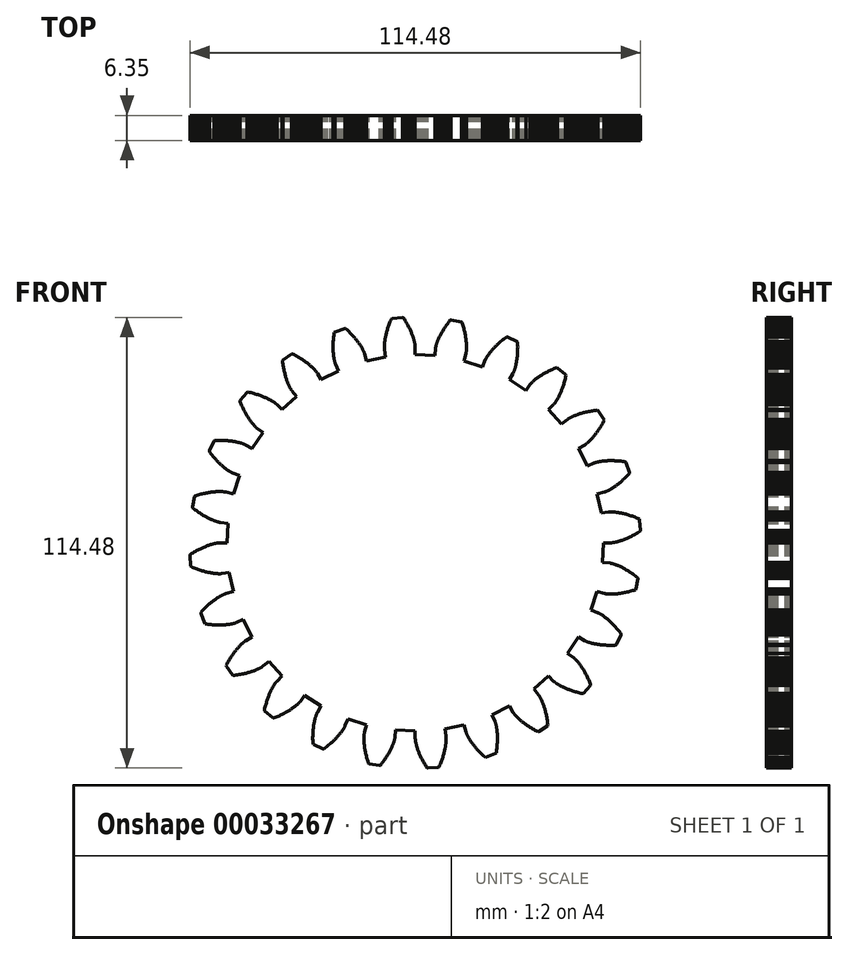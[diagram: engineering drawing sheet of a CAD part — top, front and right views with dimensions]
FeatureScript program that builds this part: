
annotation { "Feature Type Name" : "Feature", "Feature Type Description" : "" }
export const myFeature = defineFeature(function(context is Context, id is Id, definition is map)
    precondition{}
    {
        {
            var Q0;
            Q0=qCreatedBy(makeId("Front.planeOp"),FACE);
            var sketch = newSketch(context, id + "F0", { "sketchPlane" : qUnion([Q0])});
            skLineSegment(sketch, "E0", {"start": v(47.85, 0) * mm, "end": v(49.75, 0) * mm});
            skLineSegment(sketch, "E1", {"start": v(49.75, 0) * mm, "end": v(49.78, 0) * mm});
            skLineSegment(sketch, "E2", {"start": v(49.78, 0) * mm, "end": v(49.82, 0) * mm});
            skLineSegment(sketch, "E3", {"start": v(49.82, 0) * mm, "end": v(49.87, 0) * mm});
            skLineSegment(sketch, "E4", {"start": v(49.87, 0) * mm, "end": v(49.93, 0.01) * mm});
            skLineSegment(sketch, "E5", {"start": v(49.93, 0.01) * mm, "end": v(50, 0.02) * mm});
            skLineSegment(sketch, "E6", {"start": v(50, 0.02) * mm, "end": v(50.08, 0.03) * mm});
            skLineSegment(sketch, "E7", {"start": v(50.08, 0.03) * mm, "end": v(50.17, 0.04) * mm});
            skLineSegment(sketch, "E8", {"start": v(50.17, 0.04) * mm, "end": v(50.27, 0.05) * mm});
            skLineSegment(sketch, "E9", {"start": v(50.27, 0.05) * mm, "end": v(50.38, 0.07) * mm});
            skLineSegment(sketch, "E10", {"start": v(50.38, 0.07) * mm, "end": v(50.5, 0.1) * mm});
            skLineSegment(sketch, "E11", {"start": v(50.5, 0.1) * mm, "end": v(50.63, 0.12) * mm});
            skLineSegment(sketch, "E12", {"start": v(50.63, 0.12) * mm, "end": v(50.78, 0.15) * mm});
            skLineSegment(sketch, "E13", {"start": v(50.78, 0.15) * mm, "end": v(50.93, 0.18) * mm});
            skLineSegment(sketch, "E14", {"start": v(50.93, 0.18) * mm, "end": v(51.09, 0.21) * mm});
            skLineSegment(sketch, "E15", {"start": v(51.09, 0.21) * mm, "end": v(51.26, 0.26) * mm});
            skLineSegment(sketch, "E16", {"start": v(51.26, 0.26) * mm, "end": v(51.44, 0.3) * mm});
            skLineSegment(sketch, "E17", {"start": v(51.44, 0.3) * mm, "end": v(51.63, 0.36) * mm});
            skLineSegment(sketch, "E18", {"start": v(51.63, 0.36) * mm, "end": v(51.83, 0.42) * mm});
            skLineSegment(sketch, "E19", {"start": v(51.83, 0.42) * mm, "end": v(52.03, 0.48) * mm});
            skLineSegment(sketch, "E20", {"start": v(52.03, 0.48) * mm, "end": v(52.25, 0.55) * mm});
            skLineSegment(sketch, "E21", {"start": v(52.25, 0.55) * mm, "end": v(52.48, 0.63) * mm});
            skLineSegment(sketch, "E22", {"start": v(52.48, 0.63) * mm, "end": v(52.71, 0.71) * mm});
            skLineSegment(sketch, "E23", {"start": v(52.71, 0.71) * mm, "end": v(52.95, 0.8) * mm});
            skLineSegment(sketch, "E24", {"start": v(52.95, 0.8) * mm, "end": v(53.2, 0.9) * mm});
            skLineSegment(sketch, "E25", {"start": v(53.2, 0.9) * mm, "end": v(53.47, 1) * mm});
            skLineSegment(sketch, "E26", {"start": v(53.47, 1) * mm, "end": v(53.73, 1.12) * mm});
            skLineSegment(sketch, "E27", {"start": v(53.73, 1.12) * mm, "end": v(54, 1.25) * mm});
            skLineSegment(sketch, "E28", {"start": v(54, 1.25) * mm, "end": v(54.3, 1.38) * mm});
            skLineSegment(sketch, "E29", {"start": v(54.3, 1.38) * mm, "end": v(54.58, 1.52) * mm});
            skLineSegment(sketch, "E30", {"start": v(54.58, 1.52) * mm, "end": v(54.88, 1.67) * mm});
            skLineSegment(sketch, "E31", {"start": v(54.88, 1.67) * mm, "end": v(55.19, 1.82) * mm});
            skLineSegment(sketch, "E32", {"start": v(55.19, 1.82) * mm, "end": v(55.5, 1.99) * mm});
            skLineSegment(sketch, "E33", {"start": v(55.5, 1.99) * mm, "end": v(55.82, 2.17) * mm});
            skLineSegment(sketch, "E34", {"start": v(55.82, 2.17) * mm, "end": v(56.15, 2.35) * mm});
            skLineSegment(sketch, "E35", {"start": v(56.15, 2.35) * mm, "end": v(56.48, 2.55) * mm});
            skLineSegment(sketch, "E36", {"start": v(56.48, 2.55) * mm, "end": v(56.82, 2.76) * mm});
            skLineSegment(sketch, "E37", {"start": v(56.82, 2.76) * mm, "end": v(57.16, 2.97) * mm});
            skLineSegment(sketch, "E38", {"start": v(57.16, 2.97) * mm, "end": v(57.24, 3.19) * mm});
            skLineSegment(sketch, "E39", {"start": v(57.24, 3.19) * mm, "end": v(57.03, 5.86) * mm});
            skLineSegment(sketch, "E40", {"start": v(57.03, 5.86) * mm, "end": v(56.92, 6.06) * mm});
            skLineSegment(sketch, "E41", {"start": v(56.92, 6.06) * mm, "end": v(56.54, 6.22) * mm});
            skLineSegment(sketch, "E42", {"start": v(56.54, 6.22) * mm, "end": v(56.18, 6.37) * mm});
            skLineSegment(sketch, "E43", {"start": v(56.18, 6.37) * mm, "end": v(55.82, 6.5) * mm});
            skLineSegment(sketch, "E44", {"start": v(55.82, 6.5) * mm, "end": v(55.47, 6.64) * mm});
            skLineSegment(sketch, "E45", {"start": v(55.47, 6.64) * mm, "end": v(55.12, 6.77) * mm});
            skLineSegment(sketch, "E46", {"start": v(55.12, 6.77) * mm, "end": v(54.79, 6.88) * mm});
            skLineSegment(sketch, "E47", {"start": v(54.79, 6.88) * mm, "end": v(54.46, 6.99) * mm});
            skLineSegment(sketch, "E48", {"start": v(54.46, 6.99) * mm, "end": v(54.14, 7.1) * mm});
            skLineSegment(sketch, "E49", {"start": v(54.14, 7.1) * mm, "end": v(53.83, 7.18) * mm});
            skLineSegment(sketch, "E50", {"start": v(53.83, 7.18) * mm, "end": v(53.53, 7.27) * mm});
            skLineSegment(sketch, "E51", {"start": v(53.53, 7.27) * mm, "end": v(53.24, 7.34) * mm});
            skLineSegment(sketch, "E52", {"start": v(53.24, 7.34) * mm, "end": v(52.96, 7.41) * mm});
            skLineSegment(sketch, "E53", {"start": v(52.96, 7.41) * mm, "end": v(52.69, 7.48) * mm});
            skLineSegment(sketch, "E54", {"start": v(52.69, 7.48) * mm, "end": v(52.42, 7.54) * mm});
            skLineSegment(sketch, "E55", {"start": v(52.42, 7.54) * mm, "end": v(52.17, 7.59) * mm});
            skLineSegment(sketch, "E56", {"start": v(52.17, 7.59) * mm, "end": v(51.92, 7.63) * mm});
            skLineSegment(sketch, "E57", {"start": v(51.92, 7.63) * mm, "end": v(51.69, 7.68) * mm});
            skLineSegment(sketch, "E58", {"start": v(51.69, 7.68) * mm, "end": v(51.46, 7.71) * mm});
            skLineSegment(sketch, "E59", {"start": v(51.46, 7.71) * mm, "end": v(51.25, 7.74) * mm});
            skLineSegment(sketch, "E60", {"start": v(51.25, 7.74) * mm, "end": v(51.04, 7.77) * mm});
            skLineSegment(sketch, "E61", {"start": v(51.04, 7.77) * mm, "end": v(50.84, 7.8) * mm});
            skLineSegment(sketch, "E62", {"start": v(50.84, 7.8) * mm, "end": v(50.66, 7.8) * mm});
            skLineSegment(sketch, "E63", {"start": v(50.66, 7.8) * mm, "end": v(50.48, 7.82) * mm});
            skLineSegment(sketch, "E64", {"start": v(50.48, 7.82) * mm, "end": v(50.32, 7.84) * mm});
            skLineSegment(sketch, "E65", {"start": v(50.32, 7.84) * mm, "end": v(50.16, 7.85) * mm});
            skLineSegment(sketch, "E66", {"start": v(50.16, 7.85) * mm, "end": v(50.02, 7.85) * mm});
            skLineSegment(sketch, "E67", {"start": v(50.02, 7.85) * mm, "end": v(49.89, 7.86) * mm});
            skLineSegment(sketch, "E68", {"start": v(49.89, 7.86) * mm, "end": v(49.77, 7.86) * mm});
            skLineSegment(sketch, "E69", {"start": v(49.77, 7.86) * mm, "end": v(49.65, 7.86) * mm});
            skLineSegment(sketch, "E70", {"start": v(49.65, 7.86) * mm, "end": v(49.55, 7.85) * mm});
            skLineSegment(sketch, "E71", {"start": v(49.55, 7.85) * mm, "end": v(49.46, 7.85) * mm});
            skLineSegment(sketch, "E72", {"start": v(49.46, 7.85) * mm, "end": v(49.38, 7.85) * mm});
            skLineSegment(sketch, "E73", {"start": v(49.38, 7.85) * mm, "end": v(49.3, 7.84) * mm});
            skLineSegment(sketch, "E74", {"start": v(49.3, 7.84) * mm, "end": v(49.25, 7.84) * mm});
            skLineSegment(sketch, "E75", {"start": v(49.25, 7.84) * mm, "end": v(49.2, 7.83) * mm});
            skLineSegment(sketch, "E76", {"start": v(49.2, 7.83) * mm, "end": v(49.16, 7.83) * mm});
            skLineSegment(sketch, "E77", {"start": v(49.16, 7.83) * mm, "end": v(49.13, 7.83) * mm});
            skLineSegment(sketch, "E78", {"start": v(49.13, 7.83) * mm, "end": v(49.11, 7.82) * mm});
            skLineSegment(sketch, "E79", {"start": v(49.11, 7.82) * mm, "end": v(47.25, 7.53) * mm});
            skLineSegment(sketch, "E80", {"start": v(47.25, 7.53) * mm, "end": v(46.22, 12.38) * mm});
            skLineSegment(sketch, "E81", {"start": v(46.22, 12.38) * mm, "end": v(48.04, 12.87) * mm});
            skLineSegment(sketch, "E82", {"start": v(48.04, 12.87) * mm, "end": v(48.06, 12.88) * mm});
            skLineSegment(sketch, "E83", {"start": v(48.06, 12.88) * mm, "end": v(48.08, 12.89) * mm});
            skLineSegment(sketch, "E84", {"start": v(48.08, 12.89) * mm, "end": v(48.12, 12.9) * mm});
            skLineSegment(sketch, "E85", {"start": v(48.12, 12.9) * mm, "end": v(48.17, 12.91) * mm});
            skLineSegment(sketch, "E86", {"start": v(48.17, 12.91) * mm, "end": v(48.22, 12.93) * mm});
            skLineSegment(sketch, "E87", {"start": v(48.22, 12.93) * mm, "end": v(48.29, 12.96) * mm});
            skLineSegment(sketch, "E88", {"start": v(48.29, 12.96) * mm, "end": v(48.36, 12.99) * mm});
            skLineSegment(sketch, "E89", {"start": v(48.36, 12.99) * mm, "end": v(48.45, 13.02) * mm});
            skLineSegment(sketch, "E90", {"start": v(48.45, 13.02) * mm, "end": v(48.54, 13.06) * mm});
            skLineSegment(sketch, "E91", {"start": v(48.54, 13.06) * mm, "end": v(48.65, 13.1) * mm});
            skLineSegment(sketch, "E92", {"start": v(48.65, 13.1) * mm, "end": v(48.76, 13.16) * mm});
            skLineSegment(sketch, "E93", {"start": v(48.76, 13.16) * mm, "end": v(48.88, 13.22) * mm});
            skLineSegment(sketch, "E94", {"start": v(48.88, 13.22) * mm, "end": v(49, 13.28) * mm});
            skLineSegment(sketch, "E95", {"start": v(49, 13.28) * mm, "end": v(49.15, 13.35) * mm});
            skLineSegment(sketch, "E96", {"start": v(49.15, 13.35) * mm, "end": v(49.29, 13.43) * mm});
            skLineSegment(sketch, "E97", {"start": v(49.29, 13.43) * mm, "end": v(49.44, 13.52) * mm});
            skLineSegment(sketch, "E98", {"start": v(49.44, 13.52) * mm, "end": v(49.6, 13.6) * mm});
            skLineSegment(sketch, "E99", {"start": v(49.6, 13.6) * mm, "end": v(49.77, 13.7) * mm});
            skLineSegment(sketch, "E100", {"start": v(49.77, 13.7) * mm, "end": v(49.95, 13.82) * mm});
            skLineSegment(sketch, "E101", {"start": v(49.95, 13.82) * mm, "end": v(50.14, 13.93) * mm});
            skLineSegment(sketch, "E102", {"start": v(50.14, 13.93) * mm, "end": v(50.33, 14.06) * mm});
            skLineSegment(sketch, "E103", {"start": v(50.33, 14.06) * mm, "end": v(50.53, 14.19) * mm});
            skLineSegment(sketch, "E104", {"start": v(50.53, 14.19) * mm, "end": v(50.73, 14.33) * mm});
            skLineSegment(sketch, "E105", {"start": v(50.73, 14.33) * mm, "end": v(50.94, 14.48) * mm});
            skLineSegment(sketch, "E106", {"start": v(50.94, 14.48) * mm, "end": v(51.16, 14.64) * mm});
            skLineSegment(sketch, "E107", {"start": v(51.16, 14.64) * mm, "end": v(51.38, 14.81) * mm});
            skLineSegment(sketch, "E108", {"start": v(51.38, 14.81) * mm, "end": v(51.61, 15) * mm});
            skLineSegment(sketch, "E109", {"start": v(51.61, 15) * mm, "end": v(51.85, 15.18) * mm});
            skLineSegment(sketch, "E110", {"start": v(51.85, 15.18) * mm, "end": v(52.09, 15.38) * mm});
            skLineSegment(sketch, "E111", {"start": v(52.09, 15.38) * mm, "end": v(52.33, 15.6) * mm});
            skLineSegment(sketch, "E112", {"start": v(52.33, 15.6) * mm, "end": v(52.58, 15.81) * mm});
            skLineSegment(sketch, "E113", {"start": v(52.58, 15.81) * mm, "end": v(52.84, 16.04) * mm});
            skLineSegment(sketch, "E114", {"start": v(52.84, 16.04) * mm, "end": v(53.1, 16.29) * mm});
            skLineSegment(sketch, "E115", {"start": v(53.1, 16.29) * mm, "end": v(53.36, 16.54) * mm});
            skLineSegment(sketch, "E116", {"start": v(53.36, 16.54) * mm, "end": v(53.63, 16.8) * mm});
            skLineSegment(sketch, "E117", {"start": v(53.63, 16.8) * mm, "end": v(53.9, 17.08) * mm});
            skLineSegment(sketch, "E118", {"start": v(53.9, 17.08) * mm, "end": v(54.17, 17.37) * mm});
            skLineSegment(sketch, "E119", {"start": v(54.17, 17.37) * mm, "end": v(54.44, 17.67) * mm});
            skLineSegment(sketch, "E120", {"start": v(54.44, 17.67) * mm, "end": v(54.46, 17.9) * mm});
            skLineSegment(sketch, "E121", {"start": v(54.46, 17.9) * mm, "end": v(53.57, 20.42) * mm});
            skLineSegment(sketch, "E122", {"start": v(53.57, 20.42) * mm, "end": v(53.41, 20.58) * mm});
            skLineSegment(sketch, "E123", {"start": v(53.41, 20.58) * mm, "end": v(53, 20.64) * mm});
            skLineSegment(sketch, "E124", {"start": v(53, 20.64) * mm, "end": v(52.61, 20.7) * mm});
            skLineSegment(sketch, "E125", {"start": v(52.61, 20.7) * mm, "end": v(52.23, 20.74) * mm});
            skLineSegment(sketch, "E126", {"start": v(52.23, 20.74) * mm, "end": v(51.86, 20.77) * mm});
            skLineSegment(sketch, "E127", {"start": v(51.86, 20.77) * mm, "end": v(51.5, 20.8) * mm});
            skLineSegment(sketch, "E128", {"start": v(51.5, 20.8) * mm, "end": v(51.14, 20.83) * mm});
            skLineSegment(sketch, "E129", {"start": v(51.14, 20.83) * mm, "end": v(50.8, 20.85) * mm});
            skLineSegment(sketch, "E130", {"start": v(50.8, 20.85) * mm, "end": v(50.46, 20.86) * mm});
            skLineSegment(sketch, "E131", {"start": v(50.46, 20.86) * mm, "end": v(50.14, 20.87) * mm});
            skLineSegment(sketch, "E132", {"start": v(50.14, 20.87) * mm, "end": v(49.83, 20.87) * mm});
            skLineSegment(sketch, "E133", {"start": v(49.83, 20.87) * mm, "end": v(49.53, 20.87) * mm});
            skLineSegment(sketch, "E134", {"start": v(49.53, 20.87) * mm, "end": v(49.24, 20.87) * mm});
            skLineSegment(sketch, "E135", {"start": v(49.24, 20.87) * mm, "end": v(48.96, 20.86) * mm});
            skLineSegment(sketch, "E136", {"start": v(48.96, 20.86) * mm, "end": v(48.68, 20.85) * mm});
            skLineSegment(sketch, "E137", {"start": v(48.68, 20.85) * mm, "end": v(48.43, 20.83) * mm});
            skLineSegment(sketch, "E138", {"start": v(48.43, 20.83) * mm, "end": v(48.18, 20.81) * mm});
            skLineSegment(sketch, "E139", {"start": v(48.18, 20.81) * mm, "end": v(47.94, 20.8) * mm});
            skLineSegment(sketch, "E140", {"start": v(47.94, 20.8) * mm, "end": v(47.71, 20.77) * mm});
            skLineSegment(sketch, "E141", {"start": v(47.71, 20.77) * mm, "end": v(47.5, 20.74) * mm});
            skLineSegment(sketch, "E142", {"start": v(47.5, 20.74) * mm, "end": v(47.3, 20.71) * mm});
            skLineSegment(sketch, "E143", {"start": v(47.3, 20.71) * mm, "end": v(47.1, 20.69) * mm});
            skLineSegment(sketch, "E144", {"start": v(47.1, 20.69) * mm, "end": v(46.91, 20.66) * mm});
            skLineSegment(sketch, "E145", {"start": v(46.91, 20.66) * mm, "end": v(46.74, 20.62) * mm});
            skLineSegment(sketch, "E146", {"start": v(46.74, 20.62) * mm, "end": v(46.58, 20.6) * mm});
            skLineSegment(sketch, "E147", {"start": v(46.58, 20.6) * mm, "end": v(46.43, 20.56) * mm});
            skLineSegment(sketch, "E148", {"start": v(46.43, 20.56) * mm, "end": v(46.29, 20.53) * mm});
            skLineSegment(sketch, "E149", {"start": v(46.29, 20.53) * mm, "end": v(46.15, 20.5) * mm});
            skLineSegment(sketch, "E150", {"start": v(46.15, 20.5) * mm, "end": v(46.04, 20.47) * mm});
            skLineSegment(sketch, "E151", {"start": v(46.04, 20.47) * mm, "end": v(45.93, 20.44) * mm});
            skLineSegment(sketch, "E152", {"start": v(45.93, 20.44) * mm, "end": v(45.83, 20.4) * mm});
            skLineSegment(sketch, "E153", {"start": v(45.83, 20.4) * mm, "end": v(45.74, 20.38) * mm});
            skLineSegment(sketch, "E154", {"start": v(45.74, 20.38) * mm, "end": v(45.66, 20.36) * mm});
            skLineSegment(sketch, "E155", {"start": v(45.66, 20.36) * mm, "end": v(45.6, 20.34) * mm});
            skLineSegment(sketch, "E156", {"start": v(45.6, 20.34) * mm, "end": v(45.54, 20.32) * mm});
            skLineSegment(sketch, "E157", {"start": v(45.54, 20.32) * mm, "end": v(45.5, 20.3) * mm});
            skLineSegment(sketch, "E158", {"start": v(45.5, 20.3) * mm, "end": v(45.46, 20.29) * mm});
            skLineSegment(sketch, "E159", {"start": v(45.46, 20.29) * mm, "end": v(45.43, 20.28) * mm});
            skLineSegment(sketch, "E160", {"start": v(45.43, 20.28) * mm, "end": v(45.41, 20.27) * mm});
            skLineSegment(sketch, "E161", {"start": v(45.41, 20.27) * mm, "end": v(43.7, 19.5) * mm});
            skLineSegment(sketch, "E162", {"start": v(43.7, 19.5) * mm, "end": v(41.43, 23.92) * mm});
            skLineSegment(sketch, "E163", {"start": v(41.43, 23.92) * mm, "end": v(43.07, 24.87) * mm});
            skLineSegment(sketch, "E164", {"start": v(43.07, 24.87) * mm, "end": v(43.09, 24.88) * mm});
            skLineSegment(sketch, "E165", {"start": v(43.09, 24.88) * mm, "end": v(43.1, 24.9) * mm});
            skLineSegment(sketch, "E166", {"start": v(43.1, 24.9) * mm, "end": v(43.14, 24.91) * mm});
            skLineSegment(sketch, "E167", {"start": v(43.14, 24.91) * mm, "end": v(43.18, 24.94) * mm});
            skLineSegment(sketch, "E168", {"start": v(43.18, 24.94) * mm, "end": v(43.23, 24.97) * mm});
            skLineSegment(sketch, "E169", {"start": v(43.23, 24.97) * mm, "end": v(43.29, 25.02) * mm});
            skLineSegment(sketch, "E170", {"start": v(43.29, 25.02) * mm, "end": v(43.35, 25.06) * mm});
            skLineSegment(sketch, "E171", {"start": v(43.35, 25.06) * mm, "end": v(43.43, 25.12) * mm});
            skLineSegment(sketch, "E172", {"start": v(43.43, 25.12) * mm, "end": v(43.5, 25.18) * mm});
            skLineSegment(sketch, "E173", {"start": v(43.5, 25.18) * mm, "end": v(43.6, 25.25) * mm});
            skLineSegment(sketch, "E174", {"start": v(43.6, 25.25) * mm, "end": v(43.69, 25.33) * mm});
            skLineSegment(sketch, "E175", {"start": v(43.69, 25.33) * mm, "end": v(43.8, 25.42) * mm});
            skLineSegment(sketch, "E176", {"start": v(43.8, 25.42) * mm, "end": v(43.9, 25.51) * mm});
            skLineSegment(sketch, "E177", {"start": v(43.9, 25.51) * mm, "end": v(44.01, 25.62) * mm});
            skLineSegment(sketch, "E178", {"start": v(44.01, 25.62) * mm, "end": v(44.13, 25.73) * mm});
            skLineSegment(sketch, "E179", {"start": v(44.13, 25.73) * mm, "end": v(44.26, 25.85) * mm});
            skLineSegment(sketch, "E180", {"start": v(44.26, 25.85) * mm, "end": v(44.4, 25.98) * mm});
            skLineSegment(sketch, "E181", {"start": v(44.4, 25.98) * mm, "end": v(44.53, 26.12) * mm});
            skLineSegment(sketch, "E182", {"start": v(44.53, 26.12) * mm, "end": v(44.67, 26.27) * mm});
            skLineSegment(sketch, "E183", {"start": v(44.67, 26.27) * mm, "end": v(44.82, 26.43) * mm});
            skLineSegment(sketch, "E184", {"start": v(44.82, 26.43) * mm, "end": v(44.97, 26.6) * mm});
            skLineSegment(sketch, "E185", {"start": v(44.97, 26.6) * mm, "end": v(45.13, 26.78) * mm});
            skLineSegment(sketch, "E186", {"start": v(45.13, 26.78) * mm, "end": v(45.3, 26.97) * mm});
            skLineSegment(sketch, "E187", {"start": v(45.3, 26.97) * mm, "end": v(45.46, 27.17) * mm});
            skLineSegment(sketch, "E188", {"start": v(45.46, 27.17) * mm, "end": v(45.63, 27.39) * mm});
            skLineSegment(sketch, "E189", {"start": v(45.63, 27.39) * mm, "end": v(45.8, 27.6) * mm});
            skLineSegment(sketch, "E190", {"start": v(45.8, 27.6) * mm, "end": v(45.97, 27.84) * mm});
            skLineSegment(sketch, "E191", {"start": v(45.97, 27.84) * mm, "end": v(46.15, 28.08) * mm});
            skLineSegment(sketch, "E192", {"start": v(46.15, 28.08) * mm, "end": v(46.33, 28.34) * mm});
            skLineSegment(sketch, "E193", {"start": v(46.33, 28.34) * mm, "end": v(46.51, 28.6) * mm});
            skLineSegment(sketch, "E194", {"start": v(46.51, 28.6) * mm, "end": v(46.7, 28.88) * mm});
            skLineSegment(sketch, "E195", {"start": v(46.7, 28.88) * mm, "end": v(46.88, 29.17) * mm});
            skLineSegment(sketch, "E196", {"start": v(46.88, 29.17) * mm, "end": v(47.07, 29.47) * mm});
            skLineSegment(sketch, "E197", {"start": v(47.07, 29.47) * mm, "end": v(47.26, 29.79) * mm});
            skLineSegment(sketch, "E198", {"start": v(47.26, 29.79) * mm, "end": v(47.45, 30.11) * mm});
            skLineSegment(sketch, "E199", {"start": v(47.45, 30.11) * mm, "end": v(47.64, 30.45) * mm});
            skLineSegment(sketch, "E200", {"start": v(47.64, 30.45) * mm, "end": v(47.83, 30.8) * mm});
            skLineSegment(sketch, "E201", {"start": v(47.83, 30.8) * mm, "end": v(48.02, 31.16) * mm});
            skLineSegment(sketch, "E202", {"start": v(48.02, 31.16) * mm, "end": v(47.98, 31.38) * mm});
            skLineSegment(sketch, "E203", {"start": v(47.98, 31.38) * mm, "end": v(46.46, 33.59) * mm});
            skLineSegment(sketch, "E204", {"start": v(46.46, 33.59) * mm, "end": v(46.26, 33.7) * mm});
            skLineSegment(sketch, "E205", {"start": v(46.26, 33.7) * mm, "end": v(45.86, 33.66) * mm});
            skLineSegment(sketch, "E206", {"start": v(45.86, 33.66) * mm, "end": v(45.47, 33.6) * mm});
            skLineSegment(sketch, "E207", {"start": v(45.47, 33.6) * mm, "end": v(45.09, 33.55) * mm});
            skLineSegment(sketch, "E208", {"start": v(45.09, 33.55) * mm, "end": v(44.71, 33.49) * mm});
            skLineSegment(sketch, "E209", {"start": v(44.71, 33.49) * mm, "end": v(44.35, 33.42) * mm});
            skLineSegment(sketch, "E210", {"start": v(44.35, 33.42) * mm, "end": v(44, 33.35) * mm});
            skLineSegment(sketch, "E211", {"start": v(44, 33.35) * mm, "end": v(43.67, 33.28) * mm});
            skLineSegment(sketch, "E212", {"start": v(43.67, 33.28) * mm, "end": v(43.34, 33.21) * mm});
            skLineSegment(sketch, "E213", {"start": v(43.34, 33.21) * mm, "end": v(43.03, 33.14) * mm});
            skLineSegment(sketch, "E214", {"start": v(43.03, 33.14) * mm, "end": v(42.73, 33.06) * mm});
            skLineSegment(sketch, "E215", {"start": v(42.73, 33.06) * mm, "end": v(42.44, 32.98) * mm});
            skLineSegment(sketch, "E216", {"start": v(42.44, 32.98) * mm, "end": v(42.16, 32.9) * mm});
            skLineSegment(sketch, "E217", {"start": v(42.16, 32.9) * mm, "end": v(41.89, 32.82) * mm});
            skLineSegment(sketch, "E218", {"start": v(41.89, 32.82) * mm, "end": v(41.63, 32.74) * mm});
            skLineSegment(sketch, "E219", {"start": v(41.63, 32.74) * mm, "end": v(41.38, 32.65) * mm});
            skLineSegment(sketch, "E220", {"start": v(41.38, 32.65) * mm, "end": v(41.15, 32.57) * mm});
            skLineSegment(sketch, "E221", {"start": v(41.15, 32.57) * mm, "end": v(40.92, 32.5) * mm});
            skLineSegment(sketch, "E222", {"start": v(40.92, 32.5) * mm, "end": v(40.71, 32.4) * mm});
            skLineSegment(sketch, "E223", {"start": v(40.71, 32.4) * mm, "end": v(40.5, 32.33) * mm});
            skLineSegment(sketch, "E224", {"start": v(40.5, 32.33) * mm, "end": v(40.32, 32.25) * mm});
            skLineSegment(sketch, "E225", {"start": v(40.32, 32.25) * mm, "end": v(40.14, 32.17) * mm});
            skLineSegment(sketch, "E226", {"start": v(40.14, 32.17) * mm, "end": v(39.97, 32.1) * mm});
            skLineSegment(sketch, "E227", {"start": v(39.97, 32.1) * mm, "end": v(39.8, 32.02) * mm});
            skLineSegment(sketch, "E228", {"start": v(39.8, 32.02) * mm, "end": v(39.66, 31.95) * mm});
            skLineSegment(sketch, "E229", {"start": v(39.66, 31.95) * mm, "end": v(39.52, 31.88) * mm});
            skLineSegment(sketch, "E230", {"start": v(39.52, 31.88) * mm, "end": v(39.4, 31.8) * mm});
            skLineSegment(sketch, "E231", {"start": v(39.4, 31.8) * mm, "end": v(39.28, 31.75) * mm});
            skLineSegment(sketch, "E232", {"start": v(39.28, 31.75) * mm, "end": v(39.17, 31.69) * mm});
            skLineSegment(sketch, "E233", {"start": v(39.17, 31.69) * mm, "end": v(39.07, 31.63) * mm});
            skLineSegment(sketch, "E234", {"start": v(39.07, 31.63) * mm, "end": v(38.98, 31.58) * mm});
            skLineSegment(sketch, "E235", {"start": v(38.98, 31.58) * mm, "end": v(38.9, 31.53) * mm});
            skLineSegment(sketch, "E236", {"start": v(38.9, 31.53) * mm, "end": v(38.84, 31.48) * mm});
            skLineSegment(sketch, "E237", {"start": v(38.84, 31.48) * mm, "end": v(38.78, 31.45) * mm});
            skLineSegment(sketch, "E238", {"start": v(38.78, 31.45) * mm, "end": v(38.73, 31.41) * mm});
            skLineSegment(sketch, "E239", {"start": v(38.73, 31.41) * mm, "end": v(38.69, 31.38) * mm});
            skLineSegment(sketch, "E240", {"start": v(38.69, 31.38) * mm, "end": v(38.66, 31.36) * mm});
            skLineSegment(sketch, "E241", {"start": v(38.66, 31.36) * mm, "end": v(38.64, 31.34) * mm});
            skLineSegment(sketch, "E242", {"start": v(38.64, 31.34) * mm, "end": v(38.62, 31.33) * mm});
            skLineSegment(sketch, "E243", {"start": v(38.62, 31.33) * mm, "end": v(37.16, 30.14) * mm});
            skLineSegment(sketch, "E244", {"start": v(37.16, 30.14) * mm, "end": v(33.83, 33.83) * mm});
            skLineSegment(sketch, "E245", {"start": v(33.83, 33.83) * mm, "end": v(35.17, 35.17) * mm});
            skLineSegment(sketch, "E246", {"start": v(35.17, 35.17) * mm, "end": v(35.18, 35.18) * mm});
            skLineSegment(sketch, "E247", {"start": v(35.18, 35.18) * mm, "end": v(35.2, 35.2) * mm});
            skLineSegment(sketch, "E248", {"start": v(35.2, 35.2) * mm, "end": v(35.22, 35.23) * mm});
            skLineSegment(sketch, "E249", {"start": v(35.22, 35.23) * mm, "end": v(35.26, 35.27) * mm});
            skLineSegment(sketch, "E250", {"start": v(35.26, 35.27) * mm, "end": v(35.3, 35.31) * mm});
            skLineSegment(sketch, "E251", {"start": v(35.3, 35.31) * mm, "end": v(35.34, 35.37) * mm});
            skLineSegment(sketch, "E252", {"start": v(35.34, 35.37) * mm, "end": v(35.4, 35.43) * mm});
            skLineSegment(sketch, "E253", {"start": v(35.4, 35.43) * mm, "end": v(35.45, 35.5) * mm});
            skLineSegment(sketch, "E254", {"start": v(35.45, 35.5) * mm, "end": v(35.5, 35.58) * mm});
            skLineSegment(sketch, "E255", {"start": v(35.5, 35.58) * mm, "end": v(35.57, 35.67) * mm});
            skLineSegment(sketch, "E256", {"start": v(35.57, 35.67) * mm, "end": v(35.65, 35.78) * mm});
            skLineSegment(sketch, "E257", {"start": v(35.65, 35.78) * mm, "end": v(35.72, 35.89) * mm});
            skLineSegment(sketch, "E258", {"start": v(35.72, 35.89) * mm, "end": v(35.8, 36) * mm});
            skLineSegment(sketch, "E259", {"start": v(35.8, 36) * mm, "end": v(35.88, 36.14) * mm});
            skLineSegment(sketch, "E260", {"start": v(35.88, 36.14) * mm, "end": v(35.97, 36.28) * mm});
            skLineSegment(sketch, "E261", {"start": v(35.97, 36.28) * mm, "end": v(36.06, 36.43) * mm});
            skLineSegment(sketch, "E262", {"start": v(36.06, 36.43) * mm, "end": v(36.16, 36.59) * mm});
            skLineSegment(sketch, "E263", {"start": v(36.16, 36.59) * mm, "end": v(36.25, 36.76) * mm});
            skLineSegment(sketch, "E264", {"start": v(36.25, 36.76) * mm, "end": v(36.35, 36.94) * mm});
            skLineSegment(sketch, "E265", {"start": v(36.35, 36.94) * mm, "end": v(36.45, 37.13) * mm});
            skLineSegment(sketch, "E266", {"start": v(36.45, 37.13) * mm, "end": v(36.56, 37.34) * mm});
            skLineSegment(sketch, "E267", {"start": v(36.56, 37.34) * mm, "end": v(36.66, 37.55) * mm});
            skLineSegment(sketch, "E268", {"start": v(36.66, 37.55) * mm, "end": v(36.77, 37.78) * mm});
            skLineSegment(sketch, "E269", {"start": v(36.77, 37.78) * mm, "end": v(36.87, 38.01) * mm});
            skLineSegment(sketch, "E270", {"start": v(36.87, 38.01) * mm, "end": v(36.98, 38.26) * mm});
            skLineSegment(sketch, "E271", {"start": v(36.98, 38.26) * mm, "end": v(37.1, 38.52) * mm});
            skLineSegment(sketch, "E272", {"start": v(37.1, 38.52) * mm, "end": v(37.2, 38.8) * mm});
            skLineSegment(sketch, "E273", {"start": v(37.2, 38.8) * mm, "end": v(37.3, 39.07) * mm});
            skLineSegment(sketch, "E274", {"start": v(37.3, 39.07) * mm, "end": v(37.42, 39.36) * mm});
            skLineSegment(sketch, "E275", {"start": v(37.42, 39.36) * mm, "end": v(37.52, 39.67) * mm});
            skLineSegment(sketch, "E276", {"start": v(37.52, 39.67) * mm, "end": v(37.63, 39.99) * mm});
            skLineSegment(sketch, "E277", {"start": v(37.63, 39.99) * mm, "end": v(37.73, 40.31) * mm});
            skLineSegment(sketch, "E278", {"start": v(37.73, 40.31) * mm, "end": v(37.84, 40.65) * mm});
            skLineSegment(sketch, "E279", {"start": v(37.84, 40.65) * mm, "end": v(37.94, 41) * mm});
            skLineSegment(sketch, "E280", {"start": v(37.94, 41) * mm, "end": v(38.04, 41.37) * mm});
            skLineSegment(sketch, "E281", {"start": v(38.04, 41.37) * mm, "end": v(38.13, 41.74) * mm});
            skLineSegment(sketch, "E282", {"start": v(38.13, 41.74) * mm, "end": v(38.23, 42.13) * mm});
            skLineSegment(sketch, "E283", {"start": v(38.23, 42.13) * mm, "end": v(38.32, 42.52) * mm});
            skLineSegment(sketch, "E284", {"start": v(38.32, 42.52) * mm, "end": v(38.22, 42.73) * mm});
            skLineSegment(sketch, "E285", {"start": v(38.22, 42.73) * mm, "end": v(36.18, 44.47) * mm});
            skLineSegment(sketch, "E286", {"start": v(36.18, 44.47) * mm, "end": v(35.96, 44.53) * mm});
            skLineSegment(sketch, "E287", {"start": v(35.96, 44.53) * mm, "end": v(35.59, 44.38) * mm});
            skLineSegment(sketch, "E288", {"start": v(35.59, 44.38) * mm, "end": v(35.22, 44.23) * mm});
            skLineSegment(sketch, "E289", {"start": v(35.22, 44.23) * mm, "end": v(34.87, 44.07) * mm});
            skLineSegment(sketch, "E290", {"start": v(34.87, 44.07) * mm, "end": v(34.52, 43.92) * mm});
            skLineSegment(sketch, "E291", {"start": v(34.52, 43.92) * mm, "end": v(34.2, 43.76) * mm});
            skLineSegment(sketch, "E292", {"start": v(34.2, 43.76) * mm, "end": v(33.87, 43.6) * mm});
            skLineSegment(sketch, "E293", {"start": v(33.87, 43.6) * mm, "end": v(33.57, 43.45) * mm});
            skLineSegment(sketch, "E294", {"start": v(33.57, 43.45) * mm, "end": v(33.27, 43.3) * mm});
            skLineSegment(sketch, "E295", {"start": v(33.27, 43.3) * mm, "end": v(32.99, 43.14) * mm});
            skLineSegment(sketch, "E296", {"start": v(32.99, 43.14) * mm, "end": v(32.72, 43) * mm});
            skLineSegment(sketch, "E297", {"start": v(32.72, 43) * mm, "end": v(32.46, 42.84) * mm});
            skLineSegment(sketch, "E298", {"start": v(32.46, 42.84) * mm, "end": v(32.2, 42.7) * mm});
            skLineSegment(sketch, "E299", {"start": v(32.2, 42.7) * mm, "end": v(31.97, 42.54) * mm});
            skLineSegment(sketch, "E300", {"start": v(31.97, 42.54) * mm, "end": v(31.74, 42.4) * mm});
            skLineSegment(sketch, "E301", {"start": v(31.74, 42.4) * mm, "end": v(31.52, 42.25) * mm});
            skLineSegment(sketch, "E302", {"start": v(31.52, 42.25) * mm, "end": v(31.32, 42.11) * mm});
            skLineSegment(sketch, "E303", {"start": v(31.32, 42.11) * mm, "end": v(31.12, 41.97) * mm});
            skLineSegment(sketch, "E304", {"start": v(31.12, 41.97) * mm, "end": v(30.94, 41.84) * mm});
            skLineSegment(sketch, "E305", {"start": v(30.94, 41.84) * mm, "end": v(30.76, 41.71) * mm});
            skLineSegment(sketch, "E306", {"start": v(30.76, 41.71) * mm, "end": v(30.6, 41.58) * mm});
            skLineSegment(sketch, "E307", {"start": v(30.6, 41.58) * mm, "end": v(30.44, 41.46) * mm});
            skLineSegment(sketch, "E308", {"start": v(30.44, 41.46) * mm, "end": v(30.3, 41.34) * mm});
            skLineSegment(sketch, "E309", {"start": v(30.3, 41.34) * mm, "end": v(30.17, 41.23) * mm});
            skLineSegment(sketch, "E310", {"start": v(30.17, 41.23) * mm, "end": v(30.04, 41.12) * mm});
            skLineSegment(sketch, "E311", {"start": v(30.04, 41.12) * mm, "end": v(29.93, 41.02) * mm});
            skLineSegment(sketch, "E312", {"start": v(29.93, 41.02) * mm, "end": v(29.82, 40.92) * mm});
            skLineSegment(sketch, "E313", {"start": v(29.82, 40.92) * mm, "end": v(29.72, 40.83) * mm});
            skLineSegment(sketch, "E314", {"start": v(29.72, 40.83) * mm, "end": v(29.63, 40.74) * mm});
            skLineSegment(sketch, "E315", {"start": v(29.63, 40.74) * mm, "end": v(29.55, 40.66) * mm});
            skLineSegment(sketch, "E316", {"start": v(29.55, 40.66) * mm, "end": v(29.48, 40.6) * mm});
            skLineSegment(sketch, "E317", {"start": v(29.48, 40.6) * mm, "end": v(29.42, 40.52) * mm});
            skLineSegment(sketch, "E318", {"start": v(29.42, 40.52) * mm, "end": v(29.37, 40.46) * mm});
            skLineSegment(sketch, "E319", {"start": v(29.37, 40.46) * mm, "end": v(29.32, 40.41) * mm});
            skLineSegment(sketch, "E320", {"start": v(29.32, 40.41) * mm, "end": v(29.28, 40.37) * mm});
            skLineSegment(sketch, "E321", {"start": v(29.28, 40.37) * mm, "end": v(29.25, 40.33) * mm});
            skLineSegment(sketch, "E322", {"start": v(29.25, 40.33) * mm, "end": v(29.22, 40.3) * mm});
            skLineSegment(sketch, "E323", {"start": v(29.22, 40.3) * mm, "end": v(29.2, 40.28) * mm});
            skLineSegment(sketch, "E324", {"start": v(29.2, 40.28) * mm, "end": v(29.2, 40.26) * mm});
            skLineSegment(sketch, "E325", {"start": v(29.2, 40.26) * mm, "end": v(28.09, 38.73) * mm});
            skLineSegment(sketch, "E326", {"start": v(28.09, 38.73) * mm, "end": v(23.92, 41.43) * mm});
            skLineSegment(sketch, "E327", {"start": v(23.92, 41.43) * mm, "end": v(24.87, 43.07) * mm});
            skLineSegment(sketch, "E328", {"start": v(24.87, 43.07) * mm, "end": v(24.88, 43.09) * mm});
            skLineSegment(sketch, "E329", {"start": v(24.88, 43.09) * mm, "end": v(24.89, 43.11) * mm});
            skLineSegment(sketch, "E330", {"start": v(24.89, 43.11) * mm, "end": v(24.9, 43.15) * mm});
            skLineSegment(sketch, "E331", {"start": v(24.9, 43.15) * mm, "end": v(24.93, 43.2) * mm});
            skLineSegment(sketch, "E332", {"start": v(24.93, 43.2) * mm, "end": v(24.95, 43.24) * mm});
            skLineSegment(sketch, "E333", {"start": v(24.95, 43.24) * mm, "end": v(24.98, 43.3) * mm});
            skLineSegment(sketch, "E334", {"start": v(24.98, 43.3) * mm, "end": v(25.01, 43.38) * mm});
            skLineSegment(sketch, "E335", {"start": v(25.01, 43.38) * mm, "end": v(25.05, 43.47) * mm});
            skLineSegment(sketch, "E336", {"start": v(25.05, 43.47) * mm, "end": v(25.09, 43.56) * mm});
            skLineSegment(sketch, "E337", {"start": v(25.09, 43.56) * mm, "end": v(25.13, 43.67) * mm});
            skLineSegment(sketch, "E338", {"start": v(25.13, 43.67) * mm, "end": v(25.17, 43.78) * mm});
            skLineSegment(sketch, "E339", {"start": v(25.17, 43.78) * mm, "end": v(25.22, 43.9) * mm});
            skLineSegment(sketch, "E340", {"start": v(25.22, 43.9) * mm, "end": v(25.26, 44.04) * mm});
            skLineSegment(sketch, "E341", {"start": v(25.26, 44.04) * mm, "end": v(25.3, 44.2) * mm});
            skLineSegment(sketch, "E342", {"start": v(25.3, 44.2) * mm, "end": v(25.36, 44.35) * mm});
            skLineSegment(sketch, "E343", {"start": v(25.36, 44.35) * mm, "end": v(25.4, 44.52) * mm});
            skLineSegment(sketch, "E344", {"start": v(25.4, 44.52) * mm, "end": v(25.45, 44.7) * mm});
            skLineSegment(sketch, "E345", {"start": v(25.45, 44.7) * mm, "end": v(25.5, 44.89) * mm});
            skLineSegment(sketch, "E346", {"start": v(25.5, 44.89) * mm, "end": v(25.55, 45.1) * mm});
            skLineSegment(sketch, "E347", {"start": v(25.55, 45.1) * mm, "end": v(25.6, 45.3) * mm});
            skLineSegment(sketch, "E348", {"start": v(25.6, 45.3) * mm, "end": v(25.65, 45.53) * mm});
            skLineSegment(sketch, "E349", {"start": v(25.65, 45.53) * mm, "end": v(25.7, 45.76) * mm});
            skLineSegment(sketch, "E350", {"start": v(25.7, 45.76) * mm, "end": v(25.74, 46) * mm});
            skLineSegment(sketch, "E351", {"start": v(25.74, 46) * mm, "end": v(25.78, 46.26) * mm});
            skLineSegment(sketch, "E352", {"start": v(25.78, 46.26) * mm, "end": v(25.82, 46.53) * mm});
            skLineSegment(sketch, "E353", {"start": v(25.82, 46.53) * mm, "end": v(25.86, 46.8) * mm});
            skLineSegment(sketch, "E354", {"start": v(25.86, 46.8) * mm, "end": v(25.9, 47.1) * mm});
            skLineSegment(sketch, "E355", {"start": v(25.9, 47.1) * mm, "end": v(25.92, 47.4) * mm});
            skLineSegment(sketch, "E356", {"start": v(25.92, 47.4) * mm, "end": v(25.95, 47.7) * mm});
            skLineSegment(sketch, "E357", {"start": v(25.95, 47.7) * mm, "end": v(25.98, 48.03) * mm});
            skLineSegment(sketch, "E358", {"start": v(25.98, 48.03) * mm, "end": v(26, 48.36) * mm});
            skLineSegment(sketch, "E359", {"start": v(26, 48.36) * mm, "end": v(26.02, 48.7) * mm});
            skLineSegment(sketch, "E360", {"start": v(26.02, 48.7) * mm, "end": v(26.03, 49.06) * mm});
            skLineSegment(sketch, "E361", {"start": v(26.03, 49.06) * mm, "end": v(26.03, 49.43) * mm});
            skLineSegment(sketch, "E362", {"start": v(26.03, 49.43) * mm, "end": v(26.04, 49.8) * mm});
            skLineSegment(sketch, "E363", {"start": v(26.04, 49.8) * mm, "end": v(26.03, 50.19) * mm});
            skLineSegment(sketch, "E364", {"start": v(26.03, 50.19) * mm, "end": v(26.02, 50.58) * mm});
            skLineSegment(sketch, "E365", {"start": v(26.02, 50.58) * mm, "end": v(26, 51) * mm});
            skLineSegment(sketch, "E366", {"start": v(26, 51) * mm, "end": v(25.86, 51.16) * mm});
            skLineSegment(sketch, "E367", {"start": v(25.86, 51.16) * mm, "end": v(23.44, 52.32) * mm});
            skLineSegment(sketch, "E368", {"start": v(23.44, 52.32) * mm, "end": v(23.21, 52.32) * mm});
            skLineSegment(sketch, "E369", {"start": v(23.21, 52.32) * mm, "end": v(22.89, 52.08) * mm});
            skLineSegment(sketch, "E370", {"start": v(22.89, 52.08) * mm, "end": v(22.57, 51.84) * mm});
            skLineSegment(sketch, "E371", {"start": v(22.57, 51.84) * mm, "end": v(22.27, 51.6) * mm});
            skLineSegment(sketch, "E372", {"start": v(22.27, 51.6) * mm, "end": v(21.98, 51.36) * mm});
            skLineSegment(sketch, "E373", {"start": v(21.98, 51.36) * mm, "end": v(21.7, 51.12) * mm});
            skLineSegment(sketch, "E374", {"start": v(21.7, 51.12) * mm, "end": v(21.43, 50.89) * mm});
            skLineSegment(sketch, "E375", {"start": v(21.43, 50.89) * mm, "end": v(21.18, 50.66) * mm});
            skLineSegment(sketch, "E376", {"start": v(21.18, 50.66) * mm, "end": v(20.93, 50.43) * mm});
            skLineSegment(sketch, "E377", {"start": v(20.93, 50.43) * mm, "end": v(20.7, 50.21) * mm});
            skLineSegment(sketch, "E378", {"start": v(20.7, 50.21) * mm, "end": v(20.47, 50) * mm});
            skLineSegment(sketch, "E379", {"start": v(20.47, 50) * mm, "end": v(20.26, 49.78) * mm});
            skLineSegment(sketch, "E380", {"start": v(20.26, 49.78) * mm, "end": v(20.06, 49.57) * mm});
            skLineSegment(sketch, "E381", {"start": v(20.06, 49.57) * mm, "end": v(19.87, 49.37) * mm});
            skLineSegment(sketch, "E382", {"start": v(19.87, 49.37) * mm, "end": v(19.68, 49.17) * mm});
            skLineSegment(sketch, "E383", {"start": v(19.68, 49.17) * mm, "end": v(19.51, 48.97) * mm});
            skLineSegment(sketch, "E384", {"start": v(19.51, 48.97) * mm, "end": v(19.35, 48.78) * mm});
            skLineSegment(sketch, "E385", {"start": v(19.35, 48.78) * mm, "end": v(19.2, 48.6) * mm});
            skLineSegment(sketch, "E386", {"start": v(19.2, 48.6) * mm, "end": v(19.05, 48.42) * mm});
            skLineSegment(sketch, "E387", {"start": v(19.05, 48.42) * mm, "end": v(18.92, 48.25) * mm});
            skLineSegment(sketch, "E388", {"start": v(18.92, 48.25) * mm, "end": v(18.8, 48.09) * mm});
            skLineSegment(sketch, "E389", {"start": v(18.8, 48.09) * mm, "end": v(18.68, 47.93) * mm});
            skLineSegment(sketch, "E390", {"start": v(18.68, 47.93) * mm, "end": v(18.57, 47.78) * mm});
            skLineSegment(sketch, "E391", {"start": v(18.57, 47.78) * mm, "end": v(18.47, 47.63) * mm});
            skLineSegment(sketch, "E392", {"start": v(18.47, 47.63) * mm, "end": v(18.37, 47.5) * mm});
            skLineSegment(sketch, "E393", {"start": v(18.37, 47.5) * mm, "end": v(18.29, 47.37) * mm});
            skLineSegment(sketch, "E394", {"start": v(18.29, 47.37) * mm, "end": v(18.21, 47.24) * mm});
            skLineSegment(sketch, "E395", {"start": v(18.21, 47.24) * mm, "end": v(18.14, 47.13) * mm});
            skLineSegment(sketch, "E396", {"start": v(18.14, 47.13) * mm, "end": v(18.08, 47.03) * mm});
            skLineSegment(sketch, "E397", {"start": v(18.08, 47.03) * mm, "end": v(18.02, 46.93) * mm});
            skLineSegment(sketch, "E398", {"start": v(18.02, 46.93) * mm, "end": v(17.97, 46.84) * mm});
            skLineSegment(sketch, "E399", {"start": v(17.97, 46.84) * mm, "end": v(17.93, 46.76) * mm});
            skLineSegment(sketch, "E400", {"start": v(17.93, 46.76) * mm, "end": v(17.9, 46.69) * mm});
            skLineSegment(sketch, "E401", {"start": v(17.9, 46.69) * mm, "end": v(17.86, 46.62) * mm});
            skLineSegment(sketch, "E402", {"start": v(17.86, 46.62) * mm, "end": v(17.84, 46.57) * mm});
            skLineSegment(sketch, "E403", {"start": v(17.84, 46.57) * mm, "end": v(17.82, 46.52) * mm});
            skLineSegment(sketch, "E404", {"start": v(17.82, 46.52) * mm, "end": v(17.8, 46.49) * mm});
            skLineSegment(sketch, "E405", {"start": v(17.8, 46.49) * mm, "end": v(17.79, 46.46) * mm});
            skLineSegment(sketch, "E406", {"start": v(17.79, 46.46) * mm, "end": v(17.78, 46.45) * mm});
            skLineSegment(sketch, "E407", {"start": v(17.78, 46.45) * mm, "end": v(17.1, 44.68) * mm});
            skLineSegment(sketch, "E408", {"start": v(17.1, 44.68) * mm, "end": v(12.38, 46.22) * mm});
            skLineSegment(sketch, "E409", {"start": v(12.38, 46.22) * mm, "end": v(12.87, 48.04) * mm});
            skLineSegment(sketch, "E410", {"start": v(12.87, 48.04) * mm, "end": v(12.88, 48.06) * mm});
            skLineSegment(sketch, "E411", {"start": v(12.88, 48.06) * mm, "end": v(12.88, 48.08) * mm});
            skLineSegment(sketch, "E412", {"start": v(12.88, 48.08) * mm, "end": v(12.9, 48.12) * mm});
            skLineSegment(sketch, "E413", {"start": v(12.9, 48.12) * mm, "end": v(12.9, 48.17) * mm});
            skLineSegment(sketch, "E414", {"start": v(12.9, 48.17) * mm, "end": v(12.91, 48.23) * mm});
            skLineSegment(sketch, "E415", {"start": v(12.91, 48.23) * mm, "end": v(12.92, 48.3) * mm});
            skLineSegment(sketch, "E416", {"start": v(12.92, 48.3) * mm, "end": v(12.93, 48.38) * mm});
            skLineSegment(sketch, "E417", {"start": v(12.93, 48.38) * mm, "end": v(12.95, 48.47) * mm});
            skLineSegment(sketch, "E418", {"start": v(12.95, 48.47) * mm, "end": v(12.96, 48.57) * mm});
            skLineSegment(sketch, "E419", {"start": v(12.96, 48.57) * mm, "end": v(12.97, 48.68) * mm});
            skLineSegment(sketch, "E420", {"start": v(12.97, 48.68) * mm, "end": v(12.98, 48.8) * mm});
            skLineSegment(sketch, "E421", {"start": v(12.98, 48.8) * mm, "end": v(13, 48.94) * mm});
            skLineSegment(sketch, "E422", {"start": v(13, 48.94) * mm, "end": v(13, 49.08) * mm});
            skLineSegment(sketch, "E423", {"start": v(13, 49.08) * mm, "end": v(13, 49.24) * mm});
            skLineSegment(sketch, "E424", {"start": v(13, 49.24) * mm, "end": v(13.01, 49.4) * mm});
            skLineSegment(sketch, "E425", {"start": v(13.01, 49.4) * mm, "end": v(13.02, 49.58) * mm});
            skLineSegment(sketch, "E426", {"start": v(13.02, 49.58) * mm, "end": v(13.02, 49.76) * mm});
            skLineSegment(sketch, "E427", {"start": v(13.02, 49.76) * mm, "end": v(13.02, 49.96) * mm});
            skLineSegment(sketch, "E428", {"start": v(13.02, 49.96) * mm, "end": v(13.01, 50.17) * mm});
            skLineSegment(sketch, "E429", {"start": v(13.01, 50.17) * mm, "end": v(13, 50.39) * mm});
            skLineSegment(sketch, "E430", {"start": v(13, 50.39) * mm, "end": v(12.99, 50.61) * mm});
            skLineSegment(sketch, "E431", {"start": v(12.99, 50.61) * mm, "end": v(12.97, 50.85) * mm});
            skLineSegment(sketch, "E432", {"start": v(12.97, 50.85) * mm, "end": v(12.95, 51.1) * mm});
            skLineSegment(sketch, "E433", {"start": v(12.95, 51.1) * mm, "end": v(12.93, 51.36) * mm});
            skLineSegment(sketch, "E434", {"start": v(12.93, 51.36) * mm, "end": v(12.9, 51.63) * mm});
            skLineSegment(sketch, "E435", {"start": v(12.9, 51.63) * mm, "end": v(12.86, 51.9) * mm});
            skLineSegment(sketch, "E436", {"start": v(12.86, 51.9) * mm, "end": v(12.82, 52.2) * mm});
            skLineSegment(sketch, "E437", {"start": v(12.82, 52.2) * mm, "end": v(12.77, 52.5) * mm});
            skLineSegment(sketch, "E438", {"start": v(12.77, 52.5) * mm, "end": v(12.72, 52.8) * mm});
            skLineSegment(sketch, "E439", {"start": v(12.72, 52.8) * mm, "end": v(12.66, 53.12) * mm});
            skLineSegment(sketch, "E440", {"start": v(12.66, 53.12) * mm, "end": v(12.6, 53.44) * mm});
            skLineSegment(sketch, "E441", {"start": v(12.6, 53.44) * mm, "end": v(12.52, 53.78) * mm});
            skLineSegment(sketch, "E442", {"start": v(12.52, 53.78) * mm, "end": v(12.44, 54.13) * mm});
            skLineSegment(sketch, "E443", {"start": v(12.44, 54.13) * mm, "end": v(12.36, 54.48) * mm});
            skLineSegment(sketch, "E444", {"start": v(12.36, 54.48) * mm, "end": v(12.26, 54.84) * mm});
            skLineSegment(sketch, "E445", {"start": v(12.26, 54.84) * mm, "end": v(12.16, 55.22) * mm});
            skLineSegment(sketch, "E446", {"start": v(12.16, 55.22) * mm, "end": v(12.04, 55.6) * mm});
            skLineSegment(sketch, "E447", {"start": v(12.04, 55.6) * mm, "end": v(11.92, 55.98) * mm});
            skLineSegment(sketch, "E448", {"start": v(11.92, 55.98) * mm, "end": v(11.74, 56.11) * mm});
            skLineSegment(sketch, "E449", {"start": v(11.74, 56.11) * mm, "end": v(9.1, 56.6) * mm});
            skLineSegment(sketch, "E450", {"start": v(9.1, 56.6) * mm, "end": v(8.88, 56.55) * mm});
            skLineSegment(sketch, "E451", {"start": v(8.88, 56.55) * mm, "end": v(8.63, 56.23) * mm});
            skLineSegment(sketch, "E452", {"start": v(8.63, 56.23) * mm, "end": v(8.39, 55.91) * mm});
            skLineSegment(sketch, "E453", {"start": v(8.39, 55.91) * mm, "end": v(8.16, 55.6) * mm});
            skLineSegment(sketch, "E454", {"start": v(8.16, 55.6) * mm, "end": v(7.94, 55.3) * mm});
            skLineSegment(sketch, "E455", {"start": v(7.94, 55.3) * mm, "end": v(7.73, 55) * mm});
            skLineSegment(sketch, "E456", {"start": v(7.73, 55) * mm, "end": v(7.53, 54.7) * mm});
            skLineSegment(sketch, "E457", {"start": v(7.53, 54.7) * mm, "end": v(7.34, 54.41) * mm});
            skLineSegment(sketch, "E458", {"start": v(7.34, 54.41) * mm, "end": v(7.17, 54.13) * mm});
            skLineSegment(sketch, "E459", {"start": v(7.17, 54.13) * mm, "end": v(7, 53.86) * mm});
            skLineSegment(sketch, "E460", {"start": v(7, 53.86) * mm, "end": v(6.84, 53.59) * mm});
            skLineSegment(sketch, "E461", {"start": v(6.84, 53.59) * mm, "end": v(6.69, 53.33) * mm});
            skLineSegment(sketch, "E462", {"start": v(6.69, 53.33) * mm, "end": v(6.55, 53.07) * mm});
            skLineSegment(sketch, "E463", {"start": v(6.55, 53.07) * mm, "end": v(6.41, 52.83) * mm});
            skLineSegment(sketch, "E464", {"start": v(6.41, 52.83) * mm, "end": v(6.29, 52.59) * mm});
            skLineSegment(sketch, "E465", {"start": v(6.29, 52.59) * mm, "end": v(6.17, 52.35) * mm});
            skLineSegment(sketch, "E466", {"start": v(6.17, 52.35) * mm, "end": v(6.06, 52.13) * mm});
            skLineSegment(sketch, "E467", {"start": v(6.06, 52.13) * mm, "end": v(5.96, 51.91) * mm});
            skLineSegment(sketch, "E468", {"start": v(5.96, 51.91) * mm, "end": v(5.87, 51.7) * mm});
            skLineSegment(sketch, "E469", {"start": v(5.87, 51.7) * mm, "end": v(5.78, 51.5) * mm});
            skLineSegment(sketch, "E470", {"start": v(5.78, 51.5) * mm, "end": v(5.7, 51.31) * mm});
            skLineSegment(sketch, "E471", {"start": v(5.7, 51.31) * mm, "end": v(5.63, 51.13) * mm});
            skLineSegment(sketch, "E472", {"start": v(5.63, 51.13) * mm, "end": v(5.57, 50.95) * mm});
            skLineSegment(sketch, "E473", {"start": v(5.57, 50.95) * mm, "end": v(5.5, 50.79) * mm});
            skLineSegment(sketch, "E474", {"start": v(5.5, 50.79) * mm, "end": v(5.45, 50.63) * mm});
            skLineSegment(sketch, "E475", {"start": v(5.45, 50.63) * mm, "end": v(5.4, 50.49) * mm});
            skLineSegment(sketch, "E476", {"start": v(5.4, 50.49) * mm, "end": v(5.36, 50.35) * mm});
            skLineSegment(sketch, "E477", {"start": v(5.36, 50.35) * mm, "end": v(5.32, 50.22) * mm});
            skLineSegment(sketch, "E478", {"start": v(5.32, 50.22) * mm, "end": v(5.3, 50.1) * mm});
            skLineSegment(sketch, "E479", {"start": v(5.3, 50.1) * mm, "end": v(5.26, 50) * mm});
            skLineSegment(sketch, "E480", {"start": v(5.26, 50) * mm, "end": v(5.24, 49.9) * mm});
            skLineSegment(sketch, "E481", {"start": v(5.24, 49.9) * mm, "end": v(5.22, 49.8) * mm});
            skLineSegment(sketch, "E482", {"start": v(5.22, 49.8) * mm, "end": v(5.2, 49.73) * mm});
            skLineSegment(sketch, "E483", {"start": v(5.2, 49.73) * mm, "end": v(5.19, 49.66) * mm});
            skLineSegment(sketch, "E484", {"start": v(5.19, 49.66) * mm, "end": v(5.17, 49.6) * mm});
            skLineSegment(sketch, "E485", {"start": v(5.17, 49.6) * mm, "end": v(5.17, 49.55) * mm});
            skLineSegment(sketch, "E486", {"start": v(5.17, 49.55) * mm, "end": v(5.16, 49.48) * mm});
            skLineSegment(sketch, "E487", {"start": v(5.16, 49.48) * mm, "end": v(5.15, 49.46) * mm});
            skLineSegment(sketch, "E488", {"start": v(5.15, 49.46) * mm, "end": v(4.96, 47.59) * mm});
            skLineSegment(sketch, "E489", {"start": v(4.96, 47.59) * mm, "end": v(0, 47.85) * mm});
            skLineSegment(sketch, "E490", {"start": v(0, 47.85) * mm, "end": v(0, 49.75) * mm});
            skLineSegment(sketch, "E491", {"start": v(0, 49.75) * mm, "end": v(0, 49.78) * mm});
            skLineSegment(sketch, "E492", {"start": v(0, 49.78) * mm, "end": v(0, 49.82) * mm});
            skLineSegment(sketch, "E493", {"start": v(0, 49.82) * mm, "end": v(0, 49.87) * mm});
            skLineSegment(sketch, "E494", {"start": v(0, 49.87) * mm, "end": v(-0.01, 49.93) * mm});
            skLineSegment(sketch, "E495", {"start": v(-0.01, 49.93) * mm, "end": v(-0.02, 50) * mm});
            skLineSegment(sketch, "E496", {"start": v(-0.02, 50) * mm, "end": v(-0.03, 50.08) * mm});
            skLineSegment(sketch, "E497", {"start": v(-0.03, 50.08) * mm, "end": v(-0.04, 50.17) * mm});
            skLineSegment(sketch, "E498", {"start": v(-0.04, 50.17) * mm, "end": v(-0.05, 50.27) * mm});
            skLineSegment(sketch, "E499", {"start": v(-0.05, 50.27) * mm, "end": v(-0.07, 50.38) * mm});
            skLineSegment(sketch, "E500", {"start": v(-0.07, 50.38) * mm, "end": v(-0.1, 50.5) * mm});
            skLineSegment(sketch, "E501", {"start": v(-0.1, 50.5) * mm, "end": v(-0.12, 50.63) * mm});
            skLineSegment(sketch, "E502", {"start": v(-0.12, 50.63) * mm, "end": v(-0.15, 50.78) * mm});
            skLineSegment(sketch, "E503", {"start": v(-0.15, 50.78) * mm, "end": v(-0.18, 50.93) * mm});
            skLineSegment(sketch, "E504", {"start": v(-0.18, 50.93) * mm, "end": v(-0.21, 51.09) * mm});
            skLineSegment(sketch, "E505", {"start": v(-0.21, 51.09) * mm, "end": v(-0.26, 51.26) * mm});
            skLineSegment(sketch, "E506", {"start": v(-0.26, 51.26) * mm, "end": v(-0.3, 51.44) * mm});
            skLineSegment(sketch, "E507", {"start": v(-0.3, 51.44) * mm, "end": v(-0.36, 51.63) * mm});
            skLineSegment(sketch, "E508", {"start": v(-0.36, 51.63) * mm, "end": v(-0.42, 51.83) * mm});
            skLineSegment(sketch, "E509", {"start": v(-0.42, 51.83) * mm, "end": v(-0.48, 52.03) * mm});
            skLineSegment(sketch, "E510", {"start": v(-0.48, 52.03) * mm, "end": v(-0.55, 52.25) * mm});
            skLineSegment(sketch, "E511", {"start": v(-0.55, 52.25) * mm, "end": v(-0.63, 52.48) * mm});
            skLineSegment(sketch, "E512", {"start": v(-0.63, 52.48) * mm, "end": v(-0.71, 52.71) * mm});
            skLineSegment(sketch, "E513", {"start": v(-0.71, 52.71) * mm, "end": v(-0.8, 52.95) * mm});
            skLineSegment(sketch, "E514", {"start": v(-0.8, 52.95) * mm, "end": v(-0.9, 53.2) * mm});
            skLineSegment(sketch, "E515", {"start": v(-0.9, 53.2) * mm, "end": v(-1.01, 53.47) * mm});
            skLineSegment(sketch, "E516", {"start": v(-1.01, 53.47) * mm, "end": v(-1.12, 53.73) * mm});
            skLineSegment(sketch, "E517", {"start": v(-1.12, 53.73) * mm, "end": v(-1.25, 54) * mm});
            skLineSegment(sketch, "E518", {"start": v(-1.25, 54) * mm, "end": v(-1.38, 54.3) * mm});
            skLineSegment(sketch, "E519", {"start": v(-1.38, 54.3) * mm, "end": v(-1.52, 54.58) * mm});
            skLineSegment(sketch, "E520", {"start": v(-1.52, 54.58) * mm, "end": v(-1.67, 54.88) * mm});
            skLineSegment(sketch, "E521", {"start": v(-1.67, 54.88) * mm, "end": v(-1.82, 55.19) * mm});
            skLineSegment(sketch, "E522", {"start": v(-1.82, 55.19) * mm, "end": v(-2, 55.5) * mm});
            skLineSegment(sketch, "E523", {"start": v(-2, 55.5) * mm, "end": v(-2.17, 55.82) * mm});
            skLineSegment(sketch, "E524", {"start": v(-2.17, 55.82) * mm, "end": v(-2.35, 56.15) * mm});
            skLineSegment(sketch, "E525", {"start": v(-2.35, 56.15) * mm, "end": v(-2.55, 56.48) * mm});
            skLineSegment(sketch, "E526", {"start": v(-2.55, 56.48) * mm, "end": v(-2.76, 56.82) * mm});
            skLineSegment(sketch, "E527", {"start": v(-2.76, 56.82) * mm, "end": v(-2.97, 57.16) * mm});
            skLineSegment(sketch, "E528", {"start": v(-2.97, 57.16) * mm, "end": v(-3.19, 57.24) * mm});
            skLineSegment(sketch, "E529", {"start": v(-3.19, 57.24) * mm, "end": v(-5.86, 57.03) * mm});
            skLineSegment(sketch, "E530", {"start": v(-5.86, 57.03) * mm, "end": v(-6.06, 56.92) * mm});
            skLineSegment(sketch, "E531", {"start": v(-6.06, 56.92) * mm, "end": v(-6.22, 56.54) * mm});
            skLineSegment(sketch, "E532", {"start": v(-6.22, 56.54) * mm, "end": v(-6.37, 56.18) * mm});
            skLineSegment(sketch, "E533", {"start": v(-6.37, 56.18) * mm, "end": v(-6.5, 55.82) * mm});
            skLineSegment(sketch, "E534", {"start": v(-6.5, 55.82) * mm, "end": v(-6.64, 55.47) * mm});
            skLineSegment(sketch, "E535", {"start": v(-6.64, 55.47) * mm, "end": v(-6.77, 55.12) * mm});
            skLineSegment(sketch, "E536", {"start": v(-6.77, 55.12) * mm, "end": v(-6.88, 54.79) * mm});
            skLineSegment(sketch, "E537", {"start": v(-6.88, 54.79) * mm, "end": v(-6.99, 54.46) * mm});
            skLineSegment(sketch, "E538", {"start": v(-6.99, 54.46) * mm, "end": v(-7.1, 54.14) * mm});
            skLineSegment(sketch, "E539", {"start": v(-7.1, 54.14) * mm, "end": v(-7.18, 53.83) * mm});
            skLineSegment(sketch, "E540", {"start": v(-7.18, 53.83) * mm, "end": v(-7.27, 53.53) * mm});
            skLineSegment(sketch, "E541", {"start": v(-7.27, 53.53) * mm, "end": v(-7.34, 53.24) * mm});
            skLineSegment(sketch, "E542", {"start": v(-7.34, 53.24) * mm, "end": v(-7.41, 52.96) * mm});
            skLineSegment(sketch, "E543", {"start": v(-7.41, 52.96) * mm, "end": v(-7.48, 52.69) * mm});
            skLineSegment(sketch, "E544", {"start": v(-7.48, 52.69) * mm, "end": v(-7.54, 52.42) * mm});
            skLineSegment(sketch, "E545", {"start": v(-7.54, 52.42) * mm, "end": v(-7.59, 52.17) * mm});
            skLineSegment(sketch, "E546", {"start": v(-7.59, 52.17) * mm, "end": v(-7.63, 51.92) * mm});
            skLineSegment(sketch, "E547", {"start": v(-7.63, 51.92) * mm, "end": v(-7.68, 51.69) * mm});
            skLineSegment(sketch, "E548", {"start": v(-7.68, 51.69) * mm, "end": v(-7.71, 51.46) * mm});
            skLineSegment(sketch, "E549", {"start": v(-7.71, 51.46) * mm, "end": v(-7.74, 51.25) * mm});
            skLineSegment(sketch, "E550", {"start": v(-7.74, 51.25) * mm, "end": v(-7.77, 51.04) * mm});
            skLineSegment(sketch, "E551", {"start": v(-7.77, 51.04) * mm, "end": v(-7.8, 50.84) * mm});
            skLineSegment(sketch, "E552", {"start": v(-7.8, 50.84) * mm, "end": v(-7.8, 50.66) * mm});
            skLineSegment(sketch, "E553", {"start": v(-7.8, 50.66) * mm, "end": v(-7.82, 50.48) * mm});
            skLineSegment(sketch, "E554", {"start": v(-7.82, 50.48) * mm, "end": v(-7.84, 50.32) * mm});
            skLineSegment(sketch, "E555", {"start": v(-7.84, 50.32) * mm, "end": v(-7.84, 50.16) * mm});
            skLineSegment(sketch, "E556", {"start": v(-7.84, 50.16) * mm, "end": v(-7.85, 50.02) * mm});
            skLineSegment(sketch, "E557", {"start": v(-7.85, 50.02) * mm, "end": v(-7.85, 49.89) * mm});
            skLineSegment(sketch, "E558", {"start": v(-7.85, 49.89) * mm, "end": v(-7.86, 49.77) * mm});
            skLineSegment(sketch, "E559", {"start": v(-7.86, 49.77) * mm, "end": v(-7.85, 49.65) * mm});
            skLineSegment(sketch, "E560", {"start": v(-7.85, 49.65) * mm, "end": v(-7.85, 49.55) * mm});
            skLineSegment(sketch, "E561", {"start": v(-7.85, 49.55) * mm, "end": v(-7.85, 49.46) * mm});
            skLineSegment(sketch, "E562", {"start": v(-7.85, 49.46) * mm, "end": v(-7.85, 49.38) * mm});
            skLineSegment(sketch, "E563", {"start": v(-7.85, 49.38) * mm, "end": v(-7.84, 49.3) * mm});
            skLineSegment(sketch, "E564", {"start": v(-7.84, 49.3) * mm, "end": v(-7.84, 49.25) * mm});
            skLineSegment(sketch, "E565", {"start": v(-7.84, 49.25) * mm, "end": v(-7.83, 49.2) * mm});
            skLineSegment(sketch, "E566", {"start": v(-7.83, 49.2) * mm, "end": v(-7.83, 49.16) * mm});
            skLineSegment(sketch, "E567", {"start": v(-7.83, 49.16) * mm, "end": v(-7.83, 49.13) * mm});
            skLineSegment(sketch, "E568", {"start": v(-7.83, 49.13) * mm, "end": v(-7.82, 49.11) * mm});
            skLineSegment(sketch, "E569", {"start": v(-7.82, 49.11) * mm, "end": v(-7.53, 47.25) * mm});
            skLineSegment(sketch, "E570", {"start": v(-7.53, 47.25) * mm, "end": v(-12.38, 46.22) * mm});
            skLineSegment(sketch, "E571", {"start": v(-12.38, 46.22) * mm, "end": v(-12.87, 48.04) * mm});
            skLineSegment(sketch, "E572", {"start": v(-12.87, 48.04) * mm, "end": v(-12.88, 48.06) * mm});
            skLineSegment(sketch, "E573", {"start": v(-12.88, 48.06) * mm, "end": v(-12.89, 48.08) * mm});
            skLineSegment(sketch, "E574", {"start": v(-12.89, 48.08) * mm, "end": v(-12.9, 48.12) * mm});
            skLineSegment(sketch, "E575", {"start": v(-12.9, 48.12) * mm, "end": v(-12.91, 48.17) * mm});
            skLineSegment(sketch, "E576", {"start": v(-12.91, 48.17) * mm, "end": v(-12.93, 48.22) * mm});
            skLineSegment(sketch, "E577", {"start": v(-12.93, 48.22) * mm, "end": v(-12.96, 48.29) * mm});
            skLineSegment(sketch, "E578", {"start": v(-12.96, 48.29) * mm, "end": v(-12.99, 48.36) * mm});
            skLineSegment(sketch, "E579", {"start": v(-12.99, 48.36) * mm, "end": v(-13.02, 48.45) * mm});
            skLineSegment(sketch, "E580", {"start": v(-13.02, 48.45) * mm, "end": v(-13.06, 48.54) * mm});
            skLineSegment(sketch, "E581", {"start": v(-13.06, 48.54) * mm, "end": v(-13.1, 48.65) * mm});
            skLineSegment(sketch, "E582", {"start": v(-13.1, 48.65) * mm, "end": v(-13.16, 48.76) * mm});
            skLineSegment(sketch, "E583", {"start": v(-13.16, 48.76) * mm, "end": v(-13.22, 48.88) * mm});
            skLineSegment(sketch, "E584", {"start": v(-13.22, 48.88) * mm, "end": v(-13.28, 49) * mm});
            skLineSegment(sketch, "E585", {"start": v(-13.28, 49) * mm, "end": v(-13.35, 49.15) * mm});
            skLineSegment(sketch, "E586", {"start": v(-13.35, 49.15) * mm, "end": v(-13.43, 49.29) * mm});
            skLineSegment(sketch, "E587", {"start": v(-13.43, 49.29) * mm, "end": v(-13.52, 49.44) * mm});
            skLineSegment(sketch, "E588", {"start": v(-13.52, 49.44) * mm, "end": v(-13.6, 49.6) * mm});
            skLineSegment(sketch, "E589", {"start": v(-13.6, 49.6) * mm, "end": v(-13.7, 49.77) * mm});
            skLineSegment(sketch, "E590", {"start": v(-13.7, 49.77) * mm, "end": v(-13.82, 49.95) * mm});
            skLineSegment(sketch, "E591", {"start": v(-13.82, 49.95) * mm, "end": v(-13.93, 50.14) * mm});
            skLineSegment(sketch, "E592", {"start": v(-13.93, 50.14) * mm, "end": v(-14.06, 50.33) * mm});
            skLineSegment(sketch, "E593", {"start": v(-14.06, 50.33) * mm, "end": v(-14.19, 50.53) * mm});
            skLineSegment(sketch, "E594", {"start": v(-14.19, 50.53) * mm, "end": v(-14.33, 50.73) * mm});
            skLineSegment(sketch, "E595", {"start": v(-14.33, 50.73) * mm, "end": v(-14.48, 50.94) * mm});
            skLineSegment(sketch, "E596", {"start": v(-14.48, 50.94) * mm, "end": v(-14.64, 51.16) * mm});
            skLineSegment(sketch, "E597", {"start": v(-14.64, 51.16) * mm, "end": v(-14.81, 51.38) * mm});
            skLineSegment(sketch, "E598", {"start": v(-14.81, 51.38) * mm, "end": v(-15, 51.61) * mm});
            skLineSegment(sketch, "E599", {"start": v(-15, 51.61) * mm, "end": v(-15.18, 51.85) * mm});
            skLineSegment(sketch, "E600", {"start": v(-15.18, 51.85) * mm, "end": v(-15.38, 52.09) * mm});
            skLineSegment(sketch, "E601", {"start": v(-15.38, 52.09) * mm, "end": v(-15.6, 52.33) * mm});
            skLineSegment(sketch, "E602", {"start": v(-15.6, 52.33) * mm, "end": v(-15.81, 52.58) * mm});
            skLineSegment(sketch, "E603", {"start": v(-15.81, 52.58) * mm, "end": v(-16.04, 52.84) * mm});
            skLineSegment(sketch, "E604", {"start": v(-16.04, 52.84) * mm, "end": v(-16.29, 53.1) * mm});
            skLineSegment(sketch, "E605", {"start": v(-16.29, 53.1) * mm, "end": v(-16.54, 53.36) * mm});
            skLineSegment(sketch, "E606", {"start": v(-16.54, 53.36) * mm, "end": v(-16.8, 53.63) * mm});
            skLineSegment(sketch, "E607", {"start": v(-16.8, 53.63) * mm, "end": v(-17.08, 53.9) * mm});
            skLineSegment(sketch, "E608", {"start": v(-17.08, 53.9) * mm, "end": v(-17.37, 54.17) * mm});
            skLineSegment(sketch, "E609", {"start": v(-17.37, 54.17) * mm, "end": v(-17.67, 54.44) * mm});
            skLineSegment(sketch, "E610", {"start": v(-17.67, 54.44) * mm, "end": v(-17.9, 54.46) * mm});
            skLineSegment(sketch, "E611", {"start": v(-17.9, 54.46) * mm, "end": v(-20.42, 53.57) * mm});
            skLineSegment(sketch, "E612", {"start": v(-20.42, 53.57) * mm, "end": v(-20.58, 53.41) * mm});
            skLineSegment(sketch, "E613", {"start": v(-20.58, 53.41) * mm, "end": v(-20.64, 53) * mm});
            skLineSegment(sketch, "E614", {"start": v(-20.64, 53) * mm, "end": v(-20.7, 52.61) * mm});
            skLineSegment(sketch, "E615", {"start": v(-20.7, 52.61) * mm, "end": v(-20.74, 52.23) * mm});
            skLineSegment(sketch, "E616", {"start": v(-20.74, 52.23) * mm, "end": v(-20.77, 51.86) * mm});
            skLineSegment(sketch, "E617", {"start": v(-20.77, 51.86) * mm, "end": v(-20.8, 51.5) * mm});
            skLineSegment(sketch, "E618", {"start": v(-20.8, 51.5) * mm, "end": v(-20.83, 51.14) * mm});
            skLineSegment(sketch, "E619", {"start": v(-20.83, 51.14) * mm, "end": v(-20.85, 50.8) * mm});
            skLineSegment(sketch, "E620", {"start": v(-20.85, 50.8) * mm, "end": v(-20.86, 50.46) * mm});
            skLineSegment(sketch, "E621", {"start": v(-20.86, 50.46) * mm, "end": v(-20.87, 50.14) * mm});
            skLineSegment(sketch, "E622", {"start": v(-20.87, 50.14) * mm, "end": v(-20.87, 49.83) * mm});
            skLineSegment(sketch, "E623", {"start": v(-20.87, 49.83) * mm, "end": v(-20.87, 49.53) * mm});
            skLineSegment(sketch, "E624", {"start": v(-20.87, 49.53) * mm, "end": v(-20.87, 49.24) * mm});
            skLineSegment(sketch, "E625", {"start": v(-20.87, 49.24) * mm, "end": v(-20.86, 48.96) * mm});
            skLineSegment(sketch, "E626", {"start": v(-20.86, 48.96) * mm, "end": v(-20.85, 48.68) * mm});
            skLineSegment(sketch, "E627", {"start": v(-20.85, 48.68) * mm, "end": v(-20.83, 48.43) * mm});
            skLineSegment(sketch, "E628", {"start": v(-20.83, 48.43) * mm, "end": v(-20.81, 48.18) * mm});
            skLineSegment(sketch, "E629", {"start": v(-20.81, 48.18) * mm, "end": v(-20.8, 47.94) * mm});
            skLineSegment(sketch, "E630", {"start": v(-20.8, 47.94) * mm, "end": v(-20.77, 47.71) * mm});
            skLineSegment(sketch, "E631", {"start": v(-20.77, 47.71) * mm, "end": v(-20.74, 47.5) * mm});
            skLineSegment(sketch, "E632", {"start": v(-20.74, 47.5) * mm, "end": v(-20.71, 47.3) * mm});
            skLineSegment(sketch, "E633", {"start": v(-20.71, 47.3) * mm, "end": v(-20.69, 47.1) * mm});
            skLineSegment(sketch, "E634", {"start": v(-20.69, 47.1) * mm, "end": v(-20.66, 46.91) * mm});
            skLineSegment(sketch, "E635", {"start": v(-20.66, 46.91) * mm, "end": v(-20.62, 46.74) * mm});
            skLineSegment(sketch, "E636", {"start": v(-20.62, 46.74) * mm, "end": v(-20.6, 46.58) * mm});
            skLineSegment(sketch, "E637", {"start": v(-20.6, 46.58) * mm, "end": v(-20.56, 46.43) * mm});
            skLineSegment(sketch, "E638", {"start": v(-20.56, 46.43) * mm, "end": v(-20.53, 46.29) * mm});
            skLineSegment(sketch, "E639", {"start": v(-20.53, 46.29) * mm, "end": v(-20.5, 46.15) * mm});
            skLineSegment(sketch, "E640", {"start": v(-20.5, 46.15) * mm, "end": v(-20.47, 46.04) * mm});
            skLineSegment(sketch, "E641", {"start": v(-20.47, 46.04) * mm, "end": v(-20.44, 45.93) * mm});
            skLineSegment(sketch, "E642", {"start": v(-20.44, 45.93) * mm, "end": v(-20.41, 45.83) * mm});
            skLineSegment(sketch, "E643", {"start": v(-20.41, 45.83) * mm, "end": v(-20.38, 45.74) * mm});
            skLineSegment(sketch, "E644", {"start": v(-20.38, 45.74) * mm, "end": v(-20.36, 45.66) * mm});
            skLineSegment(sketch, "E645", {"start": v(-20.36, 45.66) * mm, "end": v(-20.34, 45.6) * mm});
            skLineSegment(sketch, "E646", {"start": v(-20.34, 45.6) * mm, "end": v(-20.32, 45.54) * mm});
            skLineSegment(sketch, "E647", {"start": v(-20.32, 45.54) * mm, "end": v(-20.3, 45.5) * mm});
            skLineSegment(sketch, "E648", {"start": v(-20.3, 45.5) * mm, "end": v(-20.29, 45.46) * mm});
            skLineSegment(sketch, "E649", {"start": v(-20.29, 45.46) * mm, "end": v(-20.28, 45.43) * mm});
            skLineSegment(sketch, "E650", {"start": v(-20.28, 45.43) * mm, "end": v(-20.27, 45.41) * mm});
            skLineSegment(sketch, "E651", {"start": v(-20.27, 45.41) * mm, "end": v(-19.5, 43.7) * mm});
            skLineSegment(sketch, "E652", {"start": v(-19.5, 43.7) * mm, "end": v(-23.92, 41.43) * mm});
            skLineSegment(sketch, "E653", {"start": v(-23.92, 41.43) * mm, "end": v(-24.87, 43.07) * mm});
            skLineSegment(sketch, "E654", {"start": v(-24.87, 43.07) * mm, "end": v(-24.88, 43.09) * mm});
            skLineSegment(sketch, "E655", {"start": v(-24.88, 43.09) * mm, "end": v(-24.9, 43.1) * mm});
            skLineSegment(sketch, "E656", {"start": v(-24.9, 43.1) * mm, "end": v(-24.91, 43.14) * mm});
            skLineSegment(sketch, "E657", {"start": v(-24.91, 43.14) * mm, "end": v(-24.94, 43.18) * mm});
            skLineSegment(sketch, "E658", {"start": v(-24.94, 43.18) * mm, "end": v(-24.97, 43.23) * mm});
            skLineSegment(sketch, "E659", {"start": v(-24.97, 43.23) * mm, "end": v(-25.02, 43.29) * mm});
            skLineSegment(sketch, "E660", {"start": v(-25.02, 43.29) * mm, "end": v(-25.06, 43.35) * mm});
            skLineSegment(sketch, "E661", {"start": v(-25.06, 43.35) * mm, "end": v(-25.12, 43.43) * mm});
            skLineSegment(sketch, "E662", {"start": v(-25.12, 43.43) * mm, "end": v(-25.18, 43.5) * mm});
            skLineSegment(sketch, "E663", {"start": v(-25.18, 43.5) * mm, "end": v(-25.25, 43.6) * mm});
            skLineSegment(sketch, "E664", {"start": v(-25.25, 43.6) * mm, "end": v(-25.33, 43.69) * mm});
            skLineSegment(sketch, "E665", {"start": v(-25.33, 43.69) * mm, "end": v(-25.42, 43.8) * mm});
            skLineSegment(sketch, "E666", {"start": v(-25.42, 43.8) * mm, "end": v(-25.51, 43.9) * mm});
            skLineSegment(sketch, "E667", {"start": v(-25.51, 43.9) * mm, "end": v(-25.62, 44.01) * mm});
            skLineSegment(sketch, "E668", {"start": v(-25.62, 44.01) * mm, "end": v(-25.73, 44.13) * mm});
            skLineSegment(sketch, "E669", {"start": v(-25.73, 44.13) * mm, "end": v(-25.85, 44.26) * mm});
            skLineSegment(sketch, "E670", {"start": v(-25.85, 44.26) * mm, "end": v(-25.98, 44.4) * mm});
            skLineSegment(sketch, "E671", {"start": v(-25.98, 44.4) * mm, "end": v(-26.12, 44.53) * mm});
            skLineSegment(sketch, "E672", {"start": v(-26.12, 44.53) * mm, "end": v(-26.27, 44.67) * mm});
            skLineSegment(sketch, "E673", {"start": v(-26.27, 44.67) * mm, "end": v(-26.43, 44.82) * mm});
            skLineSegment(sketch, "E674", {"start": v(-26.43, 44.82) * mm, "end": v(-26.6, 44.97) * mm});
            skLineSegment(sketch, "E675", {"start": v(-26.6, 44.97) * mm, "end": v(-26.78, 45.13) * mm});
            skLineSegment(sketch, "E676", {"start": v(-26.78, 45.13) * mm, "end": v(-26.97, 45.3) * mm});
            skLineSegment(sketch, "E677", {"start": v(-26.97, 45.3) * mm, "end": v(-27.17, 45.46) * mm});
            skLineSegment(sketch, "E678", {"start": v(-27.17, 45.46) * mm, "end": v(-27.39, 45.63) * mm});
            skLineSegment(sketch, "E679", {"start": v(-27.39, 45.63) * mm, "end": v(-27.6, 45.8) * mm});
            skLineSegment(sketch, "E680", {"start": v(-27.6, 45.8) * mm, "end": v(-27.84, 45.97) * mm});
            skLineSegment(sketch, "E681", {"start": v(-27.84, 45.97) * mm, "end": v(-28.08, 46.15) * mm});
            skLineSegment(sketch, "E682", {"start": v(-28.08, 46.15) * mm, "end": v(-28.34, 46.33) * mm});
            skLineSegment(sketch, "E683", {"start": v(-28.34, 46.33) * mm, "end": v(-28.6, 46.51) * mm});
            skLineSegment(sketch, "E684", {"start": v(-28.6, 46.51) * mm, "end": v(-28.88, 46.7) * mm});
            skLineSegment(sketch, "E685", {"start": v(-28.88, 46.7) * mm, "end": v(-29.17, 46.88) * mm});
            skLineSegment(sketch, "E686", {"start": v(-29.17, 46.88) * mm, "end": v(-29.47, 47.07) * mm});
            skLineSegment(sketch, "E687", {"start": v(-29.47, 47.07) * mm, "end": v(-29.79, 47.26) * mm});
            skLineSegment(sketch, "E688", {"start": v(-29.79, 47.26) * mm, "end": v(-30.11, 47.45) * mm});
            skLineSegment(sketch, "E689", {"start": v(-30.11, 47.45) * mm, "end": v(-30.45, 47.64) * mm});
            skLineSegment(sketch, "E690", {"start": v(-30.45, 47.64) * mm, "end": v(-30.8, 47.83) * mm});
            skLineSegment(sketch, "E691", {"start": v(-30.8, 47.83) * mm, "end": v(-31.16, 48.02) * mm});
            skLineSegment(sketch, "E692", {"start": v(-31.16, 48.02) * mm, "end": v(-31.38, 47.98) * mm});
            skLineSegment(sketch, "E693", {"start": v(-31.38, 47.98) * mm, "end": v(-33.59, 46.46) * mm});
            skLineSegment(sketch, "E694", {"start": v(-33.59, 46.46) * mm, "end": v(-33.7, 46.26) * mm});
            skLineSegment(sketch, "E695", {"start": v(-33.7, 46.26) * mm, "end": v(-33.66, 45.86) * mm});
            skLineSegment(sketch, "E696", {"start": v(-33.66, 45.86) * mm, "end": v(-33.6, 45.47) * mm});
            skLineSegment(sketch, "E697", {"start": v(-33.6, 45.47) * mm, "end": v(-33.55, 45.09) * mm});
            skLineSegment(sketch, "E698", {"start": v(-33.55, 45.09) * mm, "end": v(-33.49, 44.71) * mm});
            skLineSegment(sketch, "E699", {"start": v(-33.49, 44.71) * mm, "end": v(-33.42, 44.35) * mm});
            skLineSegment(sketch, "E700", {"start": v(-33.42, 44.35) * mm, "end": v(-33.35, 44) * mm});
            skLineSegment(sketch, "E701", {"start": v(-33.35, 44) * mm, "end": v(-33.28, 43.67) * mm});
            skLineSegment(sketch, "E702", {"start": v(-33.28, 43.67) * mm, "end": v(-33.21, 43.34) * mm});
            skLineSegment(sketch, "E703", {"start": v(-33.21, 43.34) * mm, "end": v(-33.14, 43.03) * mm});
            skLineSegment(sketch, "E704", {"start": v(-33.14, 43.03) * mm, "end": v(-33.06, 42.73) * mm});
            skLineSegment(sketch, "E705", {"start": v(-33.06, 42.73) * mm, "end": v(-32.98, 42.44) * mm});
            skLineSegment(sketch, "E706", {"start": v(-32.98, 42.44) * mm, "end": v(-32.9, 42.16) * mm});
            skLineSegment(sketch, "E707", {"start": v(-32.9, 42.16) * mm, "end": v(-32.82, 41.89) * mm});
            skLineSegment(sketch, "E708", {"start": v(-32.82, 41.89) * mm, "end": v(-32.74, 41.63) * mm});
            skLineSegment(sketch, "E709", {"start": v(-32.74, 41.63) * mm, "end": v(-32.65, 41.38) * mm});
            skLineSegment(sketch, "E710", {"start": v(-32.65, 41.38) * mm, "end": v(-32.57, 41.15) * mm});
            skLineSegment(sketch, "E711", {"start": v(-32.57, 41.15) * mm, "end": v(-32.5, 40.92) * mm});
            skLineSegment(sketch, "E712", {"start": v(-32.5, 40.92) * mm, "end": v(-32.4, 40.71) * mm});
            skLineSegment(sketch, "E713", {"start": v(-32.4, 40.71) * mm, "end": v(-32.33, 40.5) * mm});
            skLineSegment(sketch, "E714", {"start": v(-32.33, 40.5) * mm, "end": v(-32.25, 40.32) * mm});
            skLineSegment(sketch, "E715", {"start": v(-32.25, 40.32) * mm, "end": v(-32.17, 40.14) * mm});
            skLineSegment(sketch, "E716", {"start": v(-32.17, 40.14) * mm, "end": v(-32.1, 39.97) * mm});
            skLineSegment(sketch, "E717", {"start": v(-32.1, 39.97) * mm, "end": v(-32.02, 39.8) * mm});
            skLineSegment(sketch, "E718", {"start": v(-32.02, 39.8) * mm, "end": v(-31.95, 39.66) * mm});
            skLineSegment(sketch, "E719", {"start": v(-31.95, 39.66) * mm, "end": v(-31.88, 39.52) * mm});
            skLineSegment(sketch, "E720", {"start": v(-31.88, 39.52) * mm, "end": v(-31.8, 39.4) * mm});
            skLineSegment(sketch, "E721", {"start": v(-31.8, 39.4) * mm, "end": v(-31.75, 39.28) * mm});
            skLineSegment(sketch, "E722", {"start": v(-31.75, 39.28) * mm, "end": v(-31.69, 39.17) * mm});
            skLineSegment(sketch, "E723", {"start": v(-31.69, 39.17) * mm, "end": v(-31.63, 39.07) * mm});
            skLineSegment(sketch, "E724", {"start": v(-31.63, 39.07) * mm, "end": v(-31.58, 38.98) * mm});
            skLineSegment(sketch, "E725", {"start": v(-31.58, 38.98) * mm, "end": v(-31.53, 38.9) * mm});
            skLineSegment(sketch, "E726", {"start": v(-31.53, 38.9) * mm, "end": v(-31.48, 38.84) * mm});
            skLineSegment(sketch, "E727", {"start": v(-31.48, 38.84) * mm, "end": v(-31.45, 38.78) * mm});
            skLineSegment(sketch, "E728", {"start": v(-31.45, 38.78) * mm, "end": v(-31.41, 38.73) * mm});
            skLineSegment(sketch, "E729", {"start": v(-31.41, 38.73) * mm, "end": v(-31.38, 38.69) * mm});
            skLineSegment(sketch, "E730", {"start": v(-31.38, 38.69) * mm, "end": v(-31.36, 38.66) * mm});
            skLineSegment(sketch, "E731", {"start": v(-31.36, 38.66) * mm, "end": v(-31.34, 38.64) * mm});
            skLineSegment(sketch, "E732", {"start": v(-31.34, 38.64) * mm, "end": v(-31.33, 38.62) * mm});
            skLineSegment(sketch, "E733", {"start": v(-31.33, 38.62) * mm, "end": v(-30.14, 37.16) * mm});
            skLineSegment(sketch, "E734", {"start": v(-30.14, 37.16) * mm, "end": v(-33.83, 33.83) * mm});
            skLineSegment(sketch, "E735", {"start": v(-33.83, 33.83) * mm, "end": v(-35.17, 35.17) * mm});
            skLineSegment(sketch, "E736", {"start": v(-35.17, 35.17) * mm, "end": v(-35.18, 35.18) * mm});
            skLineSegment(sketch, "E737", {"start": v(-35.18, 35.18) * mm, "end": v(-35.2, 35.2) * mm});
            skLineSegment(sketch, "E738", {"start": v(-35.2, 35.2) * mm, "end": v(-35.23, 35.22) * mm});
            skLineSegment(sketch, "E739", {"start": v(-35.23, 35.22) * mm, "end": v(-35.27, 35.26) * mm});
            skLineSegment(sketch, "E740", {"start": v(-35.27, 35.26) * mm, "end": v(-35.31, 35.3) * mm});
            skLineSegment(sketch, "E741", {"start": v(-35.31, 35.3) * mm, "end": v(-35.37, 35.34) * mm});
            skLineSegment(sketch, "E742", {"start": v(-35.37, 35.34) * mm, "end": v(-35.43, 35.4) * mm});
            skLineSegment(sketch, "E743", {"start": v(-35.43, 35.4) * mm, "end": v(-35.5, 35.45) * mm});
            skLineSegment(sketch, "E744", {"start": v(-35.5, 35.45) * mm, "end": v(-35.58, 35.5) * mm});
            skLineSegment(sketch, "E745", {"start": v(-35.58, 35.5) * mm, "end": v(-35.67, 35.57) * mm});
            skLineSegment(sketch, "E746", {"start": v(-35.67, 35.57) * mm, "end": v(-35.78, 35.65) * mm});
            skLineSegment(sketch, "E747", {"start": v(-35.78, 35.65) * mm, "end": v(-35.89, 35.72) * mm});
            skLineSegment(sketch, "E748", {"start": v(-35.89, 35.72) * mm, "end": v(-36, 35.8) * mm});
            skLineSegment(sketch, "E749", {"start": v(-36, 35.8) * mm, "end": v(-36.14, 35.88) * mm});
            skLineSegment(sketch, "E750", {"start": v(-36.14, 35.88) * mm, "end": v(-36.28, 35.97) * mm});
            skLineSegment(sketch, "E751", {"start": v(-36.28, 35.97) * mm, "end": v(-36.43, 36.06) * mm});
            skLineSegment(sketch, "E752", {"start": v(-36.43, 36.06) * mm, "end": v(-36.59, 36.16) * mm});
            skLineSegment(sketch, "E753", {"start": v(-36.59, 36.16) * mm, "end": v(-36.76, 36.25) * mm});
            skLineSegment(sketch, "E754", {"start": v(-36.76, 36.25) * mm, "end": v(-36.94, 36.35) * mm});
            skLineSegment(sketch, "E755", {"start": v(-36.94, 36.35) * mm, "end": v(-37.13, 36.45) * mm});
            skLineSegment(sketch, "E756", {"start": v(-37.13, 36.45) * mm, "end": v(-37.34, 36.56) * mm});
            skLineSegment(sketch, "E757", {"start": v(-37.34, 36.56) * mm, "end": v(-37.55, 36.66) * mm});
            skLineSegment(sketch, "E758", {"start": v(-37.55, 36.66) * mm, "end": v(-37.78, 36.77) * mm});
            skLineSegment(sketch, "E759", {"start": v(-37.78, 36.77) * mm, "end": v(-38.01, 36.87) * mm});
            skLineSegment(sketch, "E760", {"start": v(-38.01, 36.87) * mm, "end": v(-38.26, 36.98) * mm});
            skLineSegment(sketch, "E761", {"start": v(-38.26, 36.98) * mm, "end": v(-38.52, 37.1) * mm});
            skLineSegment(sketch, "E762", {"start": v(-38.52, 37.1) * mm, "end": v(-38.8, 37.2) * mm});
            skLineSegment(sketch, "E763", {"start": v(-38.8, 37.2) * mm, "end": v(-39.07, 37.3) * mm});
            skLineSegment(sketch, "E764", {"start": v(-39.07, 37.3) * mm, "end": v(-39.37, 37.42) * mm});
            skLineSegment(sketch, "E765", {"start": v(-39.37, 37.42) * mm, "end": v(-39.67, 37.52) * mm});
            skLineSegment(sketch, "E766", {"start": v(-39.67, 37.52) * mm, "end": v(-39.99, 37.63) * mm});
            skLineSegment(sketch, "E767", {"start": v(-39.99, 37.63) * mm, "end": v(-40.31, 37.73) * mm});
            skLineSegment(sketch, "E768", {"start": v(-40.31, 37.73) * mm, "end": v(-40.65, 37.84) * mm});
            skLineSegment(sketch, "E769", {"start": v(-40.65, 37.84) * mm, "end": v(-41, 37.94) * mm});
            skLineSegment(sketch, "E770", {"start": v(-41, 37.94) * mm, "end": v(-41.37, 38.04) * mm});
            skLineSegment(sketch, "E771", {"start": v(-41.37, 38.04) * mm, "end": v(-41.74, 38.13) * mm});
            skLineSegment(sketch, "E772", {"start": v(-41.74, 38.13) * mm, "end": v(-42.13, 38.23) * mm});
            skLineSegment(sketch, "E773", {"start": v(-42.13, 38.23) * mm, "end": v(-42.52, 38.32) * mm});
            skLineSegment(sketch, "E774", {"start": v(-42.52, 38.32) * mm, "end": v(-42.73, 38.22) * mm});
            skLineSegment(sketch, "E775", {"start": v(-42.73, 38.22) * mm, "end": v(-44.47, 36.18) * mm});
            skLineSegment(sketch, "E776", {"start": v(-44.47, 36.18) * mm, "end": v(-44.53, 35.96) * mm});
            skLineSegment(sketch, "E777", {"start": v(-44.53, 35.96) * mm, "end": v(-44.38, 35.59) * mm});
            skLineSegment(sketch, "E778", {"start": v(-44.38, 35.59) * mm, "end": v(-44.23, 35.22) * mm});
            skLineSegment(sketch, "E779", {"start": v(-44.23, 35.22) * mm, "end": v(-44.07, 34.87) * mm});
            skLineSegment(sketch, "E780", {"start": v(-44.07, 34.87) * mm, "end": v(-43.92, 34.52) * mm});
            skLineSegment(sketch, "E781", {"start": v(-43.92, 34.52) * mm, "end": v(-43.76, 34.2) * mm});
            skLineSegment(sketch, "E782", {"start": v(-43.76, 34.2) * mm, "end": v(-43.6, 33.87) * mm});
            skLineSegment(sketch, "E783", {"start": v(-43.6, 33.87) * mm, "end": v(-43.45, 33.57) * mm});
            skLineSegment(sketch, "E784", {"start": v(-43.45, 33.57) * mm, "end": v(-43.3, 33.27) * mm});
            skLineSegment(sketch, "E785", {"start": v(-43.3, 33.27) * mm, "end": v(-43.14, 32.99) * mm});
            skLineSegment(sketch, "E786", {"start": v(-43.14, 32.99) * mm, "end": v(-43, 32.72) * mm});
            skLineSegment(sketch, "E787", {"start": v(-43, 32.72) * mm, "end": v(-42.84, 32.46) * mm});
            skLineSegment(sketch, "E788", {"start": v(-42.84, 32.46) * mm, "end": v(-42.7, 32.2) * mm});
            skLineSegment(sketch, "E789", {"start": v(-42.7, 32.2) * mm, "end": v(-42.54, 31.97) * mm});
            skLineSegment(sketch, "E790", {"start": v(-42.54, 31.97) * mm, "end": v(-42.4, 31.74) * mm});
            skLineSegment(sketch, "E791", {"start": v(-42.4, 31.74) * mm, "end": v(-42.25, 31.52) * mm});
            skLineSegment(sketch, "E792", {"start": v(-42.25, 31.52) * mm, "end": v(-42.11, 31.32) * mm});
            skLineSegment(sketch, "E793", {"start": v(-42.11, 31.32) * mm, "end": v(-41.98, 31.12) * mm});
            skLineSegment(sketch, "E794", {"start": v(-41.98, 31.12) * mm, "end": v(-41.84, 30.94) * mm});
            skLineSegment(sketch, "E795", {"start": v(-41.84, 30.94) * mm, "end": v(-41.71, 30.76) * mm});
            skLineSegment(sketch, "E796", {"start": v(-41.71, 30.76) * mm, "end": v(-41.58, 30.6) * mm});
            skLineSegment(sketch, "E797", {"start": v(-41.58, 30.6) * mm, "end": v(-41.46, 30.44) * mm});
            skLineSegment(sketch, "E798", {"start": v(-41.46, 30.44) * mm, "end": v(-41.34, 30.3) * mm});
            skLineSegment(sketch, "E799", {"start": v(-41.34, 30.3) * mm, "end": v(-41.23, 30.17) * mm});
            skLineSegment(sketch, "E800", {"start": v(-41.23, 30.17) * mm, "end": v(-41.12, 30.04) * mm});
            skLineSegment(sketch, "E801", {"start": v(-41.12, 30.04) * mm, "end": v(-41.02, 29.93) * mm});
            skLineSegment(sketch, "E802", {"start": v(-41.02, 29.93) * mm, "end": v(-40.92, 29.82) * mm});
            skLineSegment(sketch, "E803", {"start": v(-40.92, 29.82) * mm, "end": v(-40.83, 29.72) * mm});
            skLineSegment(sketch, "E804", {"start": v(-40.83, 29.72) * mm, "end": v(-40.74, 29.63) * mm});
            skLineSegment(sketch, "E805", {"start": v(-40.74, 29.63) * mm, "end": v(-40.66, 29.55) * mm});
            skLineSegment(sketch, "E806", {"start": v(-40.66, 29.55) * mm, "end": v(-40.6, 29.48) * mm});
            skLineSegment(sketch, "E807", {"start": v(-40.6, 29.48) * mm, "end": v(-40.52, 29.42) * mm});
            skLineSegment(sketch, "E808", {"start": v(-40.52, 29.42) * mm, "end": v(-40.46, 29.37) * mm});
            skLineSegment(sketch, "E809", {"start": v(-40.46, 29.37) * mm, "end": v(-40.41, 29.32) * mm});
            skLineSegment(sketch, "E810", {"start": v(-40.41, 29.32) * mm, "end": v(-40.37, 29.28) * mm});
            skLineSegment(sketch, "E811", {"start": v(-40.37, 29.28) * mm, "end": v(-40.33, 29.25) * mm});
            skLineSegment(sketch, "E812", {"start": v(-40.33, 29.25) * mm, "end": v(-40.3, 29.22) * mm});
            skLineSegment(sketch, "E813", {"start": v(-40.3, 29.22) * mm, "end": v(-40.28, 29.2) * mm});
            skLineSegment(sketch, "E814", {"start": v(-40.28, 29.2) * mm, "end": v(-40.26, 29.2) * mm});
            skLineSegment(sketch, "E815", {"start": v(-40.26, 29.2) * mm, "end": v(-38.73, 28.09) * mm});
            skLineSegment(sketch, "E816", {"start": v(-38.73, 28.09) * mm, "end": v(-41.43, 23.92) * mm});
            skLineSegment(sketch, "E817", {"start": v(-41.43, 23.92) * mm, "end": v(-43.07, 24.87) * mm});
            skLineSegment(sketch, "E818", {"start": v(-43.07, 24.87) * mm, "end": v(-43.09, 24.88) * mm});
            skLineSegment(sketch, "E819", {"start": v(-43.09, 24.88) * mm, "end": v(-43.11, 24.89) * mm});
            skLineSegment(sketch, "E820", {"start": v(-43.11, 24.89) * mm, "end": v(-43.15, 24.9) * mm});
            skLineSegment(sketch, "E821", {"start": v(-43.15, 24.9) * mm, "end": v(-43.2, 24.93) * mm});
            skLineSegment(sketch, "E822", {"start": v(-43.2, 24.93) * mm, "end": v(-43.24, 24.95) * mm});
            skLineSegment(sketch, "E823", {"start": v(-43.24, 24.95) * mm, "end": v(-43.3, 24.98) * mm});
            skLineSegment(sketch, "E824", {"start": v(-43.3, 24.98) * mm, "end": v(-43.38, 25.01) * mm});
            skLineSegment(sketch, "E825", {"start": v(-43.38, 25.01) * mm, "end": v(-43.47, 25.05) * mm});
            skLineSegment(sketch, "E826", {"start": v(-43.47, 25.05) * mm, "end": v(-43.56, 25.09) * mm});
            skLineSegment(sketch, "E827", {"start": v(-43.56, 25.09) * mm, "end": v(-43.67, 25.13) * mm});
            skLineSegment(sketch, "E828", {"start": v(-43.67, 25.13) * mm, "end": v(-43.78, 25.17) * mm});
            skLineSegment(sketch, "E829", {"start": v(-43.78, 25.17) * mm, "end": v(-43.9, 25.22) * mm});
            skLineSegment(sketch, "E830", {"start": v(-43.9, 25.22) * mm, "end": v(-44.04, 25.26) * mm});
            skLineSegment(sketch, "E831", {"start": v(-44.04, 25.26) * mm, "end": v(-44.2, 25.3) * mm});
            skLineSegment(sketch, "E832", {"start": v(-44.2, 25.3) * mm, "end": v(-44.35, 25.36) * mm});
            skLineSegment(sketch, "E833", {"start": v(-44.35, 25.36) * mm, "end": v(-44.52, 25.4) * mm});
            skLineSegment(sketch, "E834", {"start": v(-44.52, 25.4) * mm, "end": v(-44.7, 25.45) * mm});
            skLineSegment(sketch, "E835", {"start": v(-44.7, 25.45) * mm, "end": v(-44.89, 25.5) * mm});
            skLineSegment(sketch, "E836", {"start": v(-44.89, 25.5) * mm, "end": v(-45.1, 25.55) * mm});
            skLineSegment(sketch, "E837", {"start": v(-45.1, 25.55) * mm, "end": v(-45.3, 25.6) * mm});
            skLineSegment(sketch, "E838", {"start": v(-45.3, 25.6) * mm, "end": v(-45.53, 25.65) * mm});
            skLineSegment(sketch, "E839", {"start": v(-45.53, 25.65) * mm, "end": v(-45.76, 25.7) * mm});
            skLineSegment(sketch, "E840", {"start": v(-45.76, 25.7) * mm, "end": v(-46, 25.74) * mm});
            skLineSegment(sketch, "E841", {"start": v(-46, 25.74) * mm, "end": v(-46.26, 25.78) * mm});
            skLineSegment(sketch, "E842", {"start": v(-46.26, 25.78) * mm, "end": v(-46.53, 25.82) * mm});
            skLineSegment(sketch, "E843", {"start": v(-46.53, 25.82) * mm, "end": v(-46.8, 25.86) * mm});
            skLineSegment(sketch, "E844", {"start": v(-46.8, 25.86) * mm, "end": v(-47.1, 25.9) * mm});
            skLineSegment(sketch, "E845", {"start": v(-47.1, 25.9) * mm, "end": v(-47.4, 25.92) * mm});
            skLineSegment(sketch, "E846", {"start": v(-47.4, 25.92) * mm, "end": v(-47.7, 25.95) * mm});
            skLineSegment(sketch, "E847", {"start": v(-47.7, 25.95) * mm, "end": v(-48.03, 25.98) * mm});
            skLineSegment(sketch, "E848", {"start": v(-48.03, 25.98) * mm, "end": v(-48.36, 26) * mm});
            skLineSegment(sketch, "E849", {"start": v(-48.36, 26) * mm, "end": v(-48.7, 26.02) * mm});
            skLineSegment(sketch, "E850", {"start": v(-48.7, 26.02) * mm, "end": v(-49.06, 26.03) * mm});
            skLineSegment(sketch, "E851", {"start": v(-49.06, 26.03) * mm, "end": v(-49.43, 26.03) * mm});
            skLineSegment(sketch, "E852", {"start": v(-49.43, 26.03) * mm, "end": v(-49.8, 26.04) * mm});
            skLineSegment(sketch, "E853", {"start": v(-49.8, 26.04) * mm, "end": v(-50.19, 26.03) * mm});
            skLineSegment(sketch, "E854", {"start": v(-50.19, 26.03) * mm, "end": v(-50.58, 26.02) * mm});
            skLineSegment(sketch, "E855", {"start": v(-50.58, 26.02) * mm, "end": v(-51, 26) * mm});
            skLineSegment(sketch, "E856", {"start": v(-51, 26) * mm, "end": v(-51.16, 25.86) * mm});
            skLineSegment(sketch, "E857", {"start": v(-51.16, 25.86) * mm, "end": v(-52.32, 23.44) * mm});
            skLineSegment(sketch, "E858", {"start": v(-52.32, 23.44) * mm, "end": v(-52.32, 23.21) * mm});
            skLineSegment(sketch, "E859", {"start": v(-52.32, 23.21) * mm, "end": v(-52.08, 22.89) * mm});
            skLineSegment(sketch, "E860", {"start": v(-52.08, 22.89) * mm, "end": v(-51.83, 22.57) * mm});
            skLineSegment(sketch, "E861", {"start": v(-51.83, 22.57) * mm, "end": v(-51.6, 22.27) * mm});
            skLineSegment(sketch, "E862", {"start": v(-51.6, 22.27) * mm, "end": v(-51.36, 21.98) * mm});
            skLineSegment(sketch, "E863", {"start": v(-51.36, 21.98) * mm, "end": v(-51.12, 21.7) * mm});
            skLineSegment(sketch, "E864", {"start": v(-51.12, 21.7) * mm, "end": v(-50.89, 21.43) * mm});
            skLineSegment(sketch, "E865", {"start": v(-50.89, 21.43) * mm, "end": v(-50.66, 21.18) * mm});
            skLineSegment(sketch, "E866", {"start": v(-50.66, 21.18) * mm, "end": v(-50.43, 20.93) * mm});
            skLineSegment(sketch, "E867", {"start": v(-50.43, 20.93) * mm, "end": v(-50.21, 20.7) * mm});
            skLineSegment(sketch, "E868", {"start": v(-50.21, 20.7) * mm, "end": v(-50, 20.47) * mm});
            skLineSegment(sketch, "E869", {"start": v(-50, 20.47) * mm, "end": v(-49.78, 20.26) * mm});
            skLineSegment(sketch, "E870", {"start": v(-49.78, 20.26) * mm, "end": v(-49.57, 20.06) * mm});
            skLineSegment(sketch, "E871", {"start": v(-49.57, 20.06) * mm, "end": v(-49.37, 19.87) * mm});
            skLineSegment(sketch, "E872", {"start": v(-49.37, 19.87) * mm, "end": v(-49.17, 19.68) * mm});
            skLineSegment(sketch, "E873", {"start": v(-49.17, 19.68) * mm, "end": v(-48.97, 19.51) * mm});
            skLineSegment(sketch, "E874", {"start": v(-48.97, 19.51) * mm, "end": v(-48.78, 19.35) * mm});
            skLineSegment(sketch, "E875", {"start": v(-48.78, 19.35) * mm, "end": v(-48.6, 19.2) * mm});
            skLineSegment(sketch, "E876", {"start": v(-48.6, 19.2) * mm, "end": v(-48.42, 19.05) * mm});
            skLineSegment(sketch, "E877", {"start": v(-48.42, 19.05) * mm, "end": v(-48.25, 18.92) * mm});
            skLineSegment(sketch, "E878", {"start": v(-48.25, 18.92) * mm, "end": v(-48.09, 18.8) * mm});
            skLineSegment(sketch, "E879", {"start": v(-48.09, 18.8) * mm, "end": v(-47.93, 18.68) * mm});
            skLineSegment(sketch, "E880", {"start": v(-47.93, 18.68) * mm, "end": v(-47.78, 18.57) * mm});
            skLineSegment(sketch, "E881", {"start": v(-47.78, 18.57) * mm, "end": v(-47.63, 18.47) * mm});
            skLineSegment(sketch, "E882", {"start": v(-47.63, 18.47) * mm, "end": v(-47.5, 18.37) * mm});
            skLineSegment(sketch, "E883", {"start": v(-47.5, 18.37) * mm, "end": v(-47.37, 18.29) * mm});
            skLineSegment(sketch, "E884", {"start": v(-47.37, 18.29) * mm, "end": v(-47.24, 18.21) * mm});
            skLineSegment(sketch, "E885", {"start": v(-47.24, 18.21) * mm, "end": v(-47.13, 18.14) * mm});
            skLineSegment(sketch, "E886", {"start": v(-47.13, 18.14) * mm, "end": v(-47.03, 18.08) * mm});
            skLineSegment(sketch, "E887", {"start": v(-47.03, 18.08) * mm, "end": v(-46.93, 18.02) * mm});
            skLineSegment(sketch, "E888", {"start": v(-46.93, 18.02) * mm, "end": v(-46.84, 17.97) * mm});
            skLineSegment(sketch, "E889", {"start": v(-46.84, 17.97) * mm, "end": v(-46.76, 17.93) * mm});
            skLineSegment(sketch, "E890", {"start": v(-46.76, 17.93) * mm, "end": v(-46.69, 17.9) * mm});
            skLineSegment(sketch, "E891", {"start": v(-46.69, 17.9) * mm, "end": v(-46.62, 17.86) * mm});
            skLineSegment(sketch, "E892", {"start": v(-46.62, 17.86) * mm, "end": v(-46.57, 17.84) * mm});
            skLineSegment(sketch, "E893", {"start": v(-46.57, 17.84) * mm, "end": v(-46.52, 17.82) * mm});
            skLineSegment(sketch, "E894", {"start": v(-46.52, 17.82) * mm, "end": v(-46.49, 17.8) * mm});
            skLineSegment(sketch, "E895", {"start": v(-46.49, 17.8) * mm, "end": v(-46.46, 17.79) * mm});
            skLineSegment(sketch, "E896", {"start": v(-46.46, 17.79) * mm, "end": v(-46.45, 17.78) * mm});
            skLineSegment(sketch, "E897", {"start": v(-46.45, 17.78) * mm, "end": v(-44.68, 17.1) * mm});
            skLineSegment(sketch, "E898", {"start": v(-44.68, 17.1) * mm, "end": v(-46.22, 12.38) * mm});
            skLineSegment(sketch, "E899", {"start": v(-46.22, 12.38) * mm, "end": v(-48.04, 12.87) * mm});
            skLineSegment(sketch, "E900", {"start": v(-48.04, 12.87) * mm, "end": v(-48.06, 12.88) * mm});
            skLineSegment(sketch, "E901", {"start": v(-48.06, 12.88) * mm, "end": v(-48.08, 12.88) * mm});
            skLineSegment(sketch, "E902", {"start": v(-48.08, 12.88) * mm, "end": v(-48.12, 12.9) * mm});
            skLineSegment(sketch, "E903", {"start": v(-48.12, 12.9) * mm, "end": v(-48.17, 12.9) * mm});
            skLineSegment(sketch, "E904", {"start": v(-48.17, 12.9) * mm, "end": v(-48.23, 12.91) * mm});
            skLineSegment(sketch, "E905", {"start": v(-48.23, 12.91) * mm, "end": v(-48.3, 12.92) * mm});
            skLineSegment(sketch, "E906", {"start": v(-48.3, 12.92) * mm, "end": v(-48.38, 12.93) * mm});
            skLineSegment(sketch, "E907", {"start": v(-48.38, 12.93) * mm, "end": v(-48.47, 12.95) * mm});
            skLineSegment(sketch, "E908", {"start": v(-48.47, 12.95) * mm, "end": v(-48.57, 12.96) * mm});
            skLineSegment(sketch, "E909", {"start": v(-48.57, 12.96) * mm, "end": v(-48.68, 12.97) * mm});
            skLineSegment(sketch, "E910", {"start": v(-48.68, 12.97) * mm, "end": v(-48.8, 12.98) * mm});
            skLineSegment(sketch, "E911", {"start": v(-48.8, 12.98) * mm, "end": v(-48.94, 13) * mm});
            skLineSegment(sketch, "E912", {"start": v(-48.94, 13) * mm, "end": v(-49.08, 13) * mm});
            skLineSegment(sketch, "E913", {"start": v(-49.08, 13) * mm, "end": v(-49.24, 13) * mm});
            skLineSegment(sketch, "E914", {"start": v(-49.24, 13) * mm, "end": v(-49.4, 13.01) * mm});
            skLineSegment(sketch, "E915", {"start": v(-49.4, 13.01) * mm, "end": v(-49.58, 13.02) * mm});
            skLineSegment(sketch, "E916", {"start": v(-49.58, 13.02) * mm, "end": v(-49.76, 13.02) * mm});
            skLineSegment(sketch, "E917", {"start": v(-49.76, 13.02) * mm, "end": v(-49.96, 13.02) * mm});
            skLineSegment(sketch, "E918", {"start": v(-49.96, 13.02) * mm, "end": v(-50.17, 13.01) * mm});
            skLineSegment(sketch, "E919", {"start": v(-50.17, 13.01) * mm, "end": v(-50.39, 13) * mm});
            skLineSegment(sketch, "E920", {"start": v(-50.39, 13) * mm, "end": v(-50.61, 12.99) * mm});
            skLineSegment(sketch, "E921", {"start": v(-50.61, 12.99) * mm, "end": v(-50.85, 12.97) * mm});
            skLineSegment(sketch, "E922", {"start": v(-50.85, 12.97) * mm, "end": v(-51.1, 12.95) * mm});
            skLineSegment(sketch, "E923", {"start": v(-51.1, 12.95) * mm, "end": v(-51.36, 12.93) * mm});
            skLineSegment(sketch, "E924", {"start": v(-51.36, 12.93) * mm, "end": v(-51.63, 12.9) * mm});
            skLineSegment(sketch, "E925", {"start": v(-51.63, 12.9) * mm, "end": v(-51.9, 12.86) * mm});
            skLineSegment(sketch, "E926", {"start": v(-51.9, 12.86) * mm, "end": v(-52.2, 12.82) * mm});
            skLineSegment(sketch, "E927", {"start": v(-52.2, 12.82) * mm, "end": v(-52.5, 12.77) * mm});
            skLineSegment(sketch, "E928", {"start": v(-52.5, 12.77) * mm, "end": v(-52.8, 12.72) * mm});
            skLineSegment(sketch, "E929", {"start": v(-52.8, 12.72) * mm, "end": v(-53.12, 12.66) * mm});
            skLineSegment(sketch, "E930", {"start": v(-53.12, 12.66) * mm, "end": v(-53.44, 12.6) * mm});
            skLineSegment(sketch, "E931", {"start": v(-53.44, 12.6) * mm, "end": v(-53.78, 12.52) * mm});
            skLineSegment(sketch, "E932", {"start": v(-53.78, 12.52) * mm, "end": v(-54.13, 12.44) * mm});
            skLineSegment(sketch, "E933", {"start": v(-54.13, 12.44) * mm, "end": v(-54.48, 12.36) * mm});
            skLineSegment(sketch, "E934", {"start": v(-54.48, 12.36) * mm, "end": v(-54.84, 12.26) * mm});
            skLineSegment(sketch, "E935", {"start": v(-54.84, 12.26) * mm, "end": v(-55.22, 12.16) * mm});
            skLineSegment(sketch, "E936", {"start": v(-55.22, 12.16) * mm, "end": v(-55.6, 12.04) * mm});
            skLineSegment(sketch, "E937", {"start": v(-55.6, 12.04) * mm, "end": v(-55.98, 11.92) * mm});
            skLineSegment(sketch, "E938", {"start": v(-55.98, 11.92) * mm, "end": v(-56.11, 11.74) * mm});
            skLineSegment(sketch, "E939", {"start": v(-56.11, 11.74) * mm, "end": v(-56.6, 9.1) * mm});
            skLineSegment(sketch, "E940", {"start": v(-56.6, 9.1) * mm, "end": v(-56.55, 8.88) * mm});
            skLineSegment(sketch, "E941", {"start": v(-56.55, 8.88) * mm, "end": v(-56.23, 8.63) * mm});
            skLineSegment(sketch, "E942", {"start": v(-56.23, 8.63) * mm, "end": v(-55.91, 8.39) * mm});
            skLineSegment(sketch, "E943", {"start": v(-55.91, 8.39) * mm, "end": v(-55.6, 8.16) * mm});
            skLineSegment(sketch, "E944", {"start": v(-55.6, 8.16) * mm, "end": v(-55.3, 7.94) * mm});
            skLineSegment(sketch, "E945", {"start": v(-55.3, 7.94) * mm, "end": v(-55, 7.73) * mm});
            skLineSegment(sketch, "E946", {"start": v(-55, 7.73) * mm, "end": v(-54.7, 7.53) * mm});
            skLineSegment(sketch, "E947", {"start": v(-54.7, 7.53) * mm, "end": v(-54.41, 7.34) * mm});
            skLineSegment(sketch, "E948", {"start": v(-54.41, 7.34) * mm, "end": v(-54.13, 7.17) * mm});
            skLineSegment(sketch, "E949", {"start": v(-54.13, 7.17) * mm, "end": v(-53.86, 7) * mm});
            skLineSegment(sketch, "E950", {"start": v(-53.86, 7) * mm, "end": v(-53.59, 6.84) * mm});
            skLineSegment(sketch, "E951", {"start": v(-53.59, 6.84) * mm, "end": v(-53.33, 6.69) * mm});
            skLineSegment(sketch, "E952", {"start": v(-53.33, 6.69) * mm, "end": v(-53.07, 6.55) * mm});
            skLineSegment(sketch, "E953", {"start": v(-53.07, 6.55) * mm, "end": v(-52.83, 6.41) * mm});
            skLineSegment(sketch, "E954", {"start": v(-52.83, 6.41) * mm, "end": v(-52.59, 6.29) * mm});
            skLineSegment(sketch, "E955", {"start": v(-52.59, 6.29) * mm, "end": v(-52.35, 6.17) * mm});
            skLineSegment(sketch, "E956", {"start": v(-52.35, 6.17) * mm, "end": v(-52.13, 6.06) * mm});
            skLineSegment(sketch, "E957", {"start": v(-52.13, 6.06) * mm, "end": v(-51.91, 5.96) * mm});
            skLineSegment(sketch, "E958", {"start": v(-51.91, 5.96) * mm, "end": v(-51.7, 5.87) * mm});
            skLineSegment(sketch, "E959", {"start": v(-51.7, 5.87) * mm, "end": v(-51.5, 5.78) * mm});
            skLineSegment(sketch, "E960", {"start": v(-51.5, 5.78) * mm, "end": v(-51.31, 5.7) * mm});
            skLineSegment(sketch, "E961", {"start": v(-51.31, 5.7) * mm, "end": v(-51.13, 5.63) * mm});
            skLineSegment(sketch, "E962", {"start": v(-51.13, 5.63) * mm, "end": v(-50.95, 5.57) * mm});
            skLineSegment(sketch, "E963", {"start": v(-50.95, 5.57) * mm, "end": v(-50.79, 5.5) * mm});
            skLineSegment(sketch, "E964", {"start": v(-50.79, 5.5) * mm, "end": v(-50.63, 5.45) * mm});
            skLineSegment(sketch, "E965", {"start": v(-50.63, 5.45) * mm, "end": v(-50.49, 5.4) * mm});
            skLineSegment(sketch, "E966", {"start": v(-50.49, 5.4) * mm, "end": v(-50.35, 5.36) * mm});
            skLineSegment(sketch, "E967", {"start": v(-50.35, 5.36) * mm, "end": v(-50.22, 5.32) * mm});
            skLineSegment(sketch, "E968", {"start": v(-50.22, 5.32) * mm, "end": v(-50.1, 5.3) * mm});
            skLineSegment(sketch, "E969", {"start": v(-50.1, 5.3) * mm, "end": v(-50, 5.26) * mm});
            skLineSegment(sketch, "E970", {"start": v(-50, 5.26) * mm, "end": v(-49.9, 5.24) * mm});
            skLineSegment(sketch, "E971", {"start": v(-49.9, 5.24) * mm, "end": v(-49.8, 5.22) * mm});
            skLineSegment(sketch, "E972", {"start": v(-49.8, 5.22) * mm, "end": v(-49.73, 5.2) * mm});
            skLineSegment(sketch, "E973", {"start": v(-49.73, 5.2) * mm, "end": v(-49.66, 5.19) * mm});
            skLineSegment(sketch, "E974", {"start": v(-49.66, 5.19) * mm, "end": v(-49.6, 5.17) * mm});
            skLineSegment(sketch, "E975", {"start": v(-49.6, 5.17) * mm, "end": v(-49.55, 5.17) * mm});
            skLineSegment(sketch, "E976", {"start": v(-49.55, 5.17) * mm, "end": v(-49.48, 5.16) * mm});
            skLineSegment(sketch, "E977", {"start": v(-49.48, 5.16) * mm, "end": v(-49.46, 5.15) * mm});
            skLineSegment(sketch, "E978", {"start": v(-49.46, 5.15) * mm, "end": v(-47.59, 4.96) * mm});
            skLineSegment(sketch, "E979", {"start": v(-47.59, 4.96) * mm, "end": v(-47.85, 0) * mm});
            skLineSegment(sketch, "E980", {"start": v(-47.85, 0) * mm, "end": v(-49.75, 0) * mm});
            skLineSegment(sketch, "E981", {"start": v(-49.75, 0) * mm, "end": v(-49.78, 0) * mm});
            skLineSegment(sketch, "E982", {"start": v(-49.78, 0) * mm, "end": v(-49.82, 0) * mm});
            skLineSegment(sketch, "E983", {"start": v(-49.82, 0) * mm, "end": v(-49.87, 0) * mm});
            skLineSegment(sketch, "E984", {"start": v(-49.87, 0) * mm, "end": v(-49.93, -0.01) * mm});
            skLineSegment(sketch, "E985", {"start": v(-49.93, -0.01) * mm, "end": v(-50, -0.02) * mm});
            skLineSegment(sketch, "E986", {"start": v(-50, -0.02) * mm, "end": v(-50.08, -0.03) * mm});
            skLineSegment(sketch, "E987", {"start": v(-50.08, -0.03) * mm, "end": v(-50.17, -0.04) * mm});
            skLineSegment(sketch, "E988", {"start": v(-50.17, -0.04) * mm, "end": v(-50.27, -0.05) * mm});
            skLineSegment(sketch, "E989", {"start": v(-50.27, -0.05) * mm, "end": v(-50.38, -0.07) * mm});
            skLineSegment(sketch, "E990", {"start": v(-50.38, -0.07) * mm, "end": v(-50.5, -0.1) * mm});
            skLineSegment(sketch, "E991", {"start": v(-50.5, -0.1) * mm, "end": v(-50.63, -0.12) * mm});
            skLineSegment(sketch, "E992", {"start": v(-50.63, -0.12) * mm, "end": v(-50.78, -0.15) * mm});
            skLineSegment(sketch, "E993", {"start": v(-50.78, -0.15) * mm, "end": v(-50.93, -0.18) * mm});
            skLineSegment(sketch, "E994", {"start": v(-50.93, -0.18) * mm, "end": v(-51.09, -0.21) * mm});
            skLineSegment(sketch, "E995", {"start": v(-51.09, -0.21) * mm, "end": v(-51.26, -0.26) * mm});
            skLineSegment(sketch, "E996", {"start": v(-51.26, -0.26) * mm, "end": v(-51.44, -0.3) * mm});
            skLineSegment(sketch, "E997", {"start": v(-51.44, -0.3) * mm, "end": v(-51.63, -0.36) * mm});
            skLineSegment(sketch, "E998", {"start": v(-51.63, -0.36) * mm, "end": v(-51.83, -0.42) * mm});
            skLineSegment(sketch, "E999", {"start": v(-51.83, -0.42) * mm, "end": v(-52.03, -0.48) * mm});
            skLineSegment(sketch, "E1000", {"start": v(-52.03, -0.48) * mm, "end": v(-52.25, -0.55) * mm});
            skLineSegment(sketch, "E1001", {"start": v(-52.25, -0.55) * mm, "end": v(-52.48, -0.63) * mm});
            skLineSegment(sketch, "E1002", {"start": v(-52.48, -0.63) * mm, "end": v(-52.71, -0.71) * mm});
            skLineSegment(sketch, "E1003", {"start": v(-52.71, -0.71) * mm, "end": v(-52.95, -0.8) * mm});
            skLineSegment(sketch, "E1004", {"start": v(-52.95, -0.8) * mm, "end": v(-53.2, -0.9) * mm});
            skLineSegment(sketch, "E1005", {"start": v(-53.2, -0.9) * mm, "end": v(-53.47, -1.01) * mm});
            skLineSegment(sketch, "E1006", {"start": v(-53.47, -1.01) * mm, "end": v(-53.73, -1.12) * mm});
            skLineSegment(sketch, "E1007", {"start": v(-53.73, -1.12) * mm, "end": v(-54, -1.25) * mm});
            skLineSegment(sketch, "E1008", {"start": v(-54, -1.25) * mm, "end": v(-54.3, -1.38) * mm});
            skLineSegment(sketch, "E1009", {"start": v(-54.3, -1.38) * mm, "end": v(-54.58, -1.52) * mm});
            skLineSegment(sketch, "E1010", {"start": v(-54.58, -1.52) * mm, "end": v(-54.88, -1.67) * mm});
            skLineSegment(sketch, "E1011", {"start": v(-54.88, -1.67) * mm, "end": v(-55.19, -1.82) * mm});
            skLineSegment(sketch, "E1012", {"start": v(-55.19, -1.82) * mm, "end": v(-55.5, -2) * mm});
            skLineSegment(sketch, "E1013", {"start": v(-55.5, -2) * mm, "end": v(-55.82, -2.17) * mm});
            skLineSegment(sketch, "E1014", {"start": v(-55.82, -2.17) * mm, "end": v(-56.15, -2.35) * mm});
            skLineSegment(sketch, "E1015", {"start": v(-56.15, -2.35) * mm, "end": v(-56.48, -2.55) * mm});
            skLineSegment(sketch, "E1016", {"start": v(-56.48, -2.55) * mm, "end": v(-56.82, -2.76) * mm});
            skLineSegment(sketch, "E1017", {"start": v(-56.82, -2.76) * mm, "end": v(-57.16, -2.97) * mm});
            skLineSegment(sketch, "E1018", {"start": v(-57.16, -2.97) * mm, "end": v(-57.24, -3.19) * mm});
            skLineSegment(sketch, "E1019", {"start": v(-57.24, -3.19) * mm, "end": v(-57.03, -5.86) * mm});
            skLineSegment(sketch, "E1020", {"start": v(-57.03, -5.86) * mm, "end": v(-56.92, -6.06) * mm});
            skLineSegment(sketch, "E1021", {"start": v(-56.92, -6.06) * mm, "end": v(-56.54, -6.22) * mm});
            skLineSegment(sketch, "E1022", {"start": v(-56.54, -6.22) * mm, "end": v(-56.18, -6.37) * mm});
            skLineSegment(sketch, "E1023", {"start": v(-56.18, -6.37) * mm, "end": v(-55.82, -6.5) * mm});
            skLineSegment(sketch, "E1024", {"start": v(-55.82, -6.5) * mm, "end": v(-55.47, -6.64) * mm});
            skLineSegment(sketch, "E1025", {"start": v(-55.47, -6.64) * mm, "end": v(-55.12, -6.77) * mm});
            skLineSegment(sketch, "E1026", {"start": v(-55.12, -6.77) * mm, "end": v(-54.79, -6.88) * mm});
            skLineSegment(sketch, "E1027", {"start": v(-54.79, -6.88) * mm, "end": v(-54.46, -6.99) * mm});
            skLineSegment(sketch, "E1028", {"start": v(-54.46, -6.99) * mm, "end": v(-54.14, -7.1) * mm});
            skLineSegment(sketch, "E1029", {"start": v(-54.14, -7.1) * mm, "end": v(-53.83, -7.18) * mm});
            skLineSegment(sketch, "E1030", {"start": v(-53.83, -7.18) * mm, "end": v(-53.53, -7.27) * mm});
            skLineSegment(sketch, "E1031", {"start": v(-53.53, -7.27) * mm, "end": v(-53.24, -7.34) * mm});
            skLineSegment(sketch, "E1032", {"start": v(-53.24, -7.34) * mm, "end": v(-52.96, -7.41) * mm});
            skLineSegment(sketch, "E1033", {"start": v(-52.96, -7.41) * mm, "end": v(-52.69, -7.48) * mm});
            skLineSegment(sketch, "E1034", {"start": v(-52.69, -7.48) * mm, "end": v(-52.42, -7.54) * mm});
            skLineSegment(sketch, "E1035", {"start": v(-52.42, -7.54) * mm, "end": v(-52.17, -7.59) * mm});
            skLineSegment(sketch, "E1036", {"start": v(-52.17, -7.59) * mm, "end": v(-51.92, -7.63) * mm});
            skLineSegment(sketch, "E1037", {"start": v(-51.92, -7.63) * mm, "end": v(-51.69, -7.68) * mm});
            skLineSegment(sketch, "E1038", {"start": v(-51.69, -7.68) * mm, "end": v(-51.46, -7.71) * mm});
            skLineSegment(sketch, "E1039", {"start": v(-51.46, -7.71) * mm, "end": v(-51.25, -7.74) * mm});
            skLineSegment(sketch, "E1040", {"start": v(-51.25, -7.74) * mm, "end": v(-51.04, -7.77) * mm});
            skLineSegment(sketch, "E1041", {"start": v(-51.04, -7.77) * mm, "end": v(-50.84, -7.8) * mm});
            skLineSegment(sketch, "E1042", {"start": v(-50.84, -7.8) * mm, "end": v(-50.66, -7.8) * mm});
            skLineSegment(sketch, "E1043", {"start": v(-50.66, -7.8) * mm, "end": v(-50.48, -7.82) * mm});
            skLineSegment(sketch, "E1044", {"start": v(-50.48, -7.82) * mm, "end": v(-50.32, -7.84) * mm});
            skLineSegment(sketch, "E1045", {"start": v(-50.32, -7.84) * mm, "end": v(-50.16, -7.84) * mm});
            skLineSegment(sketch, "E1046", {"start": v(-50.16, -7.84) * mm, "end": v(-50.02, -7.85) * mm});
            skLineSegment(sketch, "E1047", {"start": v(-50.02, -7.85) * mm, "end": v(-49.89, -7.85) * mm});
            skLineSegment(sketch, "E1048", {"start": v(-49.89, -7.85) * mm, "end": v(-49.77, -7.86) * mm});
            skLineSegment(sketch, "E1049", {"start": v(-49.77, -7.86) * mm, "end": v(-49.65, -7.85) * mm});
            skLineSegment(sketch, "E1050", {"start": v(-49.65, -7.85) * mm, "end": v(-49.55, -7.85) * mm});
            skLineSegment(sketch, "E1051", {"start": v(-49.55, -7.85) * mm, "end": v(-49.46, -7.85) * mm});
            skLineSegment(sketch, "E1052", {"start": v(-49.46, -7.85) * mm, "end": v(-49.38, -7.85) * mm});
            skLineSegment(sketch, "E1053", {"start": v(-49.38, -7.85) * mm, "end": v(-49.3, -7.84) * mm});
            skLineSegment(sketch, "E1054", {"start": v(-49.3, -7.84) * mm, "end": v(-49.25, -7.84) * mm});
            skLineSegment(sketch, "E1055", {"start": v(-49.25, -7.84) * mm, "end": v(-49.2, -7.83) * mm});
            skLineSegment(sketch, "E1056", {"start": v(-49.2, -7.83) * mm, "end": v(-49.16, -7.83) * mm});
            skLineSegment(sketch, "E1057", {"start": v(-49.16, -7.83) * mm, "end": v(-49.13, -7.83) * mm});
            skLineSegment(sketch, "E1058", {"start": v(-49.13, -7.83) * mm, "end": v(-49.11, -7.82) * mm});
            skLineSegment(sketch, "E1059", {"start": v(-49.11, -7.82) * mm, "end": v(-47.25, -7.53) * mm});
            skLineSegment(sketch, "E1060", {"start": v(-47.25, -7.53) * mm, "end": v(-46.22, -12.38) * mm});
            skLineSegment(sketch, "E1061", {"start": v(-46.22, -12.38) * mm, "end": v(-48.04, -12.87) * mm});
            skLineSegment(sketch, "E1062", {"start": v(-48.04, -12.87) * mm, "end": v(-48.05, -12.88) * mm});
            skLineSegment(sketch, "E1063", {"start": v(-48.05, -12.88) * mm, "end": v(-48.08, -12.89) * mm});
            skLineSegment(sketch, "E1064", {"start": v(-48.08, -12.89) * mm, "end": v(-48.12, -12.9) * mm});
            skLineSegment(sketch, "E1065", {"start": v(-48.12, -12.9) * mm, "end": v(-48.17, -12.91) * mm});
            skLineSegment(sketch, "E1066", {"start": v(-48.17, -12.91) * mm, "end": v(-48.22, -12.93) * mm});
            skLineSegment(sketch, "E1067", {"start": v(-48.22, -12.93) * mm, "end": v(-48.29, -12.96) * mm});
            skLineSegment(sketch, "E1068", {"start": v(-48.29, -12.96) * mm, "end": v(-48.36, -12.99) * mm});
            skLineSegment(sketch, "E1069", {"start": v(-48.36, -12.99) * mm, "end": v(-48.45, -13.02) * mm});
            skLineSegment(sketch, "E1070", {"start": v(-48.45, -13.02) * mm, "end": v(-48.54, -13.06) * mm});
            skLineSegment(sketch, "E1071", {"start": v(-48.54, -13.06) * mm, "end": v(-48.65, -13.1) * mm});
            skLineSegment(sketch, "E1072", {"start": v(-48.65, -13.1) * mm, "end": v(-48.76, -13.16) * mm});
            skLineSegment(sketch, "E1073", {"start": v(-48.76, -13.16) * mm, "end": v(-48.88, -13.22) * mm});
            skLineSegment(sketch, "E1074", {"start": v(-48.88, -13.22) * mm, "end": v(-49, -13.28) * mm});
            skLineSegment(sketch, "E1075", {"start": v(-49, -13.28) * mm, "end": v(-49.14, -13.35) * mm});
            skLineSegment(sketch, "E1076", {"start": v(-49.14, -13.35) * mm, "end": v(-49.29, -13.43) * mm});
            skLineSegment(sketch, "E1077", {"start": v(-49.29, -13.43) * mm, "end": v(-49.44, -13.52) * mm});
            skLineSegment(sketch, "E1078", {"start": v(-49.44, -13.52) * mm, "end": v(-49.6, -13.6) * mm});
            skLineSegment(sketch, "E1079", {"start": v(-49.6, -13.6) * mm, "end": v(-49.77, -13.7) * mm});
            skLineSegment(sketch, "E1080", {"start": v(-49.77, -13.7) * mm, "end": v(-49.95, -13.82) * mm});
            skLineSegment(sketch, "E1081", {"start": v(-49.95, -13.82) * mm, "end": v(-50.14, -13.93) * mm});
            skLineSegment(sketch, "E1082", {"start": v(-50.14, -13.93) * mm, "end": v(-50.33, -14.06) * mm});
            skLineSegment(sketch, "E1083", {"start": v(-50.33, -14.06) * mm, "end": v(-50.53, -14.19) * mm});
            skLineSegment(sketch, "E1084", {"start": v(-50.53, -14.19) * mm, "end": v(-50.73, -14.33) * mm});
            skLineSegment(sketch, "E1085", {"start": v(-50.73, -14.33) * mm, "end": v(-50.94, -14.48) * mm});
            skLineSegment(sketch, "E1086", {"start": v(-50.94, -14.48) * mm, "end": v(-51.16, -14.64) * mm});
            skLineSegment(sketch, "E1087", {"start": v(-51.16, -14.64) * mm, "end": v(-51.38, -14.81) * mm});
            skLineSegment(sketch, "E1088", {"start": v(-51.38, -14.81) * mm, "end": v(-51.61, -15) * mm});
            skLineSegment(sketch, "E1089", {"start": v(-51.61, -15) * mm, "end": v(-51.85, -15.18) * mm});
            skLineSegment(sketch, "E1090", {"start": v(-51.85, -15.18) * mm, "end": v(-52.09, -15.38) * mm});
            skLineSegment(sketch, "E1091", {"start": v(-52.09, -15.38) * mm, "end": v(-52.33, -15.6) * mm});
            skLineSegment(sketch, "E1092", {"start": v(-52.33, -15.6) * mm, "end": v(-52.58, -15.81) * mm});
            skLineSegment(sketch, "E1093", {"start": v(-52.58, -15.81) * mm, "end": v(-52.84, -16.04) * mm});
            skLineSegment(sketch, "E1094", {"start": v(-52.84, -16.04) * mm, "end": v(-53.1, -16.29) * mm});
            skLineSegment(sketch, "E1095", {"start": v(-53.1, -16.29) * mm, "end": v(-53.36, -16.54) * mm});
            skLineSegment(sketch, "E1096", {"start": v(-53.36, -16.54) * mm, "end": v(-53.62, -16.8) * mm});
            skLineSegment(sketch, "E1097", {"start": v(-53.62, -16.8) * mm, "end": v(-53.9, -17.08) * mm});
            skLineSegment(sketch, "E1098", {"start": v(-53.9, -17.08) * mm, "end": v(-54.17, -17.37) * mm});
            skLineSegment(sketch, "E1099", {"start": v(-54.17, -17.37) * mm, "end": v(-54.44, -17.67) * mm});
            skLineSegment(sketch, "E1100", {"start": v(-54.44, -17.67) * mm, "end": v(-54.46, -17.9) * mm});
            skLineSegment(sketch, "E1101", {"start": v(-54.46, -17.9) * mm, "end": v(-53.57, -20.42) * mm});
            skLineSegment(sketch, "E1102", {"start": v(-53.57, -20.42) * mm, "end": v(-53.41, -20.58) * mm});
            skLineSegment(sketch, "E1103", {"start": v(-53.41, -20.58) * mm, "end": v(-53, -20.64) * mm});
            skLineSegment(sketch, "E1104", {"start": v(-53, -20.64) * mm, "end": v(-52.61, -20.7) * mm});
            skLineSegment(sketch, "E1105", {"start": v(-52.61, -20.7) * mm, "end": v(-52.23, -20.74) * mm});
            skLineSegment(sketch, "E1106", {"start": v(-52.23, -20.74) * mm, "end": v(-51.86, -20.77) * mm});
            skLineSegment(sketch, "E1107", {"start": v(-51.86, -20.77) * mm, "end": v(-51.5, -20.8) * mm});
            skLineSegment(sketch, "E1108", {"start": v(-51.5, -20.8) * mm, "end": v(-51.14, -20.83) * mm});
            skLineSegment(sketch, "E1109", {"start": v(-51.14, -20.83) * mm, "end": v(-50.8, -20.85) * mm});
            skLineSegment(sketch, "E1110", {"start": v(-50.8, -20.85) * mm, "end": v(-50.46, -20.86) * mm});
            skLineSegment(sketch, "E1111", {"start": v(-50.46, -20.86) * mm, "end": v(-50.14, -20.87) * mm});
            skLineSegment(sketch, "E1112", {"start": v(-50.14, -20.87) * mm, "end": v(-49.83, -20.87) * mm});
            skLineSegment(sketch, "E1113", {"start": v(-49.83, -20.87) * mm, "end": v(-49.53, -20.87) * mm});
            skLineSegment(sketch, "E1114", {"start": v(-49.53, -20.87) * mm, "end": v(-49.24, -20.87) * mm});
            skLineSegment(sketch, "E1115", {"start": v(-49.24, -20.87) * mm, "end": v(-48.95, -20.86) * mm});
            skLineSegment(sketch, "E1116", {"start": v(-48.95, -20.86) * mm, "end": v(-48.68, -20.85) * mm});
            skLineSegment(sketch, "E1117", {"start": v(-48.68, -20.85) * mm, "end": v(-48.43, -20.83) * mm});
            skLineSegment(sketch, "E1118", {"start": v(-48.43, -20.83) * mm, "end": v(-48.18, -20.81) * mm});
            skLineSegment(sketch, "E1119", {"start": v(-48.18, -20.81) * mm, "end": v(-47.94, -20.8) * mm});
            skLineSegment(sketch, "E1120", {"start": v(-47.94, -20.8) * mm, "end": v(-47.71, -20.77) * mm});
            skLineSegment(sketch, "E1121", {"start": v(-47.71, -20.77) * mm, "end": v(-47.5, -20.74) * mm});
            skLineSegment(sketch, "E1122", {"start": v(-47.5, -20.74) * mm, "end": v(-47.3, -20.71) * mm});
            skLineSegment(sketch, "E1123", {"start": v(-47.3, -20.71) * mm, "end": v(-47.1, -20.69) * mm});
            skLineSegment(sketch, "E1124", {"start": v(-47.1, -20.69) * mm, "end": v(-46.91, -20.66) * mm});
            skLineSegment(sketch, "E1125", {"start": v(-46.91, -20.66) * mm, "end": v(-46.74, -20.62) * mm});
            skLineSegment(sketch, "E1126", {"start": v(-46.74, -20.62) * mm, "end": v(-46.58, -20.6) * mm});
            skLineSegment(sketch, "E1127", {"start": v(-46.58, -20.6) * mm, "end": v(-46.43, -20.56) * mm});
            skLineSegment(sketch, "E1128", {"start": v(-46.43, -20.56) * mm, "end": v(-46.29, -20.53) * mm});
            skLineSegment(sketch, "E1129", {"start": v(-46.29, -20.53) * mm, "end": v(-46.15, -20.5) * mm});
            skLineSegment(sketch, "E1130", {"start": v(-46.15, -20.5) * mm, "end": v(-46.04, -20.47) * mm});
            skLineSegment(sketch, "E1131", {"start": v(-46.04, -20.47) * mm, "end": v(-45.93, -20.44) * mm});
            skLineSegment(sketch, "E1132", {"start": v(-45.93, -20.44) * mm, "end": v(-45.83, -20.41) * mm});
            skLineSegment(sketch, "E1133", {"start": v(-45.83, -20.41) * mm, "end": v(-45.74, -20.38) * mm});
            skLineSegment(sketch, "E1134", {"start": v(-45.74, -20.38) * mm, "end": v(-45.66, -20.36) * mm});
            skLineSegment(sketch, "E1135", {"start": v(-45.66, -20.36) * mm, "end": v(-45.6, -20.34) * mm});
            skLineSegment(sketch, "E1136", {"start": v(-45.6, -20.34) * mm, "end": v(-45.54, -20.32) * mm});
            skLineSegment(sketch, "E1137", {"start": v(-45.54, -20.32) * mm, "end": v(-45.5, -20.3) * mm});
            skLineSegment(sketch, "E1138", {"start": v(-45.5, -20.3) * mm, "end": v(-45.46, -20.29) * mm});
            skLineSegment(sketch, "E1139", {"start": v(-45.46, -20.29) * mm, "end": v(-45.43, -20.28) * mm});
            skLineSegment(sketch, "E1140", {"start": v(-45.43, -20.28) * mm, "end": v(-45.41, -20.27) * mm});
            skLineSegment(sketch, "E1141", {"start": v(-45.41, -20.27) * mm, "end": v(-43.7, -19.5) * mm});
            skLineSegment(sketch, "E1142", {"start": v(-43.7, -19.5) * mm, "end": v(-41.43, -23.92) * mm});
            skLineSegment(sketch, "E1143", {"start": v(-41.43, -23.92) * mm, "end": v(-43.07, -24.87) * mm});
            skLineSegment(sketch, "E1144", {"start": v(-43.07, -24.87) * mm, "end": v(-43.09, -24.88) * mm});
            skLineSegment(sketch, "E1145", {"start": v(-43.09, -24.88) * mm, "end": v(-43.1, -24.9) * mm});
            skLineSegment(sketch, "E1146", {"start": v(-43.1, -24.9) * mm, "end": v(-43.14, -24.91) * mm});
            skLineSegment(sketch, "E1147", {"start": v(-43.14, -24.91) * mm, "end": v(-43.18, -24.94) * mm});
            skLineSegment(sketch, "E1148", {"start": v(-43.18, -24.94) * mm, "end": v(-43.23, -24.97) * mm});
            skLineSegment(sketch, "E1149", {"start": v(-43.23, -24.97) * mm, "end": v(-43.29, -25.02) * mm});
            skLineSegment(sketch, "E1150", {"start": v(-43.29, -25.02) * mm, "end": v(-43.35, -25.06) * mm});
            skLineSegment(sketch, "E1151", {"start": v(-43.35, -25.06) * mm, "end": v(-43.43, -25.12) * mm});
            skLineSegment(sketch, "E1152", {"start": v(-43.43, -25.12) * mm, "end": v(-43.5, -25.18) * mm});
            skLineSegment(sketch, "E1153", {"start": v(-43.5, -25.18) * mm, "end": v(-43.6, -25.25) * mm});
            skLineSegment(sketch, "E1154", {"start": v(-43.6, -25.25) * mm, "end": v(-43.69, -25.33) * mm});
            skLineSegment(sketch, "E1155", {"start": v(-43.69, -25.33) * mm, "end": v(-43.8, -25.42) * mm});
            skLineSegment(sketch, "E1156", {"start": v(-43.8, -25.42) * mm, "end": v(-43.9, -25.51) * mm});
            skLineSegment(sketch, "E1157", {"start": v(-43.9, -25.51) * mm, "end": v(-44.01, -25.62) * mm});
            skLineSegment(sketch, "E1158", {"start": v(-44.01, -25.62) * mm, "end": v(-44.13, -25.73) * mm});
            skLineSegment(sketch, "E1159", {"start": v(-44.13, -25.73) * mm, "end": v(-44.26, -25.85) * mm});
            skLineSegment(sketch, "E1160", {"start": v(-44.26, -25.85) * mm, "end": v(-44.4, -25.98) * mm});
            skLineSegment(sketch, "E1161", {"start": v(-44.4, -25.98) * mm, "end": v(-44.53, -26.12) * mm});
            skLineSegment(sketch, "E1162", {"start": v(-44.53, -26.12) * mm, "end": v(-44.67, -26.27) * mm});
            skLineSegment(sketch, "E1163", {"start": v(-44.67, -26.27) * mm, "end": v(-44.82, -26.43) * mm});
            skLineSegment(sketch, "E1164", {"start": v(-44.82, -26.43) * mm, "end": v(-44.97, -26.6) * mm});
            skLineSegment(sketch, "E1165", {"start": v(-44.97, -26.6) * mm, "end": v(-45.13, -26.78) * mm});
            skLineSegment(sketch, "E1166", {"start": v(-45.13, -26.78) * mm, "end": v(-45.3, -26.97) * mm});
            skLineSegment(sketch, "E1167", {"start": v(-45.3, -26.97) * mm, "end": v(-45.46, -27.17) * mm});
            skLineSegment(sketch, "E1168", {"start": v(-45.46, -27.17) * mm, "end": v(-45.63, -27.39) * mm});
            skLineSegment(sketch, "E1169", {"start": v(-45.63, -27.39) * mm, "end": v(-45.8, -27.6) * mm});
            skLineSegment(sketch, "E1170", {"start": v(-45.8, -27.6) * mm, "end": v(-45.97, -27.84) * mm});
            skLineSegment(sketch, "E1171", {"start": v(-45.97, -27.84) * mm, "end": v(-46.15, -28.08) * mm});
            skLineSegment(sketch, "E1172", {"start": v(-46.15, -28.08) * mm, "end": v(-46.33, -28.34) * mm});
            skLineSegment(sketch, "E1173", {"start": v(-46.33, -28.34) * mm, "end": v(-46.51, -28.6) * mm});
            skLineSegment(sketch, "E1174", {"start": v(-46.51, -28.6) * mm, "end": v(-46.7, -28.88) * mm});
            skLineSegment(sketch, "E1175", {"start": v(-46.7, -28.88) * mm, "end": v(-46.88, -29.17) * mm});
            skLineSegment(sketch, "E1176", {"start": v(-46.88, -29.17) * mm, "end": v(-47.07, -29.47) * mm});
            skLineSegment(sketch, "E1177", {"start": v(-47.07, -29.47) * mm, "end": v(-47.26, -29.79) * mm});
            skLineSegment(sketch, "E1178", {"start": v(-47.26, -29.79) * mm, "end": v(-47.45, -30.11) * mm});
            skLineSegment(sketch, "E1179", {"start": v(-47.45, -30.11) * mm, "end": v(-47.64, -30.45) * mm});
            skLineSegment(sketch, "E1180", {"start": v(-47.64, -30.45) * mm, "end": v(-47.83, -30.8) * mm});
            skLineSegment(sketch, "E1181", {"start": v(-47.83, -30.8) * mm, "end": v(-48.02, -31.16) * mm});
            skLineSegment(sketch, "E1182", {"start": v(-48.02, -31.16) * mm, "end": v(-47.98, -31.38) * mm});
            skLineSegment(sketch, "E1183", {"start": v(-47.98, -31.38) * mm, "end": v(-46.46, -33.59) * mm});
            skLineSegment(sketch, "E1184", {"start": v(-46.46, -33.59) * mm, "end": v(-46.26, -33.7) * mm});
            skLineSegment(sketch, "E1185", {"start": v(-46.26, -33.7) * mm, "end": v(-45.86, -33.66) * mm});
            skLineSegment(sketch, "E1186", {"start": v(-45.86, -33.66) * mm, "end": v(-45.47, -33.6) * mm});
            skLineSegment(sketch, "E1187", {"start": v(-45.47, -33.6) * mm, "end": v(-45.09, -33.55) * mm});
            skLineSegment(sketch, "E1188", {"start": v(-45.09, -33.55) * mm, "end": v(-44.71, -33.49) * mm});
            skLineSegment(sketch, "E1189", {"start": v(-44.71, -33.49) * mm, "end": v(-44.35, -33.42) * mm});
            skLineSegment(sketch, "E1190", {"start": v(-44.35, -33.42) * mm, "end": v(-44, -33.35) * mm});
            skLineSegment(sketch, "E1191", {"start": v(-44, -33.35) * mm, "end": v(-43.67, -33.28) * mm});
            skLineSegment(sketch, "E1192", {"start": v(-43.67, -33.28) * mm, "end": v(-43.34, -33.21) * mm});
            skLineSegment(sketch, "E1193", {"start": v(-43.34, -33.21) * mm, "end": v(-43.03, -33.14) * mm});
            skLineSegment(sketch, "E1194", {"start": v(-43.03, -33.14) * mm, "end": v(-42.73, -33.06) * mm});
            skLineSegment(sketch, "E1195", {"start": v(-42.73, -33.06) * mm, "end": v(-42.44, -32.98) * mm});
            skLineSegment(sketch, "E1196", {"start": v(-42.44, -32.98) * mm, "end": v(-42.16, -32.9) * mm});
            skLineSegment(sketch, "E1197", {"start": v(-42.16, -32.9) * mm, "end": v(-41.89, -32.82) * mm});
            skLineSegment(sketch, "E1198", {"start": v(-41.89, -32.82) * mm, "end": v(-41.63, -32.74) * mm});
            skLineSegment(sketch, "E1199", {"start": v(-41.63, -32.74) * mm, "end": v(-41.38, -32.65) * mm});
            skLineSegment(sketch, "E1200", {"start": v(-41.38, -32.65) * mm, "end": v(-41.15, -32.57) * mm});
            skLineSegment(sketch, "E1201", {"start": v(-41.15, -32.57) * mm, "end": v(-40.92, -32.5) * mm});
            skLineSegment(sketch, "E1202", {"start": v(-40.92, -32.5) * mm, "end": v(-40.71, -32.4) * mm});
            skLineSegment(sketch, "E1203", {"start": v(-40.71, -32.4) * mm, "end": v(-40.5, -32.33) * mm});
            skLineSegment(sketch, "E1204", {"start": v(-40.5, -32.33) * mm, "end": v(-40.32, -32.25) * mm});
            skLineSegment(sketch, "E1205", {"start": v(-40.32, -32.25) * mm, "end": v(-40.14, -32.17) * mm});
            skLineSegment(sketch, "E1206", {"start": v(-40.14, -32.17) * mm, "end": v(-39.97, -32.1) * mm});
            skLineSegment(sketch, "E1207", {"start": v(-39.97, -32.1) * mm, "end": v(-39.8, -32.02) * mm});
            skLineSegment(sketch, "E1208", {"start": v(-39.8, -32.02) * mm, "end": v(-39.66, -31.95) * mm});
            skLineSegment(sketch, "E1209", {"start": v(-39.66, -31.95) * mm, "end": v(-39.52, -31.88) * mm});
            skLineSegment(sketch, "E1210", {"start": v(-39.52, -31.88) * mm, "end": v(-39.4, -31.8) * mm});
            skLineSegment(sketch, "E1211", {"start": v(-39.4, -31.8) * mm, "end": v(-39.28, -31.75) * mm});
            skLineSegment(sketch, "E1212", {"start": v(-39.28, -31.75) * mm, "end": v(-39.17, -31.69) * mm});
            skLineSegment(sketch, "E1213", {"start": v(-39.17, -31.69) * mm, "end": v(-39.07, -31.63) * mm});
            skLineSegment(sketch, "E1214", {"start": v(-39.07, -31.63) * mm, "end": v(-38.98, -31.58) * mm});
            skLineSegment(sketch, "E1215", {"start": v(-38.98, -31.58) * mm, "end": v(-38.9, -31.53) * mm});
            skLineSegment(sketch, "E1216", {"start": v(-38.9, -31.53) * mm, "end": v(-38.84, -31.48) * mm});
            skLineSegment(sketch, "E1217", {"start": v(-38.84, -31.48) * mm, "end": v(-38.78, -31.45) * mm});
            skLineSegment(sketch, "E1218", {"start": v(-38.78, -31.45) * mm, "end": v(-38.73, -31.41) * mm});
            skLineSegment(sketch, "E1219", {"start": v(-38.73, -31.41) * mm, "end": v(-38.69, -31.38) * mm});
            skLineSegment(sketch, "E1220", {"start": v(-38.69, -31.38) * mm, "end": v(-38.66, -31.36) * mm});
            skLineSegment(sketch, "E1221", {"start": v(-38.66, -31.36) * mm, "end": v(-38.64, -31.34) * mm});
            skLineSegment(sketch, "E1222", {"start": v(-38.64, -31.34) * mm, "end": v(-38.62, -31.33) * mm});
            skLineSegment(sketch, "E1223", {"start": v(-38.62, -31.33) * mm, "end": v(-37.16, -30.14) * mm});
            skLineSegment(sketch, "E1224", {"start": v(-37.16, -30.14) * mm, "end": v(-33.83, -33.83) * mm});
            skLineSegment(sketch, "E1225", {"start": v(-33.83, -33.83) * mm, "end": v(-35.17, -35.17) * mm});
            skLineSegment(sketch, "E1226", {"start": v(-35.17, -35.17) * mm, "end": v(-35.18, -35.18) * mm});
            skLineSegment(sketch, "E1227", {"start": v(-35.18, -35.18) * mm, "end": v(-35.2, -35.2) * mm});
            skLineSegment(sketch, "E1228", {"start": v(-35.2, -35.2) * mm, "end": v(-35.22, -35.23) * mm});
            skLineSegment(sketch, "E1229", {"start": v(-35.22, -35.23) * mm, "end": v(-35.26, -35.27) * mm});
            skLineSegment(sketch, "E1230", {"start": v(-35.26, -35.27) * mm, "end": v(-35.3, -35.31) * mm});
            skLineSegment(sketch, "E1231", {"start": v(-35.3, -35.31) * mm, "end": v(-35.34, -35.37) * mm});
            skLineSegment(sketch, "E1232", {"start": v(-35.34, -35.37) * mm, "end": v(-35.4, -35.43) * mm});
            skLineSegment(sketch, "E1233", {"start": v(-35.4, -35.43) * mm, "end": v(-35.45, -35.5) * mm});
            skLineSegment(sketch, "E1234", {"start": v(-35.45, -35.5) * mm, "end": v(-35.5, -35.58) * mm});
            skLineSegment(sketch, "E1235", {"start": v(-35.5, -35.58) * mm, "end": v(-35.57, -35.67) * mm});
            skLineSegment(sketch, "E1236", {"start": v(-35.57, -35.67) * mm, "end": v(-35.65, -35.78) * mm});
            skLineSegment(sketch, "E1237", {"start": v(-35.65, -35.78) * mm, "end": v(-35.72, -35.89) * mm});
            skLineSegment(sketch, "E1238", {"start": v(-35.72, -35.89) * mm, "end": v(-35.8, -36) * mm});
            skLineSegment(sketch, "E1239", {"start": v(-35.8, -36) * mm, "end": v(-35.88, -36.14) * mm});
            skLineSegment(sketch, "E1240", {"start": v(-35.88, -36.14) * mm, "end": v(-35.97, -36.28) * mm});
            skLineSegment(sketch, "E1241", {"start": v(-35.97, -36.28) * mm, "end": v(-36.06, -36.43) * mm});
            skLineSegment(sketch, "E1242", {"start": v(-36.06, -36.43) * mm, "end": v(-36.16, -36.59) * mm});
            skLineSegment(sketch, "E1243", {"start": v(-36.16, -36.59) * mm, "end": v(-36.25, -36.76) * mm});
            skLineSegment(sketch, "E1244", {"start": v(-36.25, -36.76) * mm, "end": v(-36.35, -36.94) * mm});
            skLineSegment(sketch, "E1245", {"start": v(-36.35, -36.94) * mm, "end": v(-36.45, -37.13) * mm});
            skLineSegment(sketch, "E1246", {"start": v(-36.45, -37.13) * mm, "end": v(-36.56, -37.34) * mm});
            skLineSegment(sketch, "E1247", {"start": v(-36.56, -37.34) * mm, "end": v(-36.66, -37.55) * mm});
            skLineSegment(sketch, "E1248", {"start": v(-36.66, -37.55) * mm, "end": v(-36.77, -37.78) * mm});
            skLineSegment(sketch, "E1249", {"start": v(-36.77, -37.78) * mm, "end": v(-36.87, -38.01) * mm});
            skLineSegment(sketch, "E1250", {"start": v(-36.87, -38.01) * mm, "end": v(-36.98, -38.26) * mm});
            skLineSegment(sketch, "E1251", {"start": v(-36.98, -38.26) * mm, "end": v(-37.1, -38.52) * mm});
            skLineSegment(sketch, "E1252", {"start": v(-37.1, -38.52) * mm, "end": v(-37.2, -38.8) * mm});
            skLineSegment(sketch, "E1253", {"start": v(-37.2, -38.8) * mm, "end": v(-37.3, -39.07) * mm});
            skLineSegment(sketch, "E1254", {"start": v(-37.3, -39.07) * mm, "end": v(-37.42, -39.37) * mm});
            skLineSegment(sketch, "E1255", {"start": v(-37.42, -39.37) * mm, "end": v(-37.52, -39.67) * mm});
            skLineSegment(sketch, "E1256", {"start": v(-37.52, -39.67) * mm, "end": v(-37.63, -39.99) * mm});
            skLineSegment(sketch, "E1257", {"start": v(-37.63, -39.99) * mm, "end": v(-37.73, -40.31) * mm});
            skLineSegment(sketch, "E1258", {"start": v(-37.73, -40.31) * mm, "end": v(-37.84, -40.65) * mm});
            skLineSegment(sketch, "E1259", {"start": v(-37.84, -40.65) * mm, "end": v(-37.94, -41) * mm});
            skLineSegment(sketch, "E1260", {"start": v(-37.94, -41) * mm, "end": v(-38.04, -41.37) * mm});
            skLineSegment(sketch, "E1261", {"start": v(-38.04, -41.37) * mm, "end": v(-38.13, -41.74) * mm});
            skLineSegment(sketch, "E1262", {"start": v(-38.13, -41.74) * mm, "end": v(-38.23, -42.13) * mm});
            skLineSegment(sketch, "E1263", {"start": v(-38.23, -42.13) * mm, "end": v(-38.32, -42.52) * mm});
            skLineSegment(sketch, "E1264", {"start": v(-38.32, -42.52) * mm, "end": v(-38.22, -42.73) * mm});
            skLineSegment(sketch, "E1265", {"start": v(-38.22, -42.73) * mm, "end": v(-36.18, -44.47) * mm});
            skLineSegment(sketch, "E1266", {"start": v(-36.18, -44.47) * mm, "end": v(-35.96, -44.53) * mm});
            skLineSegment(sketch, "E1267", {"start": v(-35.96, -44.53) * mm, "end": v(-35.59, -44.38) * mm});
            skLineSegment(sketch, "E1268", {"start": v(-35.59, -44.38) * mm, "end": v(-35.22, -44.23) * mm});
            skLineSegment(sketch, "E1269", {"start": v(-35.22, -44.23) * mm, "end": v(-34.87, -44.07) * mm});
            skLineSegment(sketch, "E1270", {"start": v(-34.87, -44.07) * mm, "end": v(-34.52, -43.92) * mm});
            skLineSegment(sketch, "E1271", {"start": v(-34.52, -43.92) * mm, "end": v(-34.2, -43.76) * mm});
            skLineSegment(sketch, "E1272", {"start": v(-34.2, -43.76) * mm, "end": v(-33.87, -43.6) * mm});
            skLineSegment(sketch, "E1273", {"start": v(-33.87, -43.6) * mm, "end": v(-33.57, -43.45) * mm});
            skLineSegment(sketch, "E1274", {"start": v(-33.57, -43.45) * mm, "end": v(-33.27, -43.3) * mm});
            skLineSegment(sketch, "E1275", {"start": v(-33.27, -43.3) * mm, "end": v(-32.99, -43.14) * mm});
            skLineSegment(sketch, "E1276", {"start": v(-32.99, -43.14) * mm, "end": v(-32.72, -43) * mm});
            skLineSegment(sketch, "E1277", {"start": v(-32.72, -43) * mm, "end": v(-32.46, -42.84) * mm});
            skLineSegment(sketch, "E1278", {"start": v(-32.46, -42.84) * mm, "end": v(-32.2, -42.7) * mm});
            skLineSegment(sketch, "E1279", {"start": v(-32.2, -42.7) * mm, "end": v(-31.97, -42.54) * mm});
            skLineSegment(sketch, "E1280", {"start": v(-31.97, -42.54) * mm, "end": v(-31.74, -42.4) * mm});
            skLineSegment(sketch, "E1281", {"start": v(-31.74, -42.4) * mm, "end": v(-31.52, -42.25) * mm});
            skLineSegment(sketch, "E1282", {"start": v(-31.52, -42.25) * mm, "end": v(-31.32, -42.11) * mm});
            skLineSegment(sketch, "E1283", {"start": v(-31.32, -42.11) * mm, "end": v(-31.12, -41.98) * mm});
            skLineSegment(sketch, "E1284", {"start": v(-31.12, -41.98) * mm, "end": v(-30.94, -41.84) * mm});
            skLineSegment(sketch, "E1285", {"start": v(-30.94, -41.84) * mm, "end": v(-30.76, -41.71) * mm});
            skLineSegment(sketch, "E1286", {"start": v(-30.76, -41.71) * mm, "end": v(-30.6, -41.58) * mm});
            skLineSegment(sketch, "E1287", {"start": v(-30.6, -41.58) * mm, "end": v(-30.44, -41.46) * mm});
            skLineSegment(sketch, "E1288", {"start": v(-30.44, -41.46) * mm, "end": v(-30.3, -41.34) * mm});
            skLineSegment(sketch, "E1289", {"start": v(-30.3, -41.34) * mm, "end": v(-30.17, -41.23) * mm});
            skLineSegment(sketch, "E1290", {"start": v(-30.17, -41.23) * mm, "end": v(-30.04, -41.12) * mm});
            skLineSegment(sketch, "E1291", {"start": v(-30.04, -41.12) * mm, "end": v(-29.93, -41.02) * mm});
            skLineSegment(sketch, "E1292", {"start": v(-29.93, -41.02) * mm, "end": v(-29.82, -40.92) * mm});
            skLineSegment(sketch, "E1293", {"start": v(-29.82, -40.92) * mm, "end": v(-29.72, -40.83) * mm});
            skLineSegment(sketch, "E1294", {"start": v(-29.72, -40.83) * mm, "end": v(-29.63, -40.74) * mm});
            skLineSegment(sketch, "E1295", {"start": v(-29.63, -40.74) * mm, "end": v(-29.55, -40.66) * mm});
            skLineSegment(sketch, "E1296", {"start": v(-29.55, -40.66) * mm, "end": v(-29.48, -40.6) * mm});
            skLineSegment(sketch, "E1297", {"start": v(-29.48, -40.6) * mm, "end": v(-29.42, -40.52) * mm});
            skLineSegment(sketch, "E1298", {"start": v(-29.42, -40.52) * mm, "end": v(-29.37, -40.46) * mm});
            skLineSegment(sketch, "E1299", {"start": v(-29.37, -40.46) * mm, "end": v(-29.32, -40.41) * mm});
            skLineSegment(sketch, "E1300", {"start": v(-29.32, -40.41) * mm, "end": v(-29.28, -40.37) * mm});
            skLineSegment(sketch, "E1301", {"start": v(-29.28, -40.37) * mm, "end": v(-29.25, -40.33) * mm});
            skLineSegment(sketch, "E1302", {"start": v(-29.25, -40.33) * mm, "end": v(-29.22, -40.3) * mm});
            skLineSegment(sketch, "E1303", {"start": v(-29.22, -40.3) * mm, "end": v(-29.2, -40.28) * mm});
            skLineSegment(sketch, "E1304", {"start": v(-29.2, -40.28) * mm, "end": v(-29.2, -40.26) * mm});
            skLineSegment(sketch, "E1305", {"start": v(-29.2, -40.26) * mm, "end": v(-28.09, -38.73) * mm});
            skLineSegment(sketch, "E1306", {"start": v(-28.09, -38.73) * mm, "end": v(-23.92, -41.43) * mm});
            skLineSegment(sketch, "E1307", {"start": v(-23.92, -41.43) * mm, "end": v(-24.87, -43.07) * mm});
            skLineSegment(sketch, "E1308", {"start": v(-24.87, -43.07) * mm, "end": v(-24.87, -43.09) * mm});
            skLineSegment(sketch, "E1309", {"start": v(-24.87, -43.09) * mm, "end": v(-24.89, -43.11) * mm});
            skLineSegment(sketch, "E1310", {"start": v(-24.89, -43.11) * mm, "end": v(-24.9, -43.15) * mm});
            skLineSegment(sketch, "E1311", {"start": v(-24.9, -43.15) * mm, "end": v(-24.93, -43.2) * mm});
            skLineSegment(sketch, "E1312", {"start": v(-24.93, -43.2) * mm, "end": v(-24.95, -43.24) * mm});
            skLineSegment(sketch, "E1313", {"start": v(-24.95, -43.24) * mm, "end": v(-24.98, -43.3) * mm});
            skLineSegment(sketch, "E1314", {"start": v(-24.98, -43.3) * mm, "end": v(-25.01, -43.38) * mm});
            skLineSegment(sketch, "E1315", {"start": v(-25.01, -43.38) * mm, "end": v(-25.05, -43.47) * mm});
            skLineSegment(sketch, "E1316", {"start": v(-25.05, -43.47) * mm, "end": v(-25.09, -43.56) * mm});
            skLineSegment(sketch, "E1317", {"start": v(-25.09, -43.56) * mm, "end": v(-25.13, -43.67) * mm});
            skLineSegment(sketch, "E1318", {"start": v(-25.13, -43.67) * mm, "end": v(-25.17, -43.78) * mm});
            skLineSegment(sketch, "E1319", {"start": v(-25.17, -43.78) * mm, "end": v(-25.22, -43.9) * mm});
            skLineSegment(sketch, "E1320", {"start": v(-25.22, -43.9) * mm, "end": v(-25.26, -44.04) * mm});
            skLineSegment(sketch, "E1321", {"start": v(-25.26, -44.04) * mm, "end": v(-25.3, -44.2) * mm});
            skLineSegment(sketch, "E1322", {"start": v(-25.3, -44.2) * mm, "end": v(-25.36, -44.35) * mm});
            skLineSegment(sketch, "E1323", {"start": v(-25.36, -44.35) * mm, "end": v(-25.4, -44.52) * mm});
            skLineSegment(sketch, "E1324", {"start": v(-25.4, -44.52) * mm, "end": v(-25.45, -44.7) * mm});
            skLineSegment(sketch, "E1325", {"start": v(-25.45, -44.7) * mm, "end": v(-25.5, -44.89) * mm});
            skLineSegment(sketch, "E1326", {"start": v(-25.5, -44.89) * mm, "end": v(-25.55, -45.1) * mm});
            skLineSegment(sketch, "E1327", {"start": v(-25.55, -45.1) * mm, "end": v(-25.6, -45.3) * mm});
            skLineSegment(sketch, "E1328", {"start": v(-25.6, -45.3) * mm, "end": v(-25.65, -45.53) * mm});
            skLineSegment(sketch, "E1329", {"start": v(-25.65, -45.53) * mm, "end": v(-25.7, -45.76) * mm});
            skLineSegment(sketch, "E1330", {"start": v(-25.7, -45.76) * mm, "end": v(-25.74, -46) * mm});
            skLineSegment(sketch, "E1331", {"start": v(-25.74, -46) * mm, "end": v(-25.78, -46.26) * mm});
            skLineSegment(sketch, "E1332", {"start": v(-25.78, -46.26) * mm, "end": v(-25.82, -46.53) * mm});
            skLineSegment(sketch, "E1333", {"start": v(-25.82, -46.53) * mm, "end": v(-25.86, -46.8) * mm});
            skLineSegment(sketch, "E1334", {"start": v(-25.86, -46.8) * mm, "end": v(-25.9, -47.1) * mm});
            skLineSegment(sketch, "E1335", {"start": v(-25.9, -47.1) * mm, "end": v(-25.92, -47.4) * mm});
            skLineSegment(sketch, "E1336", {"start": v(-25.92, -47.4) * mm, "end": v(-25.95, -47.7) * mm});
            skLineSegment(sketch, "E1337", {"start": v(-25.95, -47.7) * mm, "end": v(-25.98, -48.03) * mm});
            skLineSegment(sketch, "E1338", {"start": v(-25.98, -48.03) * mm, "end": v(-26, -48.36) * mm});
            skLineSegment(sketch, "E1339", {"start": v(-26, -48.36) * mm, "end": v(-26.02, -48.7) * mm});
            skLineSegment(sketch, "E1340", {"start": v(-26.02, -48.7) * mm, "end": v(-26.03, -49.06) * mm});
            skLineSegment(sketch, "E1341", {"start": v(-26.03, -49.06) * mm, "end": v(-26.03, -49.43) * mm});
            skLineSegment(sketch, "E1342", {"start": v(-26.03, -49.43) * mm, "end": v(-26.04, -49.8) * mm});
            skLineSegment(sketch, "E1343", {"start": v(-26.04, -49.8) * mm, "end": v(-26.03, -50.19) * mm});
            skLineSegment(sketch, "E1344", {"start": v(-26.03, -50.19) * mm, "end": v(-26.02, -50.58) * mm});
            skLineSegment(sketch, "E1345", {"start": v(-26.02, -50.58) * mm, "end": v(-26, -51) * mm});
            skLineSegment(sketch, "E1346", {"start": v(-26, -51) * mm, "end": v(-25.86, -51.16) * mm});
            skLineSegment(sketch, "E1347", {"start": v(-25.86, -51.16) * mm, "end": v(-23.44, -52.32) * mm});
            skLineSegment(sketch, "E1348", {"start": v(-23.44, -52.32) * mm, "end": v(-23.21, -52.32) * mm});
            skLineSegment(sketch, "E1349", {"start": v(-23.21, -52.32) * mm, "end": v(-22.89, -52.08) * mm});
            skLineSegment(sketch, "E1350", {"start": v(-22.89, -52.08) * mm, "end": v(-22.57, -51.83) * mm});
            skLineSegment(sketch, "E1351", {"start": v(-22.57, -51.83) * mm, "end": v(-22.27, -51.6) * mm});
            skLineSegment(sketch, "E1352", {"start": v(-22.27, -51.6) * mm, "end": v(-21.98, -51.36) * mm});
            skLineSegment(sketch, "E1353", {"start": v(-21.98, -51.36) * mm, "end": v(-21.7, -51.12) * mm});
            skLineSegment(sketch, "E1354", {"start": v(-21.7, -51.12) * mm, "end": v(-21.43, -50.89) * mm});
            skLineSegment(sketch, "E1355", {"start": v(-21.43, -50.89) * mm, "end": v(-21.18, -50.66) * mm});
            skLineSegment(sketch, "E1356", {"start": v(-21.18, -50.66) * mm, "end": v(-20.93, -50.43) * mm});
            skLineSegment(sketch, "E1357", {"start": v(-20.93, -50.43) * mm, "end": v(-20.7, -50.21) * mm});
            skLineSegment(sketch, "E1358", {"start": v(-20.7, -50.21) * mm, "end": v(-20.47, -50) * mm});
            skLineSegment(sketch, "E1359", {"start": v(-20.47, -50) * mm, "end": v(-20.26, -49.78) * mm});
            skLineSegment(sketch, "E1360", {"start": v(-20.26, -49.78) * mm, "end": v(-20.06, -49.57) * mm});
            skLineSegment(sketch, "E1361", {"start": v(-20.06, -49.57) * mm, "end": v(-19.87, -49.37) * mm});
            skLineSegment(sketch, "E1362", {"start": v(-19.87, -49.37) * mm, "end": v(-19.68, -49.17) * mm});
            skLineSegment(sketch, "E1363", {"start": v(-19.68, -49.17) * mm, "end": v(-19.51, -48.97) * mm});
            skLineSegment(sketch, "E1364", {"start": v(-19.51, -48.97) * mm, "end": v(-19.35, -48.78) * mm});
            skLineSegment(sketch, "E1365", {"start": v(-19.35, -48.78) * mm, "end": v(-19.2, -48.6) * mm});
            skLineSegment(sketch, "E1366", {"start": v(-19.2, -48.6) * mm, "end": v(-19.05, -48.42) * mm});
            skLineSegment(sketch, "E1367", {"start": v(-19.05, -48.42) * mm, "end": v(-18.92, -48.25) * mm});
            skLineSegment(sketch, "E1368", {"start": v(-18.92, -48.25) * mm, "end": v(-18.8, -48.09) * mm});
            skLineSegment(sketch, "E1369", {"start": v(-18.8, -48.09) * mm, "end": v(-18.68, -47.93) * mm});
            skLineSegment(sketch, "E1370", {"start": v(-18.68, -47.93) * mm, "end": v(-18.57, -47.78) * mm});
            skLineSegment(sketch, "E1371", {"start": v(-18.57, -47.78) * mm, "end": v(-18.47, -47.63) * mm});
            skLineSegment(sketch, "E1372", {"start": v(-18.47, -47.63) * mm, "end": v(-18.37, -47.5) * mm});
            skLineSegment(sketch, "E1373", {"start": v(-18.37, -47.5) * mm, "end": v(-18.29, -47.37) * mm});
            skLineSegment(sketch, "E1374", {"start": v(-18.29, -47.37) * mm, "end": v(-18.21, -47.24) * mm});
            skLineSegment(sketch, "E1375", {"start": v(-18.21, -47.24) * mm, "end": v(-18.14, -47.13) * mm});
            skLineSegment(sketch, "E1376", {"start": v(-18.14, -47.13) * mm, "end": v(-18.08, -47.03) * mm});
            skLineSegment(sketch, "E1377", {"start": v(-18.08, -47.03) * mm, "end": v(-18.02, -46.93) * mm});
            skLineSegment(sketch, "E1378", {"start": v(-18.02, -46.93) * mm, "end": v(-17.97, -46.84) * mm});
            skLineSegment(sketch, "E1379", {"start": v(-17.97, -46.84) * mm, "end": v(-17.93, -46.76) * mm});
            skLineSegment(sketch, "E1380", {"start": v(-17.93, -46.76) * mm, "end": v(-17.9, -46.69) * mm});
            skLineSegment(sketch, "E1381", {"start": v(-17.9, -46.69) * mm, "end": v(-17.86, -46.62) * mm});
            skLineSegment(sketch, "E1382", {"start": v(-17.86, -46.62) * mm, "end": v(-17.84, -46.57) * mm});
            skLineSegment(sketch, "E1383", {"start": v(-17.84, -46.57) * mm, "end": v(-17.82, -46.52) * mm});
            skLineSegment(sketch, "E1384", {"start": v(-17.82, -46.52) * mm, "end": v(-17.8, -46.49) * mm});
            skLineSegment(sketch, "E1385", {"start": v(-17.8, -46.49) * mm, "end": v(-17.79, -46.46) * mm});
            skLineSegment(sketch, "E1386", {"start": v(-17.79, -46.46) * mm, "end": v(-17.78, -46.45) * mm});
            skLineSegment(sketch, "E1387", {"start": v(-17.78, -46.45) * mm, "end": v(-17.1, -44.68) * mm});
            skLineSegment(sketch, "E1388", {"start": v(-17.1, -44.68) * mm, "end": v(-12.38, -46.22) * mm});
            skLineSegment(sketch, "E1389", {"start": v(-12.38, -46.22) * mm, "end": v(-12.87, -48.04) * mm});
            skLineSegment(sketch, "E1390", {"start": v(-12.87, -48.04) * mm, "end": v(-12.88, -48.06) * mm});
            skLineSegment(sketch, "E1391", {"start": v(-12.88, -48.06) * mm, "end": v(-12.88, -48.08) * mm});
            skLineSegment(sketch, "E1392", {"start": v(-12.88, -48.08) * mm, "end": v(-12.9, -48.12) * mm});
            skLineSegment(sketch, "E1393", {"start": v(-12.9, -48.12) * mm, "end": v(-12.9, -48.17) * mm});
            skLineSegment(sketch, "E1394", {"start": v(-12.9, -48.17) * mm, "end": v(-12.91, -48.23) * mm});
            skLineSegment(sketch, "E1395", {"start": v(-12.91, -48.23) * mm, "end": v(-12.92, -48.3) * mm});
            skLineSegment(sketch, "E1396", {"start": v(-12.92, -48.3) * mm, "end": v(-12.93, -48.38) * mm});
            skLineSegment(sketch, "E1397", {"start": v(-12.93, -48.38) * mm, "end": v(-12.95, -48.47) * mm});
            skLineSegment(sketch, "E1398", {"start": v(-12.95, -48.47) * mm, "end": v(-12.96, -48.57) * mm});
            skLineSegment(sketch, "E1399", {"start": v(-12.96, -48.57) * mm, "end": v(-12.97, -48.68) * mm});
            skLineSegment(sketch, "E1400", {"start": v(-12.97, -48.68) * mm, "end": v(-12.98, -48.8) * mm});
            skLineSegment(sketch, "E1401", {"start": v(-12.98, -48.8) * mm, "end": v(-13, -48.94) * mm});
            skLineSegment(sketch, "E1402", {"start": v(-13, -48.94) * mm, "end": v(-13, -49.08) * mm});
            skLineSegment(sketch, "E1403", {"start": v(-13, -49.08) * mm, "end": v(-13, -49.24) * mm});
            skLineSegment(sketch, "E1404", {"start": v(-13, -49.24) * mm, "end": v(-13.01, -49.4) * mm});
            skLineSegment(sketch, "E1405", {"start": v(-13.01, -49.4) * mm, "end": v(-13.02, -49.58) * mm});
            skLineSegment(sketch, "E1406", {"start": v(-13.02, -49.58) * mm, "end": v(-13.02, -49.76) * mm});
            skLineSegment(sketch, "E1407", {"start": v(-13.02, -49.76) * mm, "end": v(-13.02, -49.96) * mm});
            skLineSegment(sketch, "E1408", {"start": v(-13.02, -49.96) * mm, "end": v(-13.01, -50.17) * mm});
            skLineSegment(sketch, "E1409", {"start": v(-13.01, -50.17) * mm, "end": v(-13, -50.39) * mm});
            skLineSegment(sketch, "E1410", {"start": v(-13, -50.39) * mm, "end": v(-12.99, -50.61) * mm});
            skLineSegment(sketch, "E1411", {"start": v(-12.99, -50.61) * mm, "end": v(-12.97, -50.85) * mm});
            skLineSegment(sketch, "E1412", {"start": v(-12.97, -50.85) * mm, "end": v(-12.95, -51.1) * mm});
            skLineSegment(sketch, "E1413", {"start": v(-12.95, -51.1) * mm, "end": v(-12.93, -51.36) * mm});
            skLineSegment(sketch, "E1414", {"start": v(-12.93, -51.36) * mm, "end": v(-12.9, -51.63) * mm});
            skLineSegment(sketch, "E1415", {"start": v(-12.9, -51.63) * mm, "end": v(-12.86, -51.9) * mm});
            skLineSegment(sketch, "E1416", {"start": v(-12.86, -51.9) * mm, "end": v(-12.82, -52.2) * mm});
            skLineSegment(sketch, "E1417", {"start": v(-12.82, -52.2) * mm, "end": v(-12.77, -52.5) * mm});
            skLineSegment(sketch, "E1418", {"start": v(-12.77, -52.5) * mm, "end": v(-12.72, -52.8) * mm});
            skLineSegment(sketch, "E1419", {"start": v(-12.72, -52.8) * mm, "end": v(-12.66, -53.12) * mm});
            skLineSegment(sketch, "E1420", {"start": v(-12.66, -53.12) * mm, "end": v(-12.6, -53.44) * mm});
            skLineSegment(sketch, "E1421", {"start": v(-12.6, -53.44) * mm, "end": v(-12.52, -53.78) * mm});
            skLineSegment(sketch, "E1422", {"start": v(-12.52, -53.78) * mm, "end": v(-12.44, -54.13) * mm});
            skLineSegment(sketch, "E1423", {"start": v(-12.44, -54.13) * mm, "end": v(-12.36, -54.48) * mm});
            skLineSegment(sketch, "E1424", {"start": v(-12.36, -54.48) * mm, "end": v(-12.26, -54.84) * mm});
            skLineSegment(sketch, "E1425", {"start": v(-12.26, -54.84) * mm, "end": v(-12.16, -55.22) * mm});
            skLineSegment(sketch, "E1426", {"start": v(-12.16, -55.22) * mm, "end": v(-12.04, -55.6) * mm});
            skLineSegment(sketch, "E1427", {"start": v(-12.04, -55.6) * mm, "end": v(-11.92, -55.98) * mm});
            skLineSegment(sketch, "E1428", {"start": v(-11.92, -55.98) * mm, "end": v(-11.74, -56.11) * mm});
            skLineSegment(sketch, "E1429", {"start": v(-11.74, -56.11) * mm, "end": v(-9.1, -56.6) * mm});
            skLineSegment(sketch, "E1430", {"start": v(-9.1, -56.6) * mm, "end": v(-8.88, -56.55) * mm});
            skLineSegment(sketch, "E1431", {"start": v(-8.88, -56.55) * mm, "end": v(-8.63, -56.23) * mm});
            skLineSegment(sketch, "E1432", {"start": v(-8.63, -56.23) * mm, "end": v(-8.39, -55.91) * mm});
            skLineSegment(sketch, "E1433", {"start": v(-8.39, -55.91) * mm, "end": v(-8.16, -55.6) * mm});
            skLineSegment(sketch, "E1434", {"start": v(-8.16, -55.6) * mm, "end": v(-7.94, -55.3) * mm});
            skLineSegment(sketch, "E1435", {"start": v(-7.94, -55.3) * mm, "end": v(-7.73, -55) * mm});
            skLineSegment(sketch, "E1436", {"start": v(-7.73, -55) * mm, "end": v(-7.53, -54.7) * mm});
            skLineSegment(sketch, "E1437", {"start": v(-7.53, -54.7) * mm, "end": v(-7.34, -54.41) * mm});
            skLineSegment(sketch, "E1438", {"start": v(-7.34, -54.41) * mm, "end": v(-7.17, -54.13) * mm});
            skLineSegment(sketch, "E1439", {"start": v(-7.17, -54.13) * mm, "end": v(-7, -53.86) * mm});
            skLineSegment(sketch, "E1440", {"start": v(-7, -53.86) * mm, "end": v(-6.84, -53.59) * mm});
            skLineSegment(sketch, "E1441", {"start": v(-6.84, -53.59) * mm, "end": v(-6.69, -53.33) * mm});
            skLineSegment(sketch, "E1442", {"start": v(-6.69, -53.33) * mm, "end": v(-6.55, -53.07) * mm});
            skLineSegment(sketch, "E1443", {"start": v(-6.55, -53.07) * mm, "end": v(-6.41, -52.83) * mm});
            skLineSegment(sketch, "E1444", {"start": v(-6.41, -52.83) * mm, "end": v(-6.29, -52.59) * mm});
            skLineSegment(sketch, "E1445", {"start": v(-6.29, -52.59) * mm, "end": v(-6.17, -52.35) * mm});
            skLineSegment(sketch, "E1446", {"start": v(-6.17, -52.35) * mm, "end": v(-6.06, -52.13) * mm});
            skLineSegment(sketch, "E1447", {"start": v(-6.06, -52.13) * mm, "end": v(-5.96, -51.91) * mm});
            skLineSegment(sketch, "E1448", {"start": v(-5.96, -51.91) * mm, "end": v(-5.87, -51.7) * mm});
            skLineSegment(sketch, "E1449", {"start": v(-5.87, -51.7) * mm, "end": v(-5.78, -51.5) * mm});
            skLineSegment(sketch, "E1450", {"start": v(-5.78, -51.5) * mm, "end": v(-5.7, -51.31) * mm});
            skLineSegment(sketch, "E1451", {"start": v(-5.7, -51.31) * mm, "end": v(-5.63, -51.13) * mm});
            skLineSegment(sketch, "E1452", {"start": v(-5.63, -51.13) * mm, "end": v(-5.57, -50.95) * mm});
            skLineSegment(sketch, "E1453", {"start": v(-5.57, -50.95) * mm, "end": v(-5.5, -50.79) * mm});
            skLineSegment(sketch, "E1454", {"start": v(-5.5, -50.79) * mm, "end": v(-5.45, -50.63) * mm});
            skLineSegment(sketch, "E1455", {"start": v(-5.45, -50.63) * mm, "end": v(-5.4, -50.49) * mm});
            skLineSegment(sketch, "E1456", {"start": v(-5.4, -50.49) * mm, "end": v(-5.36, -50.35) * mm});
            skLineSegment(sketch, "E1457", {"start": v(-5.36, -50.35) * mm, "end": v(-5.32, -50.22) * mm});
            skLineSegment(sketch, "E1458", {"start": v(-5.32, -50.22) * mm, "end": v(-5.3, -50.1) * mm});
            skLineSegment(sketch, "E1459", {"start": v(-5.3, -50.1) * mm, "end": v(-5.26, -50) * mm});
            skLineSegment(sketch, "E1460", {"start": v(-5.26, -50) * mm, "end": v(-5.24, -49.9) * mm});
            skLineSegment(sketch, "E1461", {"start": v(-5.24, -49.9) * mm, "end": v(-5.22, -49.8) * mm});
            skLineSegment(sketch, "E1462", {"start": v(-5.22, -49.8) * mm, "end": v(-5.2, -49.73) * mm});
            skLineSegment(sketch, "E1463", {"start": v(-5.2, -49.73) * mm, "end": v(-5.19, -49.66) * mm});
            skLineSegment(sketch, "E1464", {"start": v(-5.19, -49.66) * mm, "end": v(-5.17, -49.6) * mm});
            skLineSegment(sketch, "E1465", {"start": v(-5.17, -49.6) * mm, "end": v(-5.17, -49.55) * mm});
            skLineSegment(sketch, "E1466", {"start": v(-5.17, -49.55) * mm, "end": v(-5.16, -49.48) * mm});
            skLineSegment(sketch, "E1467", {"start": v(-5.16, -49.48) * mm, "end": v(-5.15, -49.46) * mm});
            skLineSegment(sketch, "E1468", {"start": v(-5.15, -49.46) * mm, "end": v(-4.96, -47.59) * mm});
            skLineSegment(sketch, "E1469", {"start": v(-4.96, -47.59) * mm, "end": v(0, -47.85) * mm});
            skLineSegment(sketch, "E1470", {"start": v(0, -47.85) * mm, "end": v(0, -49.75) * mm});
            skLineSegment(sketch, "E1471", {"start": v(0, -49.75) * mm, "end": v(0, -49.78) * mm});
            skLineSegment(sketch, "E1472", {"start": v(0, -49.78) * mm, "end": v(0, -49.82) * mm});
            skLineSegment(sketch, "E1473", {"start": v(0, -49.82) * mm, "end": v(0, -49.87) * mm});
            skLineSegment(sketch, "E1474", {"start": v(0, -49.87) * mm, "end": v(0.01, -49.93) * mm});
            skLineSegment(sketch, "E1475", {"start": v(0.01, -49.93) * mm, "end": v(0.02, -50) * mm});
            skLineSegment(sketch, "E1476", {"start": v(0.02, -50) * mm, "end": v(0.03, -50.08) * mm});
            skLineSegment(sketch, "E1477", {"start": v(0.03, -50.08) * mm, "end": v(0.04, -50.17) * mm});
            skLineSegment(sketch, "E1478", {"start": v(0.04, -50.17) * mm, "end": v(0.05, -50.27) * mm});
            skLineSegment(sketch, "E1479", {"start": v(0.05, -50.27) * mm, "end": v(0.07, -50.38) * mm});
            skLineSegment(sketch, "E1480", {"start": v(0.07, -50.38) * mm, "end": v(0.1, -50.5) * mm});
            skLineSegment(sketch, "E1481", {"start": v(0.1, -50.5) * mm, "end": v(0.12, -50.63) * mm});
            skLineSegment(sketch, "E1482", {"start": v(0.12, -50.63) * mm, "end": v(0.15, -50.78) * mm});
            skLineSegment(sketch, "E1483", {"start": v(0.15, -50.78) * mm, "end": v(0.18, -50.93) * mm});
            skLineSegment(sketch, "E1484", {"start": v(0.18, -50.93) * mm, "end": v(0.21, -51.09) * mm});
            skLineSegment(sketch, "E1485", {"start": v(0.21, -51.09) * mm, "end": v(0.26, -51.26) * mm});
            skLineSegment(sketch, "E1486", {"start": v(0.26, -51.26) * mm, "end": v(0.3, -51.44) * mm});
            skLineSegment(sketch, "E1487", {"start": v(0.3, -51.44) * mm, "end": v(0.36, -51.63) * mm});
            skLineSegment(sketch, "E1488", {"start": v(0.36, -51.63) * mm, "end": v(0.42, -51.83) * mm});
            skLineSegment(sketch, "E1489", {"start": v(0.42, -51.83) * mm, "end": v(0.48, -52.03) * mm});
            skLineSegment(sketch, "E1490", {"start": v(0.48, -52.03) * mm, "end": v(0.55, -52.25) * mm});
            skLineSegment(sketch, "E1491", {"start": v(0.55, -52.25) * mm, "end": v(0.63, -52.48) * mm});
            skLineSegment(sketch, "E1492", {"start": v(0.63, -52.48) * mm, "end": v(0.71, -52.71) * mm});
            skLineSegment(sketch, "E1493", {"start": v(0.71, -52.71) * mm, "end": v(0.8, -52.95) * mm});
            skLineSegment(sketch, "E1494", {"start": v(0.8, -52.95) * mm, "end": v(0.9, -53.2) * mm});
            skLineSegment(sketch, "E1495", {"start": v(0.9, -53.2) * mm, "end": v(1, -53.47) * mm});
            skLineSegment(sketch, "E1496", {"start": v(1, -53.47) * mm, "end": v(1.12, -53.73) * mm});
            skLineSegment(sketch, "E1497", {"start": v(1.12, -53.73) * mm, "end": v(1.25, -54) * mm});
            skLineSegment(sketch, "E1498", {"start": v(1.25, -54) * mm, "end": v(1.38, -54.3) * mm});
            skLineSegment(sketch, "E1499", {"start": v(1.38, -54.3) * mm, "end": v(1.52, -54.58) * mm});
            skLineSegment(sketch, "E1500", {"start": v(1.52, -54.58) * mm, "end": v(1.67, -54.88) * mm});
            skLineSegment(sketch, "E1501", {"start": v(1.67, -54.88) * mm, "end": v(1.82, -55.19) * mm});
            skLineSegment(sketch, "E1502", {"start": v(1.82, -55.19) * mm, "end": v(1.99, -55.5) * mm});
            skLineSegment(sketch, "E1503", {"start": v(1.99, -55.5) * mm, "end": v(2.17, -55.82) * mm});
            skLineSegment(sketch, "E1504", {"start": v(2.17, -55.82) * mm, "end": v(2.35, -56.15) * mm});
            skLineSegment(sketch, "E1505", {"start": v(2.35, -56.15) * mm, "end": v(2.55, -56.48) * mm});
            skLineSegment(sketch, "E1506", {"start": v(2.55, -56.48) * mm, "end": v(2.76, -56.82) * mm});
            skLineSegment(sketch, "E1507", {"start": v(2.76, -56.82) * mm, "end": v(2.97, -57.16) * mm});
            skLineSegment(sketch, "E1508", {"start": v(2.97, -57.16) * mm, "end": v(3.19, -57.24) * mm});
            skLineSegment(sketch, "E1509", {"start": v(3.19, -57.24) * mm, "end": v(5.86, -57.03) * mm});
            skLineSegment(sketch, "E1510", {"start": v(5.86, -57.03) * mm, "end": v(6.06, -56.92) * mm});
            skLineSegment(sketch, "E1511", {"start": v(6.06, -56.92) * mm, "end": v(6.22, -56.54) * mm});
            skLineSegment(sketch, "E1512", {"start": v(6.22, -56.54) * mm, "end": v(6.37, -56.18) * mm});
            skLineSegment(sketch, "E1513", {"start": v(6.37, -56.18) * mm, "end": v(6.5, -55.82) * mm});
            skLineSegment(sketch, "E1514", {"start": v(6.5, -55.82) * mm, "end": v(6.64, -55.47) * mm});
            skLineSegment(sketch, "E1515", {"start": v(6.64, -55.47) * mm, "end": v(6.77, -55.12) * mm});
            skLineSegment(sketch, "E1516", {"start": v(6.77, -55.12) * mm, "end": v(6.88, -54.79) * mm});
            skLineSegment(sketch, "E1517", {"start": v(6.88, -54.79) * mm, "end": v(6.99, -54.46) * mm});
            skLineSegment(sketch, "E1518", {"start": v(6.99, -54.46) * mm, "end": v(7.1, -54.14) * mm});
            skLineSegment(sketch, "E1519", {"start": v(7.1, -54.14) * mm, "end": v(7.18, -53.83) * mm});
            skLineSegment(sketch, "E1520", {"start": v(7.18, -53.83) * mm, "end": v(7.27, -53.53) * mm});
            skLineSegment(sketch, "E1521", {"start": v(7.27, -53.53) * mm, "end": v(7.34, -53.24) * mm});
            skLineSegment(sketch, "E1522", {"start": v(7.34, -53.24) * mm, "end": v(7.41, -52.96) * mm});
            skLineSegment(sketch, "E1523", {"start": v(7.41, -52.96) * mm, "end": v(7.48, -52.69) * mm});
            skLineSegment(sketch, "E1524", {"start": v(7.48, -52.69) * mm, "end": v(7.54, -52.42) * mm});
            skLineSegment(sketch, "E1525", {"start": v(7.54, -52.42) * mm, "end": v(7.59, -52.17) * mm});
            skLineSegment(sketch, "E1526", {"start": v(7.59, -52.17) * mm, "end": v(7.63, -51.92) * mm});
            skLineSegment(sketch, "E1527", {"start": v(7.63, -51.92) * mm, "end": v(7.68, -51.69) * mm});
            skLineSegment(sketch, "E1528", {"start": v(7.68, -51.69) * mm, "end": v(7.71, -51.46) * mm});
            skLineSegment(sketch, "E1529", {"start": v(7.71, -51.46) * mm, "end": v(7.74, -51.25) * mm});
            skLineSegment(sketch, "E1530", {"start": v(7.74, -51.25) * mm, "end": v(7.77, -51.04) * mm});
            skLineSegment(sketch, "E1531", {"start": v(7.77, -51.04) * mm, "end": v(7.8, -50.84) * mm});
            skLineSegment(sketch, "E1532", {"start": v(7.8, -50.84) * mm, "end": v(7.8, -50.66) * mm});
            skLineSegment(sketch, "E1533", {"start": v(7.8, -50.66) * mm, "end": v(7.82, -50.48) * mm});
            skLineSegment(sketch, "E1534", {"start": v(7.82, -50.48) * mm, "end": v(7.84, -50.32) * mm});
            skLineSegment(sketch, "E1535", {"start": v(7.84, -50.32) * mm, "end": v(7.85, -50.16) * mm});
            skLineSegment(sketch, "E1536", {"start": v(7.85, -50.16) * mm, "end": v(7.85, -50.02) * mm});
            skLineSegment(sketch, "E1537", {"start": v(7.85, -50.02) * mm, "end": v(7.86, -49.89) * mm});
            skLineSegment(sketch, "E1538", {"start": v(7.86, -49.89) * mm, "end": v(7.86, -49.77) * mm});
            skLineSegment(sketch, "E1539", {"start": v(7.86, -49.77) * mm, "end": v(7.86, -49.65) * mm});
            skLineSegment(sketch, "E1540", {"start": v(7.86, -49.65) * mm, "end": v(7.85, -49.55) * mm});
            skLineSegment(sketch, "E1541", {"start": v(7.85, -49.55) * mm, "end": v(7.85, -49.46) * mm});
            skLineSegment(sketch, "E1542", {"start": v(7.85, -49.46) * mm, "end": v(7.85, -49.38) * mm});
            skLineSegment(sketch, "E1543", {"start": v(7.85, -49.38) * mm, "end": v(7.84, -49.3) * mm});
            skLineSegment(sketch, "E1544", {"start": v(7.84, -49.3) * mm, "end": v(7.84, -49.25) * mm});
            skLineSegment(sketch, "E1545", {"start": v(7.84, -49.25) * mm, "end": v(7.83, -49.2) * mm});
            skLineSegment(sketch, "E1546", {"start": v(7.83, -49.2) * mm, "end": v(7.83, -49.16) * mm});
            skLineSegment(sketch, "E1547", {"start": v(7.83, -49.16) * mm, "end": v(7.83, -49.13) * mm});
            skLineSegment(sketch, "E1548", {"start": v(7.83, -49.13) * mm, "end": v(7.82, -49.11) * mm});
            skLineSegment(sketch, "E1549", {"start": v(7.82, -49.11) * mm, "end": v(7.53, -47.25) * mm});
            skLineSegment(sketch, "E1550", {"start": v(7.53, -47.25) * mm, "end": v(12.38, -46.22) * mm});
            skLineSegment(sketch, "E1551", {"start": v(12.38, -46.22) * mm, "end": v(12.87, -48.04) * mm});
            skLineSegment(sketch, "E1552", {"start": v(12.87, -48.04) * mm, "end": v(12.88, -48.05) * mm});
            skLineSegment(sketch, "E1553", {"start": v(12.88, -48.05) * mm, "end": v(12.89, -48.08) * mm});
            skLineSegment(sketch, "E1554", {"start": v(12.89, -48.08) * mm, "end": v(12.9, -48.12) * mm});
            skLineSegment(sketch, "E1555", {"start": v(12.9, -48.12) * mm, "end": v(12.91, -48.17) * mm});
            skLineSegment(sketch, "E1556", {"start": v(12.91, -48.17) * mm, "end": v(12.93, -48.22) * mm});
            skLineSegment(sketch, "E1557", {"start": v(12.93, -48.22) * mm, "end": v(12.96, -48.29) * mm});
            skLineSegment(sketch, "E1558", {"start": v(12.96, -48.29) * mm, "end": v(12.99, -48.36) * mm});
            skLineSegment(sketch, "E1559", {"start": v(12.99, -48.36) * mm, "end": v(13.02, -48.45) * mm});
            skLineSegment(sketch, "E1560", {"start": v(13.02, -48.45) * mm, "end": v(13.06, -48.54) * mm});
            skLineSegment(sketch, "E1561", {"start": v(13.06, -48.54) * mm, "end": v(13.1, -48.65) * mm});
            skLineSegment(sketch, "E1562", {"start": v(13.1, -48.65) * mm, "end": v(13.16, -48.76) * mm});
            skLineSegment(sketch, "E1563", {"start": v(13.16, -48.76) * mm, "end": v(13.22, -48.88) * mm});
            skLineSegment(sketch, "E1564", {"start": v(13.22, -48.88) * mm, "end": v(13.28, -49) * mm});
            skLineSegment(sketch, "E1565", {"start": v(13.28, -49) * mm, "end": v(13.35, -49.14) * mm});
            skLineSegment(sketch, "E1566", {"start": v(13.35, -49.14) * mm, "end": v(13.43, -49.29) * mm});
            skLineSegment(sketch, "E1567", {"start": v(13.43, -49.29) * mm, "end": v(13.52, -49.44) * mm});
            skLineSegment(sketch, "E1568", {"start": v(13.52, -49.44) * mm, "end": v(13.6, -49.6) * mm});
            skLineSegment(sketch, "E1569", {"start": v(13.6, -49.6) * mm, "end": v(13.7, -49.77) * mm});
            skLineSegment(sketch, "E1570", {"start": v(13.7, -49.77) * mm, "end": v(13.82, -49.95) * mm});
            skLineSegment(sketch, "E1571", {"start": v(13.82, -49.95) * mm, "end": v(13.93, -50.14) * mm});
            skLineSegment(sketch, "E1572", {"start": v(13.93, -50.14) * mm, "end": v(14.06, -50.33) * mm});
            skLineSegment(sketch, "E1573", {"start": v(14.06, -50.33) * mm, "end": v(14.19, -50.53) * mm});
            skLineSegment(sketch, "E1574", {"start": v(14.19, -50.53) * mm, "end": v(14.33, -50.73) * mm});
            skLineSegment(sketch, "E1575", {"start": v(14.33, -50.73) * mm, "end": v(14.48, -50.94) * mm});
            skLineSegment(sketch, "E1576", {"start": v(14.48, -50.94) * mm, "end": v(14.64, -51.16) * mm});
            skLineSegment(sketch, "E1577", {"start": v(14.64, -51.16) * mm, "end": v(14.81, -51.38) * mm});
            skLineSegment(sketch, "E1578", {"start": v(14.81, -51.38) * mm, "end": v(15, -51.61) * mm});
            skLineSegment(sketch, "E1579", {"start": v(15, -51.61) * mm, "end": v(15.18, -51.85) * mm});
            skLineSegment(sketch, "E1580", {"start": v(15.18, -51.85) * mm, "end": v(15.38, -52.09) * mm});
            skLineSegment(sketch, "E1581", {"start": v(15.38, -52.09) * mm, "end": v(15.6, -52.33) * mm});
            skLineSegment(sketch, "E1582", {"start": v(15.6, -52.33) * mm, "end": v(15.81, -52.58) * mm});
            skLineSegment(sketch, "E1583", {"start": v(15.81, -52.58) * mm, "end": v(16.04, -52.84) * mm});
            skLineSegment(sketch, "E1584", {"start": v(16.04, -52.84) * mm, "end": v(16.29, -53.1) * mm});
            skLineSegment(sketch, "E1585", {"start": v(16.29, -53.1) * mm, "end": v(16.54, -53.36) * mm});
            skLineSegment(sketch, "E1586", {"start": v(16.54, -53.36) * mm, "end": v(16.8, -53.62) * mm});
            skLineSegment(sketch, "E1587", {"start": v(16.8, -53.62) * mm, "end": v(17.08, -53.9) * mm});
            skLineSegment(sketch, "E1588", {"start": v(17.08, -53.9) * mm, "end": v(17.37, -54.17) * mm});
            skLineSegment(sketch, "E1589", {"start": v(17.37, -54.17) * mm, "end": v(17.67, -54.44) * mm});
            skLineSegment(sketch, "E1590", {"start": v(17.67, -54.44) * mm, "end": v(17.9, -54.46) * mm});
            skLineSegment(sketch, "E1591", {"start": v(17.9, -54.46) * mm, "end": v(20.42, -53.57) * mm});
            skLineSegment(sketch, "E1592", {"start": v(20.42, -53.57) * mm, "end": v(20.58, -53.41) * mm});
            skLineSegment(sketch, "E1593", {"start": v(20.58, -53.41) * mm, "end": v(20.64, -53) * mm});
            skLineSegment(sketch, "E1594", {"start": v(20.64, -53) * mm, "end": v(20.7, -52.61) * mm});
            skLineSegment(sketch, "E1595", {"start": v(20.7, -52.61) * mm, "end": v(20.74, -52.23) * mm});
            skLineSegment(sketch, "E1596", {"start": v(20.74, -52.23) * mm, "end": v(20.77, -51.86) * mm});
            skLineSegment(sketch, "E1597", {"start": v(20.77, -51.86) * mm, "end": v(20.8, -51.5) * mm});
            skLineSegment(sketch, "E1598", {"start": v(20.8, -51.5) * mm, "end": v(20.83, -51.14) * mm});
            skLineSegment(sketch, "E1599", {"start": v(20.83, -51.14) * mm, "end": v(20.85, -50.8) * mm});
            skLineSegment(sketch, "E1600", {"start": v(20.85, -50.8) * mm, "end": v(20.86, -50.46) * mm});
            skLineSegment(sketch, "E1601", {"start": v(20.86, -50.46) * mm, "end": v(20.87, -50.14) * mm});
            skLineSegment(sketch, "E1602", {"start": v(20.87, -50.14) * mm, "end": v(20.87, -49.83) * mm});
            skLineSegment(sketch, "E1603", {"start": v(20.87, -49.83) * mm, "end": v(20.87, -49.53) * mm});
            skLineSegment(sketch, "E1604", {"start": v(20.87, -49.53) * mm, "end": v(20.87, -49.24) * mm});
            skLineSegment(sketch, "E1605", {"start": v(20.87, -49.24) * mm, "end": v(20.86, -48.95) * mm});
            skLineSegment(sketch, "E1606", {"start": v(20.86, -48.95) * mm, "end": v(20.85, -48.68) * mm});
            skLineSegment(sketch, "E1607", {"start": v(20.85, -48.68) * mm, "end": v(20.83, -48.43) * mm});
            skLineSegment(sketch, "E1608", {"start": v(20.83, -48.43) * mm, "end": v(20.81, -48.18) * mm});
            skLineSegment(sketch, "E1609", {"start": v(20.81, -48.18) * mm, "end": v(20.8, -47.94) * mm});
            skLineSegment(sketch, "E1610", {"start": v(20.8, -47.94) * mm, "end": v(20.77, -47.71) * mm});
            skLineSegment(sketch, "E1611", {"start": v(20.77, -47.71) * mm, "end": v(20.74, -47.5) * mm});
            skLineSegment(sketch, "E1612", {"start": v(20.74, -47.5) * mm, "end": v(20.71, -47.3) * mm});
            skLineSegment(sketch, "E1613", {"start": v(20.71, -47.3) * mm, "end": v(20.69, -47.1) * mm});
            skLineSegment(sketch, "E1614", {"start": v(20.69, -47.1) * mm, "end": v(20.66, -46.91) * mm});
            skLineSegment(sketch, "E1615", {"start": v(20.66, -46.91) * mm, "end": v(20.62, -46.74) * mm});
            skLineSegment(sketch, "E1616", {"start": v(20.62, -46.74) * mm, "end": v(20.6, -46.58) * mm});
            skLineSegment(sketch, "E1617", {"start": v(20.6, -46.58) * mm, "end": v(20.56, -46.43) * mm});
            skLineSegment(sketch, "E1618", {"start": v(20.56, -46.43) * mm, "end": v(20.53, -46.29) * mm});
            skLineSegment(sketch, "E1619", {"start": v(20.53, -46.29) * mm, "end": v(20.5, -46.15) * mm});
            skLineSegment(sketch, "E1620", {"start": v(20.5, -46.15) * mm, "end": v(20.47, -46.04) * mm});
            skLineSegment(sketch, "E1621", {"start": v(20.47, -46.04) * mm, "end": v(20.44, -45.93) * mm});
            skLineSegment(sketch, "E1622", {"start": v(20.44, -45.93) * mm, "end": v(20.4, -45.83) * mm});
            skLineSegment(sketch, "E1623", {"start": v(20.4, -45.83) * mm, "end": v(20.38, -45.74) * mm});
            skLineSegment(sketch, "E1624", {"start": v(20.38, -45.74) * mm, "end": v(20.36, -45.66) * mm});
            skLineSegment(sketch, "E1625", {"start": v(20.36, -45.66) * mm, "end": v(20.34, -45.6) * mm});
            skLineSegment(sketch, "E1626", {"start": v(20.34, -45.6) * mm, "end": v(20.32, -45.54) * mm});
            skLineSegment(sketch, "E1627", {"start": v(20.32, -45.54) * mm, "end": v(20.3, -45.5) * mm});
            skLineSegment(sketch, "E1628", {"start": v(20.3, -45.5) * mm, "end": v(20.29, -45.46) * mm});
            skLineSegment(sketch, "E1629", {"start": v(20.29, -45.46) * mm, "end": v(20.28, -45.43) * mm});
            skLineSegment(sketch, "E1630", {"start": v(20.28, -45.43) * mm, "end": v(20.27, -45.41) * mm});
            skLineSegment(sketch, "E1631", {"start": v(20.27, -45.41) * mm, "end": v(19.5, -43.7) * mm});
            skLineSegment(sketch, "E1632", {"start": v(19.5, -43.7) * mm, "end": v(23.92, -41.43) * mm});
            skLineSegment(sketch, "E1633", {"start": v(23.92, -41.43) * mm, "end": v(24.87, -43.07) * mm});
            skLineSegment(sketch, "E1634", {"start": v(24.87, -43.07) * mm, "end": v(24.88, -43.09) * mm});
            skLineSegment(sketch, "E1635", {"start": v(24.88, -43.09) * mm, "end": v(24.9, -43.1) * mm});
            skLineSegment(sketch, "E1636", {"start": v(24.9, -43.1) * mm, "end": v(24.91, -43.14) * mm});
            skLineSegment(sketch, "E1637", {"start": v(24.91, -43.14) * mm, "end": v(24.94, -43.18) * mm});
            skLineSegment(sketch, "E1638", {"start": v(24.94, -43.18) * mm, "end": v(24.97, -43.23) * mm});
            skLineSegment(sketch, "E1639", {"start": v(24.97, -43.23) * mm, "end": v(25.02, -43.29) * mm});
            skLineSegment(sketch, "E1640", {"start": v(25.02, -43.29) * mm, "end": v(25.06, -43.35) * mm});
            skLineSegment(sketch, "E1641", {"start": v(25.06, -43.35) * mm, "end": v(25.12, -43.43) * mm});
            skLineSegment(sketch, "E1642", {"start": v(25.12, -43.43) * mm, "end": v(25.18, -43.5) * mm});
            skLineSegment(sketch, "E1643", {"start": v(25.18, -43.5) * mm, "end": v(25.25, -43.6) * mm});
            skLineSegment(sketch, "E1644", {"start": v(25.25, -43.6) * mm, "end": v(25.33, -43.69) * mm});
            skLineSegment(sketch, "E1645", {"start": v(25.33, -43.69) * mm, "end": v(25.42, -43.8) * mm});
            skLineSegment(sketch, "E1646", {"start": v(25.42, -43.8) * mm, "end": v(25.51, -43.9) * mm});
            skLineSegment(sketch, "E1647", {"start": v(25.51, -43.9) * mm, "end": v(25.62, -44.01) * mm});
            skLineSegment(sketch, "E1648", {"start": v(25.62, -44.01) * mm, "end": v(25.73, -44.13) * mm});
            skLineSegment(sketch, "E1649", {"start": v(25.73, -44.13) * mm, "end": v(25.85, -44.26) * mm});
            skLineSegment(sketch, "E1650", {"start": v(25.85, -44.26) * mm, "end": v(25.98, -44.4) * mm});
            skLineSegment(sketch, "E1651", {"start": v(25.98, -44.4) * mm, "end": v(26.12, -44.53) * mm});
            skLineSegment(sketch, "E1652", {"start": v(26.12, -44.53) * mm, "end": v(26.27, -44.67) * mm});
            skLineSegment(sketch, "E1653", {"start": v(26.27, -44.67) * mm, "end": v(26.43, -44.82) * mm});
            skLineSegment(sketch, "E1654", {"start": v(26.43, -44.82) * mm, "end": v(26.6, -44.97) * mm});
            skLineSegment(sketch, "E1655", {"start": v(26.6, -44.97) * mm, "end": v(26.78, -45.13) * mm});
            skLineSegment(sketch, "E1656", {"start": v(26.78, -45.13) * mm, "end": v(26.97, -45.3) * mm});
            skLineSegment(sketch, "E1657", {"start": v(26.97, -45.3) * mm, "end": v(27.17, -45.46) * mm});
            skLineSegment(sketch, "E1658", {"start": v(27.17, -45.46) * mm, "end": v(27.39, -45.63) * mm});
            skLineSegment(sketch, "E1659", {"start": v(27.39, -45.63) * mm, "end": v(27.6, -45.8) * mm});
            skLineSegment(sketch, "E1660", {"start": v(27.6, -45.8) * mm, "end": v(27.84, -45.97) * mm});
            skLineSegment(sketch, "E1661", {"start": v(27.84, -45.97) * mm, "end": v(28.08, -46.15) * mm});
            skLineSegment(sketch, "E1662", {"start": v(28.08, -46.15) * mm, "end": v(28.34, -46.33) * mm});
            skLineSegment(sketch, "E1663", {"start": v(28.34, -46.33) * mm, "end": v(28.6, -46.51) * mm});
            skLineSegment(sketch, "E1664", {"start": v(28.6, -46.51) * mm, "end": v(28.88, -46.7) * mm});
            skLineSegment(sketch, "E1665", {"start": v(28.88, -46.7) * mm, "end": v(29.17, -46.88) * mm});
            skLineSegment(sketch, "E1666", {"start": v(29.17, -46.88) * mm, "end": v(29.47, -47.07) * mm});
            skLineSegment(sketch, "E1667", {"start": v(29.47, -47.07) * mm, "end": v(29.79, -47.26) * mm});
            skLineSegment(sketch, "E1668", {"start": v(29.79, -47.26) * mm, "end": v(30.11, -47.45) * mm});
            skLineSegment(sketch, "E1669", {"start": v(30.11, -47.45) * mm, "end": v(30.45, -47.64) * mm});
            skLineSegment(sketch, "E1670", {"start": v(30.45, -47.64) * mm, "end": v(30.8, -47.83) * mm});
            skLineSegment(sketch, "E1671", {"start": v(30.8, -47.83) * mm, "end": v(31.16, -48.02) * mm});
            skLineSegment(sketch, "E1672", {"start": v(31.16, -48.02) * mm, "end": v(31.38, -47.98) * mm});
            skLineSegment(sketch, "E1673", {"start": v(31.38, -47.98) * mm, "end": v(33.59, -46.46) * mm});
            skLineSegment(sketch, "E1674", {"start": v(33.59, -46.46) * mm, "end": v(33.7, -46.26) * mm});
            skLineSegment(sketch, "E1675", {"start": v(33.7, -46.26) * mm, "end": v(33.66, -45.86) * mm});
            skLineSegment(sketch, "E1676", {"start": v(33.66, -45.86) * mm, "end": v(33.6, -45.47) * mm});
            skLineSegment(sketch, "E1677", {"start": v(33.6, -45.47) * mm, "end": v(33.55, -45.09) * mm});
            skLineSegment(sketch, "E1678", {"start": v(33.55, -45.09) * mm, "end": v(33.49, -44.71) * mm});
            skLineSegment(sketch, "E1679", {"start": v(33.49, -44.71) * mm, "end": v(33.42, -44.35) * mm});
            skLineSegment(sketch, "E1680", {"start": v(33.42, -44.35) * mm, "end": v(33.35, -44) * mm});
            skLineSegment(sketch, "E1681", {"start": v(33.35, -44) * mm, "end": v(33.28, -43.67) * mm});
            skLineSegment(sketch, "E1682", {"start": v(33.28, -43.67) * mm, "end": v(33.21, -43.34) * mm});
            skLineSegment(sketch, "E1683", {"start": v(33.21, -43.34) * mm, "end": v(33.14, -43.03) * mm});
            skLineSegment(sketch, "E1684", {"start": v(33.14, -43.03) * mm, "end": v(33.06, -42.73) * mm});
            skLineSegment(sketch, "E1685", {"start": v(33.06, -42.73) * mm, "end": v(32.98, -42.44) * mm});
            skLineSegment(sketch, "E1686", {"start": v(32.98, -42.44) * mm, "end": v(32.9, -42.16) * mm});
            skLineSegment(sketch, "E1687", {"start": v(32.9, -42.16) * mm, "end": v(32.82, -41.89) * mm});
            skLineSegment(sketch, "E1688", {"start": v(32.82, -41.89) * mm, "end": v(32.74, -41.63) * mm});
            skLineSegment(sketch, "E1689", {"start": v(32.74, -41.63) * mm, "end": v(32.65, -41.38) * mm});
            skLineSegment(sketch, "E1690", {"start": v(32.65, -41.38) * mm, "end": v(32.57, -41.15) * mm});
            skLineSegment(sketch, "E1691", {"start": v(32.57, -41.15) * mm, "end": v(32.5, -40.92) * mm});
            skLineSegment(sketch, "E1692", {"start": v(32.5, -40.92) * mm, "end": v(32.4, -40.71) * mm});
            skLineSegment(sketch, "E1693", {"start": v(32.4, -40.71) * mm, "end": v(32.33, -40.5) * mm});
            skLineSegment(sketch, "E1694", {"start": v(32.33, -40.5) * mm, "end": v(32.25, -40.32) * mm});
            skLineSegment(sketch, "E1695", {"start": v(32.25, -40.32) * mm, "end": v(32.17, -40.14) * mm});
            skLineSegment(sketch, "E1696", {"start": v(32.17, -40.14) * mm, "end": v(32.1, -39.97) * mm});
            skLineSegment(sketch, "E1697", {"start": v(32.1, -39.97) * mm, "end": v(32.02, -39.8) * mm});
            skLineSegment(sketch, "E1698", {"start": v(32.02, -39.8) * mm, "end": v(31.95, -39.66) * mm});
            skLineSegment(sketch, "E1699", {"start": v(31.95, -39.66) * mm, "end": v(31.88, -39.52) * mm});
            skLineSegment(sketch, "E1700", {"start": v(31.88, -39.52) * mm, "end": v(31.8, -39.4) * mm});
            skLineSegment(sketch, "E1701", {"start": v(31.8, -39.4) * mm, "end": v(31.75, -39.28) * mm});
            skLineSegment(sketch, "E1702", {"start": v(31.75, -39.28) * mm, "end": v(31.69, -39.17) * mm});
            skLineSegment(sketch, "E1703", {"start": v(31.69, -39.17) * mm, "end": v(31.63, -39.07) * mm});
            skLineSegment(sketch, "E1704", {"start": v(31.63, -39.07) * mm, "end": v(31.58, -38.98) * mm});
            skLineSegment(sketch, "E1705", {"start": v(31.58, -38.98) * mm, "end": v(31.53, -38.9) * mm});
            skLineSegment(sketch, "E1706", {"start": v(31.53, -38.9) * mm, "end": v(31.48, -38.84) * mm});
            skLineSegment(sketch, "E1707", {"start": v(31.48, -38.84) * mm, "end": v(31.45, -38.78) * mm});
            skLineSegment(sketch, "E1708", {"start": v(31.45, -38.78) * mm, "end": v(31.41, -38.73) * mm});
            skLineSegment(sketch, "E1709", {"start": v(31.41, -38.73) * mm, "end": v(31.38, -38.69) * mm});
            skLineSegment(sketch, "E1710", {"start": v(31.38, -38.69) * mm, "end": v(31.36, -38.66) * mm});
            skLineSegment(sketch, "E1711", {"start": v(31.36, -38.66) * mm, "end": v(31.34, -38.64) * mm});
            skLineSegment(sketch, "E1712", {"start": v(31.34, -38.64) * mm, "end": v(31.33, -38.62) * mm});
            skLineSegment(sketch, "E1713", {"start": v(31.33, -38.62) * mm, "end": v(30.14, -37.16) * mm});
            skLineSegment(sketch, "E1714", {"start": v(30.14, -37.16) * mm, "end": v(33.83, -33.83) * mm});
            skLineSegment(sketch, "E1715", {"start": v(33.83, -33.83) * mm, "end": v(35.17, -35.17) * mm});
            skLineSegment(sketch, "E1716", {"start": v(35.17, -35.17) * mm, "end": v(35.18, -35.18) * mm});
            skLineSegment(sketch, "E1717", {"start": v(35.18, -35.18) * mm, "end": v(35.2, -35.2) * mm});
            skLineSegment(sketch, "E1718", {"start": v(35.2, -35.2) * mm, "end": v(35.23, -35.22) * mm});
            skLineSegment(sketch, "E1719", {"start": v(35.23, -35.22) * mm, "end": v(35.27, -35.26) * mm});
            skLineSegment(sketch, "E1720", {"start": v(35.27, -35.26) * mm, "end": v(35.31, -35.3) * mm});
            skLineSegment(sketch, "E1721", {"start": v(35.31, -35.3) * mm, "end": v(35.37, -35.34) * mm});
            skLineSegment(sketch, "E1722", {"start": v(35.37, -35.34) * mm, "end": v(35.43, -35.4) * mm});
            skLineSegment(sketch, "E1723", {"start": v(35.43, -35.4) * mm, "end": v(35.5, -35.45) * mm});
            skLineSegment(sketch, "E1724", {"start": v(35.5, -35.45) * mm, "end": v(35.58, -35.5) * mm});
            skLineSegment(sketch, "E1725", {"start": v(35.58, -35.5) * mm, "end": v(35.67, -35.57) * mm});
            skLineSegment(sketch, "E1726", {"start": v(35.67, -35.57) * mm, "end": v(35.78, -35.65) * mm});
            skLineSegment(sketch, "E1727", {"start": v(35.78, -35.65) * mm, "end": v(35.89, -35.72) * mm});
            skLineSegment(sketch, "E1728", {"start": v(35.89, -35.72) * mm, "end": v(36, -35.8) * mm});
            skLineSegment(sketch, "E1729", {"start": v(36, -35.8) * mm, "end": v(36.14, -35.88) * mm});
            skLineSegment(sketch, "E1730", {"start": v(36.14, -35.88) * mm, "end": v(36.28, -35.97) * mm});
            skLineSegment(sketch, "E1731", {"start": v(36.28, -35.97) * mm, "end": v(36.43, -36.06) * mm});
            skLineSegment(sketch, "E1732", {"start": v(36.43, -36.06) * mm, "end": v(36.59, -36.16) * mm});
            skLineSegment(sketch, "E1733", {"start": v(36.59, -36.16) * mm, "end": v(36.76, -36.25) * mm});
            skLineSegment(sketch, "E1734", {"start": v(36.76, -36.25) * mm, "end": v(36.94, -36.35) * mm});
            skLineSegment(sketch, "E1735", {"start": v(36.94, -36.35) * mm, "end": v(37.13, -36.45) * mm});
            skLineSegment(sketch, "E1736", {"start": v(37.13, -36.45) * mm, "end": v(37.34, -36.56) * mm});
            skLineSegment(sketch, "E1737", {"start": v(37.34, -36.56) * mm, "end": v(37.55, -36.66) * mm});
            skLineSegment(sketch, "E1738", {"start": v(37.55, -36.66) * mm, "end": v(37.78, -36.77) * mm});
            skLineSegment(sketch, "E1739", {"start": v(37.78, -36.77) * mm, "end": v(38.01, -36.87) * mm});
            skLineSegment(sketch, "E1740", {"start": v(38.01, -36.87) * mm, "end": v(38.26, -36.98) * mm});
            skLineSegment(sketch, "E1741", {"start": v(38.26, -36.98) * mm, "end": v(38.52, -37.1) * mm});
            skLineSegment(sketch, "E1742", {"start": v(38.52, -37.1) * mm, "end": v(38.8, -37.2) * mm});
            skLineSegment(sketch, "E1743", {"start": v(38.8, -37.2) * mm, "end": v(39.07, -37.3) * mm});
            skLineSegment(sketch, "E1744", {"start": v(39.07, -37.3) * mm, "end": v(39.36, -37.42) * mm});
            skLineSegment(sketch, "E1745", {"start": v(39.36, -37.42) * mm, "end": v(39.67, -37.52) * mm});
            skLineSegment(sketch, "E1746", {"start": v(39.67, -37.52) * mm, "end": v(39.99, -37.63) * mm});
            skLineSegment(sketch, "E1747", {"start": v(39.99, -37.63) * mm, "end": v(40.31, -37.73) * mm});
            skLineSegment(sketch, "E1748", {"start": v(40.31, -37.73) * mm, "end": v(40.65, -37.84) * mm});
            skLineSegment(sketch, "E1749", {"start": v(40.65, -37.84) * mm, "end": v(41, -37.94) * mm});
            skLineSegment(sketch, "E1750", {"start": v(41, -37.94) * mm, "end": v(41.37, -38.04) * mm});
            skLineSegment(sketch, "E1751", {"start": v(41.37, -38.04) * mm, "end": v(41.74, -38.13) * mm});
            skLineSegment(sketch, "E1752", {"start": v(41.74, -38.13) * mm, "end": v(42.13, -38.23) * mm});
            skLineSegment(sketch, "E1753", {"start": v(42.13, -38.23) * mm, "end": v(42.52, -38.32) * mm});
            skLineSegment(sketch, "E1754", {"start": v(42.52, -38.32) * mm, "end": v(42.73, -38.22) * mm});
            skLineSegment(sketch, "E1755", {"start": v(42.73, -38.22) * mm, "end": v(44.47, -36.18) * mm});
            skLineSegment(sketch, "E1756", {"start": v(44.47, -36.18) * mm, "end": v(44.53, -35.96) * mm});
            skLineSegment(sketch, "E1757", {"start": v(44.53, -35.96) * mm, "end": v(44.38, -35.59) * mm});
            skLineSegment(sketch, "E1758", {"start": v(44.38, -35.59) * mm, "end": v(44.23, -35.22) * mm});
            skLineSegment(sketch, "E1759", {"start": v(44.23, -35.22) * mm, "end": v(44.07, -34.87) * mm});
            skLineSegment(sketch, "E1760", {"start": v(44.07, -34.87) * mm, "end": v(43.92, -34.52) * mm});
            skLineSegment(sketch, "E1761", {"start": v(43.92, -34.52) * mm, "end": v(43.76, -34.2) * mm});
            skLineSegment(sketch, "E1762", {"start": v(43.76, -34.2) * mm, "end": v(43.6, -33.87) * mm});
            skLineSegment(sketch, "E1763", {"start": v(43.6, -33.87) * mm, "end": v(43.45, -33.57) * mm});
            skLineSegment(sketch, "E1764", {"start": v(43.45, -33.57) * mm, "end": v(43.3, -33.27) * mm});
            skLineSegment(sketch, "E1765", {"start": v(43.3, -33.27) * mm, "end": v(43.14, -32.99) * mm});
            skLineSegment(sketch, "E1766", {"start": v(43.14, -32.99) * mm, "end": v(43, -32.72) * mm});
            skLineSegment(sketch, "E1767", {"start": v(43, -32.72) * mm, "end": v(42.84, -32.46) * mm});
            skLineSegment(sketch, "E1768", {"start": v(42.84, -32.46) * mm, "end": v(42.7, -32.2) * mm});
            skLineSegment(sketch, "E1769", {"start": v(42.7, -32.2) * mm, "end": v(42.54, -31.97) * mm});
            skLineSegment(sketch, "E1770", {"start": v(42.54, -31.97) * mm, "end": v(42.4, -31.74) * mm});
            skLineSegment(sketch, "E1771", {"start": v(42.4, -31.74) * mm, "end": v(42.25, -31.52) * mm});
            skLineSegment(sketch, "E1772", {"start": v(42.25, -31.52) * mm, "end": v(42.11, -31.32) * mm});
            skLineSegment(sketch, "E1773", {"start": v(42.11, -31.32) * mm, "end": v(41.97, -31.12) * mm});
            skLineSegment(sketch, "E1774", {"start": v(41.97, -31.12) * mm, "end": v(41.84, -30.94) * mm});
            skLineSegment(sketch, "E1775", {"start": v(41.84, -30.94) * mm, "end": v(41.71, -30.76) * mm});
            skLineSegment(sketch, "E1776", {"start": v(41.71, -30.76) * mm, "end": v(41.58, -30.6) * mm});
            skLineSegment(sketch, "E1777", {"start": v(41.58, -30.6) * mm, "end": v(41.46, -30.44) * mm});
            skLineSegment(sketch, "E1778", {"start": v(41.46, -30.44) * mm, "end": v(41.34, -30.3) * mm});
            skLineSegment(sketch, "E1779", {"start": v(41.34, -30.3) * mm, "end": v(41.23, -30.17) * mm});
            skLineSegment(sketch, "E1780", {"start": v(41.23, -30.17) * mm, "end": v(41.12, -30.04) * mm});
            skLineSegment(sketch, "E1781", {"start": v(41.12, -30.04) * mm, "end": v(41.02, -29.93) * mm});
            skLineSegment(sketch, "E1782", {"start": v(41.02, -29.93) * mm, "end": v(40.92, -29.82) * mm});
            skLineSegment(sketch, "E1783", {"start": v(40.92, -29.82) * mm, "end": v(40.83, -29.72) * mm});
            skLineSegment(sketch, "E1784", {"start": v(40.83, -29.72) * mm, "end": v(40.74, -29.63) * mm});
            skLineSegment(sketch, "E1785", {"start": v(40.74, -29.63) * mm, "end": v(40.66, -29.55) * mm});
            skLineSegment(sketch, "E1786", {"start": v(40.66, -29.55) * mm, "end": v(40.6, -29.48) * mm});
            skLineSegment(sketch, "E1787", {"start": v(40.6, -29.48) * mm, "end": v(40.52, -29.42) * mm});
            skLineSegment(sketch, "E1788", {"start": v(40.52, -29.42) * mm, "end": v(40.46, -29.37) * mm});
            skLineSegment(sketch, "E1789", {"start": v(40.46, -29.37) * mm, "end": v(40.41, -29.32) * mm});
            skLineSegment(sketch, "E1790", {"start": v(40.41, -29.32) * mm, "end": v(40.37, -29.28) * mm});
            skLineSegment(sketch, "E1791", {"start": v(40.37, -29.28) * mm, "end": v(40.33, -29.25) * mm});
            skLineSegment(sketch, "E1792", {"start": v(40.33, -29.25) * mm, "end": v(40.3, -29.22) * mm});
            skLineSegment(sketch, "E1793", {"start": v(40.3, -29.22) * mm, "end": v(40.28, -29.2) * mm});
            skLineSegment(sketch, "E1794", {"start": v(40.28, -29.2) * mm, "end": v(40.26, -29.2) * mm});
            skLineSegment(sketch, "E1795", {"start": v(40.26, -29.2) * mm, "end": v(38.73, -28.09) * mm});
            skLineSegment(sketch, "E1796", {"start": v(38.73, -28.09) * mm, "end": v(41.43, -23.92) * mm});
            skLineSegment(sketch, "E1797", {"start": v(41.43, -23.92) * mm, "end": v(43.07, -24.87) * mm});
            skLineSegment(sketch, "E1798", {"start": v(43.07, -24.87) * mm, "end": v(43.09, -24.87) * mm});
            skLineSegment(sketch, "E1799", {"start": v(43.09, -24.87) * mm, "end": v(43.11, -24.89) * mm});
            skLineSegment(sketch, "E1800", {"start": v(43.11, -24.89) * mm, "end": v(43.15, -24.9) * mm});
            skLineSegment(sketch, "E1801", {"start": v(43.15, -24.9) * mm, "end": v(43.2, -24.93) * mm});
            skLineSegment(sketch, "E1802", {"start": v(43.2, -24.93) * mm, "end": v(43.24, -24.95) * mm});
            skLineSegment(sketch, "E1803", {"start": v(43.24, -24.95) * mm, "end": v(43.3, -24.98) * mm});
            skLineSegment(sketch, "E1804", {"start": v(43.3, -24.98) * mm, "end": v(43.38, -25.01) * mm});
            skLineSegment(sketch, "E1805", {"start": v(43.38, -25.01) * mm, "end": v(43.47, -25.05) * mm});
            skLineSegment(sketch, "E1806", {"start": v(43.47, -25.05) * mm, "end": v(43.56, -25.09) * mm});
            skLineSegment(sketch, "E1807", {"start": v(43.56, -25.09) * mm, "end": v(43.67, -25.13) * mm});
            skLineSegment(sketch, "E1808", {"start": v(43.67, -25.13) * mm, "end": v(43.78, -25.17) * mm});
            skLineSegment(sketch, "E1809", {"start": v(43.78, -25.17) * mm, "end": v(43.9, -25.22) * mm});
            skLineSegment(sketch, "E1810", {"start": v(43.9, -25.22) * mm, "end": v(44.04, -25.26) * mm});
            skLineSegment(sketch, "E1811", {"start": v(44.04, -25.26) * mm, "end": v(44.2, -25.3) * mm});
            skLineSegment(sketch, "E1812", {"start": v(44.2, -25.3) * mm, "end": v(44.35, -25.36) * mm});
            skLineSegment(sketch, "E1813", {"start": v(44.35, -25.36) * mm, "end": v(44.52, -25.4) * mm});
            skLineSegment(sketch, "E1814", {"start": v(44.52, -25.4) * mm, "end": v(44.7, -25.45) * mm});
            skLineSegment(sketch, "E1815", {"start": v(44.7, -25.45) * mm, "end": v(44.89, -25.5) * mm});
            skLineSegment(sketch, "E1816", {"start": v(44.89, -25.5) * mm, "end": v(45.1, -25.55) * mm});
            skLineSegment(sketch, "E1817", {"start": v(45.1, -25.55) * mm, "end": v(45.3, -25.6) * mm});
            skLineSegment(sketch, "E1818", {"start": v(45.3, -25.6) * mm, "end": v(45.53, -25.65) * mm});
            skLineSegment(sketch, "E1819", {"start": v(45.53, -25.65) * mm, "end": v(45.76, -25.7) * mm});
            skLineSegment(sketch, "E1820", {"start": v(45.76, -25.7) * mm, "end": v(46, -25.74) * mm});
            skLineSegment(sketch, "E1821", {"start": v(46, -25.74) * mm, "end": v(46.26, -25.78) * mm});
            skLineSegment(sketch, "E1822", {"start": v(46.26, -25.78) * mm, "end": v(46.53, -25.82) * mm});
            skLineSegment(sketch, "E1823", {"start": v(46.53, -25.82) * mm, "end": v(46.8, -25.86) * mm});
            skLineSegment(sketch, "E1824", {"start": v(46.8, -25.86) * mm, "end": v(47.1, -25.9) * mm});
            skLineSegment(sketch, "E1825", {"start": v(47.1, -25.9) * mm, "end": v(47.4, -25.92) * mm});
            skLineSegment(sketch, "E1826", {"start": v(47.4, -25.92) * mm, "end": v(47.7, -25.95) * mm});
            skLineSegment(sketch, "E1827", {"start": v(47.7, -25.95) * mm, "end": v(48.03, -25.98) * mm});
            skLineSegment(sketch, "E1828", {"start": v(48.03, -25.98) * mm, "end": v(48.36, -26) * mm});
            skLineSegment(sketch, "E1829", {"start": v(48.36, -26) * mm, "end": v(48.7, -26.02) * mm});
            skLineSegment(sketch, "E1830", {"start": v(48.7, -26.02) * mm, "end": v(49.06, -26.03) * mm});
            skLineSegment(sketch, "E1831", {"start": v(49.06, -26.03) * mm, "end": v(49.43, -26.03) * mm});
            skLineSegment(sketch, "E1832", {"start": v(49.43, -26.03) * mm, "end": v(49.8, -26.04) * mm});
            skLineSegment(sketch, "E1833", {"start": v(49.8, -26.04) * mm, "end": v(50.19, -26.03) * mm});
            skLineSegment(sketch, "E1834", {"start": v(50.19, -26.03) * mm, "end": v(50.58, -26.02) * mm});
            skLineSegment(sketch, "E1835", {"start": v(50.58, -26.02) * mm, "end": v(51, -26) * mm});
            skLineSegment(sketch, "E1836", {"start": v(51, -26) * mm, "end": v(51.16, -25.86) * mm});
            skLineSegment(sketch, "E1837", {"start": v(51.16, -25.86) * mm, "end": v(52.32, -23.44) * mm});
            skLineSegment(sketch, "E1838", {"start": v(52.32, -23.44) * mm, "end": v(52.32, -23.21) * mm});
            skLineSegment(sketch, "E1839", {"start": v(52.32, -23.21) * mm, "end": v(52.08, -22.89) * mm});
            skLineSegment(sketch, "E1840", {"start": v(52.08, -22.89) * mm, "end": v(51.84, -22.57) * mm});
            skLineSegment(sketch, "E1841", {"start": v(51.84, -22.57) * mm, "end": v(51.6, -22.27) * mm});
            skLineSegment(sketch, "E1842", {"start": v(51.6, -22.27) * mm, "end": v(51.36, -21.98) * mm});
            skLineSegment(sketch, "E1843", {"start": v(51.36, -21.98) * mm, "end": v(51.12, -21.7) * mm});
            skLineSegment(sketch, "E1844", {"start": v(51.12, -21.7) * mm, "end": v(50.89, -21.43) * mm});
            skLineSegment(sketch, "E1845", {"start": v(50.89, -21.43) * mm, "end": v(50.66, -21.18) * mm});
            skLineSegment(sketch, "E1846", {"start": v(50.66, -21.18) * mm, "end": v(50.43, -20.93) * mm});
            skLineSegment(sketch, "E1847", {"start": v(50.43, -20.93) * mm, "end": v(50.21, -20.7) * mm});
            skLineSegment(sketch, "E1848", {"start": v(50.21, -20.7) * mm, "end": v(50, -20.47) * mm});
            skLineSegment(sketch, "E1849", {"start": v(50, -20.47) * mm, "end": v(49.78, -20.26) * mm});
            skLineSegment(sketch, "E1850", {"start": v(49.78, -20.26) * mm, "end": v(49.57, -20.06) * mm});
            skLineSegment(sketch, "E1851", {"start": v(49.57, -20.06) * mm, "end": v(49.37, -19.87) * mm});
            skLineSegment(sketch, "E1852", {"start": v(49.37, -19.87) * mm, "end": v(49.17, -19.68) * mm});
            skLineSegment(sketch, "E1853", {"start": v(49.17, -19.68) * mm, "end": v(48.97, -19.51) * mm});
            skLineSegment(sketch, "E1854", {"start": v(48.97, -19.51) * mm, "end": v(48.78, -19.35) * mm});
            skLineSegment(sketch, "E1855", {"start": v(48.78, -19.35) * mm, "end": v(48.6, -19.2) * mm});
            skLineSegment(sketch, "E1856", {"start": v(48.6, -19.2) * mm, "end": v(48.42, -19.05) * mm});
            skLineSegment(sketch, "E1857", {"start": v(48.42, -19.05) * mm, "end": v(48.25, -18.92) * mm});
            skLineSegment(sketch, "E1858", {"start": v(48.25, -18.92) * mm, "end": v(48.09, -18.8) * mm});
            skLineSegment(sketch, "E1859", {"start": v(48.09, -18.8) * mm, "end": v(47.93, -18.68) * mm});
            skLineSegment(sketch, "E1860", {"start": v(47.93, -18.68) * mm, "end": v(47.78, -18.57) * mm});
            skLineSegment(sketch, "E1861", {"start": v(47.78, -18.57) * mm, "end": v(47.63, -18.47) * mm});
            skLineSegment(sketch, "E1862", {"start": v(47.63, -18.47) * mm, "end": v(47.5, -18.37) * mm});
            skLineSegment(sketch, "E1863", {"start": v(47.5, -18.37) * mm, "end": v(47.37, -18.29) * mm});
            skLineSegment(sketch, "E1864", {"start": v(47.37, -18.29) * mm, "end": v(47.24, -18.21) * mm});
            skLineSegment(sketch, "E1865", {"start": v(47.24, -18.21) * mm, "end": v(47.13, -18.14) * mm});
            skLineSegment(sketch, "E1866", {"start": v(47.13, -18.14) * mm, "end": v(47.03, -18.08) * mm});
            skLineSegment(sketch, "E1867", {"start": v(47.03, -18.08) * mm, "end": v(46.93, -18.02) * mm});
            skLineSegment(sketch, "E1868", {"start": v(46.93, -18.02) * mm, "end": v(46.84, -17.97) * mm});
            skLineSegment(sketch, "E1869", {"start": v(46.84, -17.97) * mm, "end": v(46.76, -17.93) * mm});
            skLineSegment(sketch, "E1870", {"start": v(46.76, -17.93) * mm, "end": v(46.69, -17.9) * mm});
            skLineSegment(sketch, "E1871", {"start": v(46.69, -17.9) * mm, "end": v(46.62, -17.86) * mm});
            skLineSegment(sketch, "E1872", {"start": v(46.62, -17.86) * mm, "end": v(46.57, -17.84) * mm});
            skLineSegment(sketch, "E1873", {"start": v(46.57, -17.84) * mm, "end": v(46.52, -17.82) * mm});
            skLineSegment(sketch, "E1874", {"start": v(46.52, -17.82) * mm, "end": v(46.49, -17.8) * mm});
            skLineSegment(sketch, "E1875", {"start": v(46.49, -17.8) * mm, "end": v(46.46, -17.79) * mm});
            skLineSegment(sketch, "E1876", {"start": v(46.46, -17.79) * mm, "end": v(46.45, -17.78) * mm});
            skLineSegment(sketch, "E1877", {"start": v(46.45, -17.78) * mm, "end": v(44.68, -17.1) * mm});
            skLineSegment(sketch, "E1878", {"start": v(44.68, -17.1) * mm, "end": v(46.22, -12.38) * mm});
            skLineSegment(sketch, "E1879", {"start": v(46.22, -12.38) * mm, "end": v(48.04, -12.87) * mm});
            skLineSegment(sketch, "E1880", {"start": v(48.04, -12.87) * mm, "end": v(48.06, -12.88) * mm});
            skLineSegment(sketch, "E1881", {"start": v(48.06, -12.88) * mm, "end": v(48.08, -12.88) * mm});
            skLineSegment(sketch, "E1882", {"start": v(48.08, -12.88) * mm, "end": v(48.12, -12.9) * mm});
            skLineSegment(sketch, "E1883", {"start": v(48.12, -12.9) * mm, "end": v(48.17, -12.9) * mm});
            skLineSegment(sketch, "E1884", {"start": v(48.17, -12.9) * mm, "end": v(48.23, -12.91) * mm});
            skLineSegment(sketch, "E1885", {"start": v(48.23, -12.91) * mm, "end": v(48.3, -12.92) * mm});
            skLineSegment(sketch, "E1886", {"start": v(48.3, -12.92) * mm, "end": v(48.38, -12.93) * mm});
            skLineSegment(sketch, "E1887", {"start": v(48.38, -12.93) * mm, "end": v(48.47, -12.95) * mm});
            skLineSegment(sketch, "E1888", {"start": v(48.47, -12.95) * mm, "end": v(48.57, -12.96) * mm});
            skLineSegment(sketch, "E1889", {"start": v(48.57, -12.96) * mm, "end": v(48.68, -12.97) * mm});
            skLineSegment(sketch, "E1890", {"start": v(48.68, -12.97) * mm, "end": v(48.8, -12.98) * mm});
            skLineSegment(sketch, "E1891", {"start": v(48.8, -12.98) * mm, "end": v(48.94, -13) * mm});
            skLineSegment(sketch, "E1892", {"start": v(48.94, -13) * mm, "end": v(49.08, -13) * mm});
            skLineSegment(sketch, "E1893", {"start": v(49.08, -13) * mm, "end": v(49.24, -13) * mm});
            skLineSegment(sketch, "E1894", {"start": v(49.24, -13) * mm, "end": v(49.4, -13.01) * mm});
            skLineSegment(sketch, "E1895", {"start": v(49.4, -13.01) * mm, "end": v(49.58, -13.02) * mm});
            skLineSegment(sketch, "E1896", {"start": v(49.58, -13.02) * mm, "end": v(49.76, -13.02) * mm});
            skLineSegment(sketch, "E1897", {"start": v(49.76, -13.02) * mm, "end": v(49.96, -13.02) * mm});
            skLineSegment(sketch, "E1898", {"start": v(49.96, -13.02) * mm, "end": v(50.17, -13.01) * mm});
            skLineSegment(sketch, "E1899", {"start": v(50.17, -13.01) * mm, "end": v(50.39, -13) * mm});
            skLineSegment(sketch, "E1900", {"start": v(50.39, -13) * mm, "end": v(50.61, -12.99) * mm});
            skLineSegment(sketch, "E1901", {"start": v(50.61, -12.99) * mm, "end": v(50.85, -12.97) * mm});
            skLineSegment(sketch, "E1902", {"start": v(50.85, -12.97) * mm, "end": v(51.1, -12.95) * mm});
            skLineSegment(sketch, "E1903", {"start": v(51.1, -12.95) * mm, "end": v(51.36, -12.93) * mm});
            skLineSegment(sketch, "E1904", {"start": v(51.36, -12.93) * mm, "end": v(51.63, -12.9) * mm});
            skLineSegment(sketch, "E1905", {"start": v(51.63, -12.9) * mm, "end": v(51.9, -12.86) * mm});
            skLineSegment(sketch, "E1906", {"start": v(51.9, -12.86) * mm, "end": v(52.2, -12.82) * mm});
            skLineSegment(sketch, "E1907", {"start": v(52.2, -12.82) * mm, "end": v(52.5, -12.77) * mm});
            skLineSegment(sketch, "E1908", {"start": v(52.5, -12.77) * mm, "end": v(52.8, -12.72) * mm});
            skLineSegment(sketch, "E1909", {"start": v(52.8, -12.72) * mm, "end": v(53.12, -12.66) * mm});
            skLineSegment(sketch, "E1910", {"start": v(53.12, -12.66) * mm, "end": v(53.44, -12.6) * mm});
            skLineSegment(sketch, "E1911", {"start": v(53.44, -12.6) * mm, "end": v(53.78, -12.52) * mm});
            skLineSegment(sketch, "E1912", {"start": v(53.78, -12.52) * mm, "end": v(54.13, -12.44) * mm});
            skLineSegment(sketch, "E1913", {"start": v(54.13, -12.44) * mm, "end": v(54.48, -12.36) * mm});
            skLineSegment(sketch, "E1914", {"start": v(54.48, -12.36) * mm, "end": v(54.84, -12.26) * mm});
            skLineSegment(sketch, "E1915", {"start": v(54.84, -12.26) * mm, "end": v(55.22, -12.16) * mm});
            skLineSegment(sketch, "E1916", {"start": v(55.22, -12.16) * mm, "end": v(55.6, -12.04) * mm});
            skLineSegment(sketch, "E1917", {"start": v(55.6, -12.04) * mm, "end": v(55.98, -11.92) * mm});
            skLineSegment(sketch, "E1918", {"start": v(55.98, -11.92) * mm, "end": v(56.11, -11.74) * mm});
            skLineSegment(sketch, "E1919", {"start": v(56.11, -11.74) * mm, "end": v(56.6, -9.1) * mm});
            skLineSegment(sketch, "E1920", {"start": v(56.6, -9.1) * mm, "end": v(56.55, -8.88) * mm});
            skLineSegment(sketch, "E1921", {"start": v(56.55, -8.88) * mm, "end": v(56.23, -8.63) * mm});
            skLineSegment(sketch, "E1922", {"start": v(56.23, -8.63) * mm, "end": v(55.91, -8.39) * mm});
            skLineSegment(sketch, "E1923", {"start": v(55.91, -8.39) * mm, "end": v(55.6, -8.16) * mm});
            skLineSegment(sketch, "E1924", {"start": v(55.6, -8.16) * mm, "end": v(55.3, -7.94) * mm});
            skLineSegment(sketch, "E1925", {"start": v(55.3, -7.94) * mm, "end": v(55, -7.73) * mm});
            skLineSegment(sketch, "E1926", {"start": v(55, -7.73) * mm, "end": v(54.7, -7.53) * mm});
            skLineSegment(sketch, "E1927", {"start": v(54.7, -7.53) * mm, "end": v(54.41, -7.34) * mm});
            skLineSegment(sketch, "E1928", {"start": v(54.41, -7.34) * mm, "end": v(54.13, -7.17) * mm});
            skLineSegment(sketch, "E1929", {"start": v(54.13, -7.17) * mm, "end": v(53.86, -7) * mm});
            skLineSegment(sketch, "E1930", {"start": v(53.86, -7) * mm, "end": v(53.59, -6.84) * mm});
            skLineSegment(sketch, "E1931", {"start": v(53.59, -6.84) * mm, "end": v(53.33, -6.69) * mm});
            skLineSegment(sketch, "E1932", {"start": v(53.33, -6.69) * mm, "end": v(53.07, -6.55) * mm});
            skLineSegment(sketch, "E1933", {"start": v(53.07, -6.55) * mm, "end": v(52.83, -6.41) * mm});
            skLineSegment(sketch, "E1934", {"start": v(52.83, -6.41) * mm, "end": v(52.59, -6.29) * mm});
            skLineSegment(sketch, "E1935", {"start": v(52.59, -6.29) * mm, "end": v(52.35, -6.17) * mm});
            skLineSegment(sketch, "E1936", {"start": v(52.35, -6.17) * mm, "end": v(52.13, -6.06) * mm});
            skLineSegment(sketch, "E1937", {"start": v(52.13, -6.06) * mm, "end": v(51.91, -5.96) * mm});
            skLineSegment(sketch, "E1938", {"start": v(51.91, -5.96) * mm, "end": v(51.7, -5.87) * mm});
            skLineSegment(sketch, "E1939", {"start": v(51.7, -5.87) * mm, "end": v(51.5, -5.78) * mm});
            skLineSegment(sketch, "E1940", {"start": v(51.5, -5.78) * mm, "end": v(51.31, -5.7) * mm});
            skLineSegment(sketch, "E1941", {"start": v(51.31, -5.7) * mm, "end": v(51.13, -5.63) * mm});
            skLineSegment(sketch, "E1942", {"start": v(51.13, -5.63) * mm, "end": v(50.95, -5.57) * mm});
            skLineSegment(sketch, "E1943", {"start": v(50.95, -5.57) * mm, "end": v(50.79, -5.5) * mm});
            skLineSegment(sketch, "E1944", {"start": v(50.79, -5.5) * mm, "end": v(50.63, -5.45) * mm});
            skLineSegment(sketch, "E1945", {"start": v(50.63, -5.45) * mm, "end": v(50.49, -5.4) * mm});
            skLineSegment(sketch, "E1946", {"start": v(50.49, -5.4) * mm, "end": v(50.35, -5.36) * mm});
            skLineSegment(sketch, "E1947", {"start": v(50.35, -5.36) * mm, "end": v(50.22, -5.32) * mm});
            skLineSegment(sketch, "E1948", {"start": v(50.22, -5.32) * mm, "end": v(50.1, -5.3) * mm});
            skLineSegment(sketch, "E1949", {"start": v(50.1, -5.3) * mm, "end": v(50, -5.26) * mm});
            skLineSegment(sketch, "E1950", {"start": v(50, -5.26) * mm, "end": v(49.9, -5.24) * mm});
            skLineSegment(sketch, "E1951", {"start": v(49.9, -5.24) * mm, "end": v(49.8, -5.22) * mm});
            skLineSegment(sketch, "E1952", {"start": v(49.8, -5.22) * mm, "end": v(49.73, -5.2) * mm});
            skLineSegment(sketch, "E1953", {"start": v(49.73, -5.2) * mm, "end": v(49.66, -5.19) * mm});
            skLineSegment(sketch, "E1954", {"start": v(49.66, -5.19) * mm, "end": v(49.6, -5.17) * mm});
            skLineSegment(sketch, "E1955", {"start": v(49.6, -5.17) * mm, "end": v(49.55, -5.17) * mm});
            skLineSegment(sketch, "E1956", {"start": v(49.55, -5.17) * mm, "end": v(49.48, -5.16) * mm});
            skLineSegment(sketch, "E1957", {"start": v(49.48, -5.16) * mm, "end": v(49.46, -5.15) * mm});
            skLineSegment(sketch, "E1958", {"start": v(49.46, -5.15) * mm, "end": v(47.59, -4.96) * mm});
            skLineSegment(sketch, "E1959", {"start": v(47.59, -4.96) * mm, "end": v(47.85, 0) * mm});
            skLineSegment(sketch, "E1960", {"start": v(2.65, 0) * mm, "end": v(-2.65, 0) * mm});
            skLineSegment(sketch, "E1961", {"start": v(0, -2.65) * mm, "end": v(0, 2.65) * mm});
            skSolve(sketch);
        }
        {
            var Q0;
            Q0=makeQuery(id+"F0.imprint","IMPRINT",FACE,{"disambiguationData":[TD([[makeQuery(id+"F0.imprint","IMPRINT",EDGE,{"derivedFrom":sQuery(id+"F0.wireOp",EDGE,"E0")}),1.0]])]});
            extrude(context, id + "F1", {"entities" : qUnion([Q0]), "depth" : 6.35 * mm});
        }
    });
